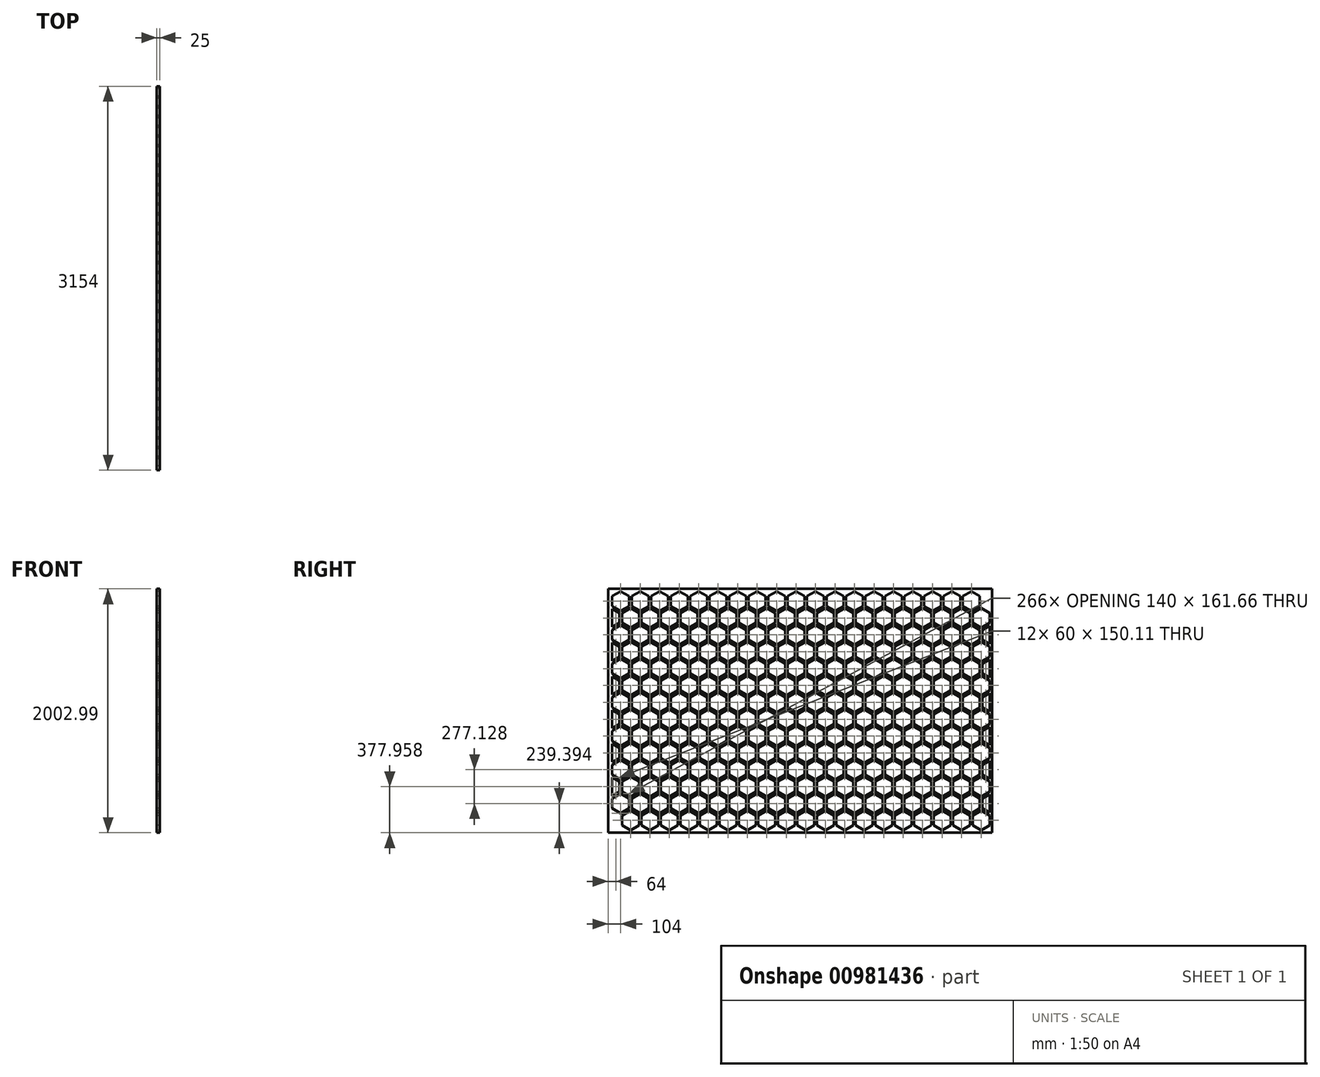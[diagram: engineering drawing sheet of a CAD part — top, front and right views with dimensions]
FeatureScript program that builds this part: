
annotation { "Feature Type Name" : "Feature", "Feature Type Description" : "" }
export const myFeature = defineFeature(function(context is Context, id is Id, definition is map)
    precondition{}
    {
        {
            var Q0;
            Q0=qCreatedBy(makeId("Right.planeOp"),FACE);
            var sketch = newSketch(context, id + "F0", { "sketchPlane" : qUnion([Q0])});
            skLineSegment(sketch, "E0", {"start": v(0, -80.83) * mm, "end": v(-70, -40.41) * mm});
            skLineSegment(sketch, "E1", {"start": v(-70, -40.41) * mm, "end": v(-70, 40.41) * mm});
            skLineSegment(sketch, "E2", {"start": v(-70, 40.41) * mm, "end": v(0, 80.83) * mm});
            skLineSegment(sketch, "E3", {"start": v(0, 80.83) * mm, "end": v(70, 40.41) * mm});
            skLineSegment(sketch, "E4", {"start": v(70, 40.41) * mm, "end": v(70, -40.41) * mm});
            skLineSegment(sketch, "E5", {"start": v(70, -40.41) * mm, "end": v(0, -80.83) * mm});
            skLineSegment(sketch, "E6.MirrorCS", {"start": v(10, 98.15) * mm, "end": v(80, 57.74) * mm});
            skLineSegment(sketch, "E7.MirrorCS", {"start": v(80, 57.74) * mm, "end": v(150, 98.15) * mm});
            skLineSegment(sketch, "E8.MirrorCS", {"start": v(80, 219.4) * mm, "end": v(10, 178.98) * mm});
            skLineSegment(sketch, "E9.MirrorCS", {"start": v(150, 178.98) * mm, "end": v(80, 219.4) * mm});
            skLineSegment(sketch, "E10.MirrorCS", {"start": v(150, 98.15) * mm, "end": v(150, 178.98) * mm});
            skLineSegment(sketch, "E11.MirrorCS", {"start": v(10, 178.98) * mm, "end": v(10, 98.15) * mm});
            skLineSegment(sketch, "E12.MirrorCS", {"start": v(160, -80.83) * mm, "end": v(230, -40.41) * mm});
            skLineSegment(sketch, "E13.MirrorCS", {"start": v(90, 40.41) * mm, "end": v(90, -40.41) * mm});
            skLineSegment(sketch, "E14.MirrorCS", {"start": v(230, 40.41) * mm, "end": v(160, 80.83) * mm});
            skLineSegment(sketch, "E15.MirrorCS", {"start": v(230, -40.41) * mm, "end": v(230, 40.41) * mm});
            skLineSegment(sketch, "E16.MirrorCS", {"start": v(160, 80.83) * mm, "end": v(90, 40.41) * mm});
            skLineSegment(sketch, "E17.MirrorCS", {"start": v(90, -40.41) * mm, "end": v(160, -80.83) * mm});
            skLineSegment(sketch, "E18.MirrorCS", {"start": v(410, 40.41) * mm, "end": v(410, -40.41) * mm});
            skLineSegment(sketch, "E19.MirrorCS", {"start": v(400, 57.74) * mm, "end": v(330, 98.15) * mm});
            skLineSegment(sketch, "E20.MirrorCS", {"start": v(320, 80.83) * mm, "end": v(390, 40.41) * mm});
            skLineSegment(sketch, "E21.MirrorCS", {"start": v(480, 80.83) * mm, "end": v(410, 40.41) * mm});
            skLineSegment(sketch, "E22.MirrorCS", {"start": v(320, -80.83) * mm, "end": v(250, -40.41) * mm});
            skLineSegment(sketch, "E23.MirrorCS", {"start": v(390, 40.41) * mm, "end": v(390, -40.41) * mm});
            skLineSegment(sketch, "E24.MirrorCS", {"start": v(250, -40.41) * mm, "end": v(250, 40.41) * mm});
            skLineSegment(sketch, "E25.MirrorCS", {"start": v(480, -80.83) * mm, "end": v(550, -40.41) * mm});
            skLineSegment(sketch, "E26.MirrorCS", {"start": v(330, 178.98) * mm, "end": v(400, 219.4) * mm});
            skLineSegment(sketch, "E27.MirrorCS", {"start": v(550, 40.41) * mm, "end": v(480, 80.83) * mm});
            skLineSegment(sketch, "E28.MirrorCS", {"start": v(470, 178.98) * mm, "end": v(470, 98.15) * mm});
            skLineSegment(sketch, "E29.MirrorCS", {"start": v(550, -40.41) * mm, "end": v(550, 40.41) * mm});
            skLineSegment(sketch, "E30.MirrorCS", {"start": v(390, -40.41) * mm, "end": v(320, -80.83) * mm});
            skLineSegment(sketch, "E31.MirrorCS", {"start": v(410, -40.41) * mm, "end": v(480, -80.83) * mm});
            skLineSegment(sketch, "E32.MirrorCS", {"start": v(250, 40.41) * mm, "end": v(320, 80.83) * mm});
            skLineSegment(sketch, "E33.MirrorCS", {"start": v(470, 98.15) * mm, "end": v(400, 57.74) * mm});
            skLineSegment(sketch, "E34.MirrorCS", {"start": v(330, 98.15) * mm, "end": v(330, 178.98) * mm});
            skLineSegment(sketch, "E35.MirrorCS", {"start": v(400, 219.4) * mm, "end": v(470, 178.98) * mm});
            skLineSegment(sketch, "E36.MirrorCS", {"start": v(1120, -80.83) * mm, "end": v(1190, -40.41) * mm});
            skLineSegment(sketch, "E37.MirrorCS", {"start": v(870, 40.41) * mm, "end": v(800, 80.83) * mm});
            skLineSegment(sketch, "E38.MirrorCS", {"start": v(800, 80.83) * mm, "end": v(730, 40.41) * mm});
            skLineSegment(sketch, "E39.MirrorCS", {"start": v(640, 80.83) * mm, "end": v(710, 40.41) * mm});
            skLineSegment(sketch, "E40.MirrorCS", {"start": v(790, 178.98) * mm, "end": v(720, 219.4) * mm});
            skLineSegment(sketch, "E41.MirrorCS", {"start": v(960, -80.83) * mm, "end": v(890, -40.41) * mm});
            skLineSegment(sketch, "E42.MirrorCS", {"start": v(570, 40.41) * mm, "end": v(640, 80.83) * mm});
            skLineSegment(sketch, "E43.MirrorCS", {"start": v(1120, 80.83) * mm, "end": v(1050, 40.41) * mm});
            skLineSegment(sketch, "E44.MirrorCS", {"start": v(970, 178.98) * mm, "end": v(1040, 219.4) * mm});
            skLineSegment(sketch, "E45.MirrorCS", {"start": v(650, 98.15) * mm, "end": v(720, 57.74) * mm});
            skLineSegment(sketch, "E46.MirrorCS", {"start": v(710, 40.41) * mm, "end": v(710, -40.41) * mm});
            skLineSegment(sketch, "E47.MirrorCS", {"start": v(1030, 40.41) * mm, "end": v(1030, -40.41) * mm});
            skLineSegment(sketch, "E48.MirrorCS", {"start": v(720, 219.4) * mm, "end": v(650, 178.98) * mm});
            skLineSegment(sketch, "E49.MirrorCS", {"start": v(890, -40.41) * mm, "end": v(890, 40.41) * mm});
            skLineSegment(sketch, "E50.MirrorCS", {"start": v(570, -40.41) * mm, "end": v(570, 40.41) * mm});
            skLineSegment(sketch, "E51.MirrorCS", {"start": v(1110, 98.15) * mm, "end": v(1040, 57.74) * mm});
            skLineSegment(sketch, "E52.MirrorCS", {"start": v(870, -40.41) * mm, "end": v(870, 40.41) * mm});
            skLineSegment(sketch, "E53.MirrorCS", {"start": v(1040, 57.74) * mm, "end": v(970, 98.15) * mm});
            skLineSegment(sketch, "E54.MirrorCS", {"start": v(890, 40.41) * mm, "end": v(960, 80.83) * mm});
            skLineSegment(sketch, "E55.MirrorCS", {"start": v(970, 98.15) * mm, "end": v(970, 178.98) * mm});
            skLineSegment(sketch, "E56.MirrorCS", {"start": v(730, -40.41) * mm, "end": v(800, -80.83) * mm});
            skLineSegment(sketch, "E57.MirrorCS", {"start": v(1110, 178.98) * mm, "end": v(1110, 98.15) * mm});
            skLineSegment(sketch, "E58.MirrorCS", {"start": v(790, 98.15) * mm, "end": v(790, 178.98) * mm});
            skLineSegment(sketch, "E59.MirrorCS", {"start": v(650, 178.98) * mm, "end": v(650, 98.15) * mm});
            skLineSegment(sketch, "E60.MirrorCS", {"start": v(1190, -40.41) * mm, "end": v(1190, 40.41) * mm});
            skLineSegment(sketch, "E61.MirrorCS", {"start": v(1190, 40.41) * mm, "end": v(1120, 80.83) * mm});
            skLineSegment(sketch, "E62.MirrorCS", {"start": v(960, 80.83) * mm, "end": v(1030, 40.41) * mm});
            skLineSegment(sketch, "E63.MirrorCS", {"start": v(710, -40.41) * mm, "end": v(640, -80.83) * mm});
            skLineSegment(sketch, "E64.MirrorCS", {"start": v(1030, -40.41) * mm, "end": v(960, -80.83) * mm});
            skLineSegment(sketch, "E65.MirrorCS", {"start": v(640, -80.83) * mm, "end": v(570, -40.41) * mm});
            skLineSegment(sketch, "E66.MirrorCS", {"start": v(730, 40.41) * mm, "end": v(730, -40.41) * mm});
            skLineSegment(sketch, "E67.MirrorCS", {"start": v(1050, -40.41) * mm, "end": v(1120, -80.83) * mm});
            skLineSegment(sketch, "E68.MirrorCS", {"start": v(720, 57.74) * mm, "end": v(790, 98.15) * mm});
            skLineSegment(sketch, "E69.MirrorCS", {"start": v(800, -80.83) * mm, "end": v(870, -40.41) * mm});
            skLineSegment(sketch, "E70.MirrorCS", {"start": v(1040, 219.4) * mm, "end": v(1110, 178.98) * mm});
            skLineSegment(sketch, "E71.MirrorCS", {"start": v(1050, 40.41) * mm, "end": v(1050, -40.41) * mm});
            skLineSegment(sketch, "E72.MirrorCS", {"start": v(-640, -80.83) * mm, "end": v(-710, -40.41) * mm});
            skLineSegment(sketch, "E73.MirrorCS", {"start": v(-710, 40.41) * mm, "end": v(-640, 80.83) * mm});
            skLineSegment(sketch, "E74.MirrorCS", {"start": v(-710, -40.41) * mm, "end": v(-710, 40.41) * mm});
            skLineSegment(sketch, "E75.MirrorCS", {"start": v(-160, 80.83) * mm, "end": v(-230, 40.41) * mm});
            skLineSegment(sketch, "E76.MirrorCS", {"start": v(-160, -80.83) * mm, "end": v(-90, -40.41) * mm});
            skLineSegment(sketch, "E77.MirrorCS", {"start": v(-250, -40.41) * mm, "end": v(-320, -80.83) * mm});
            skLineSegment(sketch, "E78.MirrorCS", {"start": v(-480, 80.83) * mm, "end": v(-550, 40.41) * mm});
            skLineSegment(sketch, "E79.MirrorCS", {"start": v(-490, 178.98) * mm, "end": v(-560, 219.4) * mm});
            skLineSegment(sketch, "E80.MirrorCS", {"start": v(-630, 98.15) * mm, "end": v(-560, 57.74) * mm});
            skLineSegment(sketch, "E81.MirrorCS", {"start": v(-570, -40.41) * mm, "end": v(-640, -80.83) * mm});
            skLineSegment(sketch, "E82.MirrorCS", {"start": v(-90, -40.41) * mm, "end": v(-90, 40.41) * mm});
            skLineSegment(sketch, "E83.MirrorCS", {"start": v(-630, 178.98) * mm, "end": v(-630, 98.15) * mm});
            skLineSegment(sketch, "E84.MirrorCS", {"start": v(-320, -80.83) * mm, "end": v(-390, -40.41) * mm});
            skLineSegment(sketch, "E85.MirrorCS", {"start": v(-480, -80.83) * mm, "end": v(-410, -40.41) * mm});
            skLineSegment(sketch, "E86.MirrorCS", {"start": v(-490, 98.15) * mm, "end": v(-490, 178.98) * mm});
            skLineSegment(sketch, "E87.MirrorCS", {"start": v(-570, 40.41) * mm, "end": v(-570, -40.41) * mm});
            skLineSegment(sketch, "E88.MirrorCS", {"start": v(-410, 40.41) * mm, "end": v(-480, 80.83) * mm});
            skLineSegment(sketch, "E89.MirrorCS", {"start": v(-170, 178.98) * mm, "end": v(-170, 98.15) * mm});
            skLineSegment(sketch, "E90.MirrorCS", {"start": v(-310, 178.98) * mm, "end": v(-240, 219.4) * mm});
            skLineSegment(sketch, "E91.MirrorCS", {"start": v(-230, 40.41) * mm, "end": v(-230, -40.41) * mm});
            skLineSegment(sketch, "E92.MirrorCS", {"start": v(-550, 40.41) * mm, "end": v(-550, -40.41) * mm});
            skLineSegment(sketch, "E93.MirrorCS", {"start": v(-390, 40.41) * mm, "end": v(-320, 80.83) * mm});
            skLineSegment(sketch, "E94.MirrorCS", {"start": v(-240, 219.4) * mm, "end": v(-170, 178.98) * mm});
            skLineSegment(sketch, "E95.MirrorCS", {"start": v(-560, 57.74) * mm, "end": v(-490, 98.15) * mm});
            skLineSegment(sketch, "E96.MirrorCS", {"start": v(-550, -40.41) * mm, "end": v(-480, -80.83) * mm});
            skLineSegment(sketch, "E97.MirrorCS", {"start": v(-250, 40.41) * mm, "end": v(-250, -40.41) * mm});
            skLineSegment(sketch, "E98.MirrorCS", {"start": v(-90, 40.41) * mm, "end": v(-160, 80.83) * mm});
            skLineSegment(sketch, "E99.MirrorCS", {"start": v(-230, -40.41) * mm, "end": v(-160, -80.83) * mm});
            skLineSegment(sketch, "E100.MirrorCS", {"start": v(-240, 57.74) * mm, "end": v(-310, 98.15) * mm});
            skLineSegment(sketch, "E101.MirrorCS", {"start": v(-310, 98.15) * mm, "end": v(-310, 178.98) * mm});
            skLineSegment(sketch, "E102.MirrorCS", {"start": v(-390, -40.41) * mm, "end": v(-390, 40.41) * mm});
            skLineSegment(sketch, "E103.MirrorCS", {"start": v(-170, 98.15) * mm, "end": v(-240, 57.74) * mm});
            skLineSegment(sketch, "E104.MirrorCS", {"start": v(-320, 80.83) * mm, "end": v(-250, 40.41) * mm});
            skLineSegment(sketch, "E105.MirrorCS", {"start": v(-560, 219.4) * mm, "end": v(-630, 178.98) * mm});
            skLineSegment(sketch, "E106.MirrorCS", {"start": v(-640, 80.83) * mm, "end": v(-570, 40.41) * mm});
            skLineSegment(sketch, "E107.MirrorCS", {"start": v(-410, -40.41) * mm, "end": v(-410, 40.41) * mm});
            skLineSegment(sketch, "E108.MirrorCS", {"start": v(-400, 57.74) * mm, "end": v(-470, 98.15) * mm});
            skLineSegment(sketch, "E109.MirrorCS", {"start": v(-330, 98.15) * mm, "end": v(-400, 57.74) * mm});
            skLineSegment(sketch, "E110.MirrorCS", {"start": v(-400, 219.4) * mm, "end": v(-330, 178.98) * mm});
            skLineSegment(sketch, "E111.MirrorCS", {"start": v(-470, 98.15) * mm, "end": v(-470, 178.98) * mm});
            skLineSegment(sketch, "E112.MirrorCS", {"start": v(-470, 178.98) * mm, "end": v(-400, 219.4) * mm});
            skLineSegment(sketch, "E113.MirrorCS", {"start": v(-330, 178.98) * mm, "end": v(-330, 98.15) * mm});
            skLineSegment(sketch, "E114.MirrorCS", {"start": v(310, 178.98) * mm, "end": v(310, 98.15) * mm});
            skLineSegment(sketch, "E115.MirrorCS", {"start": v(240, 219.4) * mm, "end": v(310, 178.98) * mm});
            skLineSegment(sketch, "E116.MirrorCS", {"start": v(240, 57.74) * mm, "end": v(170, 98.15) * mm});
            skLineSegment(sketch, "E117.MirrorCS", {"start": v(310, 98.15) * mm, "end": v(240, 57.74) * mm});
            skLineSegment(sketch, "E118.MirrorCS", {"start": v(170, 178.98) * mm, "end": v(240, 219.4) * mm});
            skLineSegment(sketch, "E119.MirrorCS", {"start": v(170, 98.15) * mm, "end": v(170, 178.98) * mm});
            skLineSegment(sketch, "E120.MirrorCS", {"start": v(-10, 98.15) * mm, "end": v(-10, 178.98) * mm});
            skLineSegment(sketch, "E121.MirrorCS", {"start": v(-80, 57.74) * mm, "end": v(-10, 98.15) * mm});
            skLineSegment(sketch, "E122.MirrorCS", {"start": v(-150, 98.15) * mm, "end": v(-80, 57.74) * mm});
            skLineSegment(sketch, "E123.MirrorCS", {"start": v(-150, 178.98) * mm, "end": v(-150, 98.15) * mm});
            skLineSegment(sketch, "E124.MirrorCS", {"start": v(-80, 219.4) * mm, "end": v(-150, 178.98) * mm});
            skLineSegment(sketch, "E125.MirrorCS", {"start": v(-10, 178.98) * mm, "end": v(-80, 219.4) * mm});
            skLineSegment(sketch, "E126.MirrorCS", {"start": v(-790, 178.98) * mm, "end": v(-790, 98.15) * mm});
            skLineSegment(sketch, "E127.MirrorCS", {"start": v(-720, 219.4) * mm, "end": v(-790, 178.98) * mm});
            skLineSegment(sketch, "E128.MirrorCS", {"start": v(-650, 178.98) * mm, "end": v(-720, 219.4) * mm});
            skLineSegment(sketch, "E129.MirrorCS", {"start": v(-650, 98.15) * mm, "end": v(-650, 178.98) * mm});
            skLineSegment(sketch, "E130.MirrorCS", {"start": v(-720, 57.74) * mm, "end": v(-650, 98.15) * mm});
            skLineSegment(sketch, "E131.MirrorCS", {"start": v(-790, 98.15) * mm, "end": v(-720, 57.74) * mm});
            skLineSegment(sketch, "E132.MirrorCS", {"start": v(1130, 98.15) * mm, "end": v(1190, 63.5) * mm});
            skLineSegment(sketch, "E133.MirrorCS", {"start": v(1130, 178.98) * mm, "end": v(1130, 98.15) * mm});
            skLineSegment(sketch, "E134.MirrorCS", {"start": v(1190, 213.62) * mm, "end": v(1130, 178.98) * mm});
            skLineSegment(sketch, "E135.MirrorCS", {"start": v(950, 178.98) * mm, "end": v(950, 98.15) * mm});
            skLineSegment(sketch, "E136.MirrorCS", {"start": v(880, 219.4) * mm, "end": v(950, 178.98) * mm});
            skLineSegment(sketch, "E137.MirrorCS", {"start": v(950, 98.15) * mm, "end": v(880, 57.74) * mm});
            skLineSegment(sketch, "E138.MirrorCS", {"start": v(880, 57.74) * mm, "end": v(810, 98.15) * mm});
            skLineSegment(sketch, "E139.MirrorCS", {"start": v(810, 98.15) * mm, "end": v(810, 178.98) * mm});
            skLineSegment(sketch, "E140.MirrorCS", {"start": v(810, 178.98) * mm, "end": v(880, 219.4) * mm});
            skLineSegment(sketch, "E141.MirrorCS", {"start": v(490, 98.15) * mm, "end": v(560, 57.74) * mm});
            skLineSegment(sketch, "E142.MirrorCS", {"start": v(560, 57.74) * mm, "end": v(630, 98.15) * mm});
            skLineSegment(sketch, "E143.MirrorCS", {"start": v(630, 98.15) * mm, "end": v(630, 178.98) * mm});
            skLineSegment(sketch, "E144.MirrorCS", {"start": v(630, 178.98) * mm, "end": v(560, 219.4) * mm});
            skLineSegment(sketch, "E145.MirrorCS", {"start": v(560, 219.4) * mm, "end": v(490, 178.98) * mm});
            skLineSegment(sketch, "E146.MirrorCS", {"start": v(490, 178.98) * mm, "end": v(490, 98.15) * mm});
            skLineSegment(sketch, "E147.MirrorCS", {"start": v(0, 357.96) * mm, "end": v(-70, 317.54) * mm});
            skLineSegment(sketch, "E148.MirrorCS", {"start": v(0, 196.3) * mm, "end": v(70, 236.71) * mm});
            skLineSegment(sketch, "E149.MirrorCS", {"start": v(-70, 236.71) * mm, "end": v(0, 196.3) * mm});
            skLineSegment(sketch, "E150.MirrorCS", {"start": v(-170, 178.98) * mm, "end": v(-240, 219.4) * mm});
            skLineSegment(sketch, "E151.MirrorCS", {"start": v(640, 357.96) * mm, "end": v(570, 317.54) * mm});
            skLineSegment(sketch, "E152.MirrorCS", {"start": v(-80, 219.4) * mm, "end": v(-10, 178.98) * mm});
            skLineSegment(sketch, "E153.MirrorCS", {"start": v(560, 219.4) * mm, "end": v(630, 178.98) * mm});
            skLineSegment(sketch, "E154.MirrorCS", {"start": v(390, 236.71) * mm, "end": v(390, 317.54) * mm});
            skLineSegment(sketch, "E155.MirrorCS", {"start": v(10, 178.98) * mm, "end": v(80, 219.4) * mm});
            skLineSegment(sketch, "E156.MirrorCS", {"start": v(-250, 236.71) * mm, "end": v(-250, 317.54) * mm});
            skLineSegment(sketch, "E157.MirrorCS", {"start": v(710, 236.71) * mm, "end": v(710, 317.54) * mm});
            skLineSegment(sketch, "E158.MirrorCS", {"start": v(240, 219.4) * mm, "end": v(170, 178.98) * mm});
            skLineSegment(sketch, "E159.MirrorCS", {"start": v(-150, 178.98) * mm, "end": v(-80, 219.4) * mm});
            skLineSegment(sketch, "E160.MirrorCS", {"start": v(-400, 219.4) * mm, "end": v(-470, 178.98) * mm});
            skLineSegment(sketch, "E161.MirrorCS", {"start": v(410, 236.71) * mm, "end": v(410, 317.54) * mm});
            skLineSegment(sketch, "E162.MirrorCS", {"start": v(640, 196.3) * mm, "end": v(710, 236.71) * mm});
            skLineSegment(sketch, "E163.MirrorCS", {"start": v(550, 236.71) * mm, "end": v(480, 196.3) * mm});
            skLineSegment(sketch, "E164.MirrorCS", {"start": v(-240, 219.4) * mm, "end": v(-310, 178.98) * mm});
            skLineSegment(sketch, "E165.MirrorCS", {"start": v(480, 357.96) * mm, "end": v(550, 317.54) * mm});
            skLineSegment(sketch, "E166.MirrorCS", {"start": v(570, 236.71) * mm, "end": v(640, 196.3) * mm});
            skLineSegment(sketch, "E167.MirrorCS", {"start": v(-480, 196.3) * mm, "end": v(-550, 236.71) * mm});
            skLineSegment(sketch, "E168.MirrorCS", {"start": v(950, 178.98) * mm, "end": v(880, 219.4) * mm});
            skLineSegment(sketch, "E169.MirrorCS", {"start": v(-480, 357.96) * mm, "end": v(-410, 317.54) * mm});
            skLineSegment(sketch, "E170.MirrorCS", {"start": v(-410, 317.54) * mm, "end": v(-410, 236.71) * mm});
            skLineSegment(sketch, "E171.MirrorCS", {"start": v(-560, 219.4) * mm, "end": v(-490, 178.98) * mm});
            skLineSegment(sketch, "E172.MirrorCS", {"start": v(-550, 317.54) * mm, "end": v(-480, 357.96) * mm});
            skLineSegment(sketch, "E173.MirrorCS", {"start": v(480, 196.3) * mm, "end": v(410, 236.71) * mm});
            skLineSegment(sketch, "E174.MirrorCS", {"start": v(320, 196.3) * mm, "end": v(390, 236.71) * mm});
            skLineSegment(sketch, "E175.MirrorCS", {"start": v(320, 357.96) * mm, "end": v(250, 317.54) * mm});
            skLineSegment(sketch, "E176.MirrorCS", {"start": v(90, 236.71) * mm, "end": v(90, 317.54) * mm});
            skLineSegment(sketch, "E177.MirrorCS", {"start": v(80, 219.4) * mm, "end": v(150, 178.98) * mm});
            skLineSegment(sketch, "E178.MirrorCS", {"start": v(960, 196.3) * mm, "end": v(1030, 236.71) * mm});
            skLineSegment(sketch, "E179.MirrorCS", {"start": v(-230, 317.54) * mm, "end": v(-160, 357.96) * mm});
            skLineSegment(sketch, "E180.MirrorCS", {"start": v(400, 219.4) * mm, "end": v(330, 178.98) * mm});
            skLineSegment(sketch, "E181.MirrorCS", {"start": v(160, 357.96) * mm, "end": v(230, 317.54) * mm});
            skLineSegment(sketch, "E182.MirrorCS", {"start": v(-390, 317.54) * mm, "end": v(-390, 236.71) * mm});
            skLineSegment(sketch, "E183.MirrorCS", {"start": v(650, 178.98) * mm, "end": v(720, 219.4) * mm});
            skLineSegment(sketch, "E184.MirrorCS", {"start": v(-90, 236.71) * mm, "end": v(-160, 196.3) * mm});
            skLineSegment(sketch, "E185.MirrorCS", {"start": v(-330, 178.98) * mm, "end": v(-400, 219.4) * mm});
            skLineSegment(sketch, "E186.MirrorCS", {"start": v(-640, 196.3) * mm, "end": v(-570, 236.71) * mm});
            skLineSegment(sketch, "E187.MirrorCS", {"start": v(1120, 196.3) * mm, "end": v(1050, 236.71) * mm});
            skLineSegment(sketch, "E188.MirrorCS", {"start": v(1030, 317.54) * mm, "end": v(960, 357.96) * mm});
            skLineSegment(sketch, "E189.MirrorCS", {"start": v(160, 196.3) * mm, "end": v(90, 236.71) * mm});
            skLineSegment(sketch, "E190.MirrorCS", {"start": v(470, 178.98) * mm, "end": v(400, 219.4) * mm});
            skLineSegment(sketch, "E191.MirrorCS", {"start": v(880, 219.4) * mm, "end": v(810, 178.98) * mm});
            skLineSegment(sketch, "E192.MirrorCS", {"start": v(310, 178.98) * mm, "end": v(240, 219.4) * mm});
            skLineSegment(sketch, "E193.MirrorCS", {"start": v(-390, 236.71) * mm, "end": v(-320, 196.3) * mm});
            skLineSegment(sketch, "E194.MirrorCS", {"start": v(-410, 236.71) * mm, "end": v(-480, 196.3) * mm});
            skLineSegment(sketch, "E195.MirrorCS", {"start": v(-320, 196.3) * mm, "end": v(-250, 236.71) * mm});
            skLineSegment(sketch, "E196.MirrorCS", {"start": v(-730, 317.54) * mm, "end": v(-730, 236.71) * mm});
            skLineSegment(sketch, "E197.MirrorCS", {"start": v(-710, 236.71) * mm, "end": v(-640, 196.3) * mm});
            skLineSegment(sketch, "E198.MirrorCS", {"start": v(1190, 236.71) * mm, "end": v(1120, 196.3) * mm});
            skLineSegment(sketch, "E199.MirrorCS", {"start": v(230, 317.54) * mm, "end": v(230, 236.71) * mm});
            skLineSegment(sketch, "E200.MirrorCS", {"start": v(-160, 196.3) * mm, "end": v(-230, 236.71) * mm});
            skLineSegment(sketch, "E201.MirrorCS", {"start": v(1190, 317.54) * mm, "end": v(1190, 236.71) * mm});
            skLineSegment(sketch, "E202.MirrorCS", {"start": v(250, 236.71) * mm, "end": v(320, 196.3) * mm});
            skLineSegment(sketch, "E203.MirrorCS", {"start": v(1130, 178.98) * mm, "end": v(1190, 213.62) * mm});
            skLineSegment(sketch, "E204.MirrorCS", {"start": v(720, 219.4) * mm, "end": v(790, 178.98) * mm});
            skLineSegment(sketch, "E205.MirrorCS", {"start": v(870, 236.71) * mm, "end": v(800, 196.3) * mm});
            skLineSegment(sketch, "E206.MirrorCS", {"start": v(410, 317.54) * mm, "end": v(480, 357.96) * mm});
            skLineSegment(sketch, "E207.MirrorCS", {"start": v(730, 317.54) * mm, "end": v(800, 357.96) * mm});
            skLineSegment(sketch, "E208.MirrorCS", {"start": v(-570, 317.54) * mm, "end": v(-640, 357.96) * mm});
            skLineSegment(sketch, "E209.MirrorCS", {"start": v(-230, 236.71) * mm, "end": v(-230, 317.54) * mm});
            skLineSegment(sketch, "E210.MirrorCS", {"start": v(1120, 357.96) * mm, "end": v(1190, 317.54) * mm});
            skLineSegment(sketch, "E211.MirrorCS", {"start": v(1050, 236.71) * mm, "end": v(1050, 317.54) * mm});
            skLineSegment(sketch, "E212.MirrorCS", {"start": v(730, 236.71) * mm, "end": v(730, 317.54) * mm});
            skLineSegment(sketch, "E213.MirrorCS", {"start": v(-250, 317.54) * mm, "end": v(-320, 357.96) * mm});
            skLineSegment(sketch, "E214.MirrorCS", {"start": v(-570, 236.71) * mm, "end": v(-570, 317.54) * mm});
            skLineSegment(sketch, "E215.MirrorCS", {"start": v(-640, 357.96) * mm, "end": v(-710, 317.54) * mm});
            skLineSegment(sketch, "E216.MirrorCS", {"start": v(1040, 219.4) * mm, "end": v(970, 178.98) * mm});
            skLineSegment(sketch, "E217.MirrorCS", {"start": v(-160, 357.96) * mm, "end": v(-90, 317.54) * mm});
            skLineSegment(sketch, "E218.MirrorCS", {"start": v(-710, 317.54) * mm, "end": v(-710, 236.71) * mm});
            skLineSegment(sketch, "E219.MirrorCS", {"start": v(800, 196.3) * mm, "end": v(730, 236.71) * mm});
            skLineSegment(sketch, "E220.MirrorCS", {"start": v(890, 317.54) * mm, "end": v(890, 236.71) * mm});
            skLineSegment(sketch, "E221.MirrorCS", {"start": v(550, 317.54) * mm, "end": v(550, 236.71) * mm});
            skLineSegment(sketch, "E222.MirrorCS", {"start": v(-90, 317.54) * mm, "end": v(-90, 236.71) * mm});
            skLineSegment(sketch, "E223.MirrorCS", {"start": v(-720, 219.4) * mm, "end": v(-650, 178.98) * mm});
            skLineSegment(sketch, "E224.MirrorCS", {"start": v(90, 317.54) * mm, "end": v(160, 357.96) * mm});
            skLineSegment(sketch, "E225.MirrorCS", {"start": v(1110, 178.98) * mm, "end": v(1040, 219.4) * mm});
            skLineSegment(sketch, "E226.MirrorCS", {"start": v(1030, 236.71) * mm, "end": v(1030, 317.54) * mm});
            skLineSegment(sketch, "E227.MirrorCS", {"start": v(250, 317.54) * mm, "end": v(250, 236.71) * mm});
            skLineSegment(sketch, "E228.MirrorCS", {"start": v(-790, 178.98) * mm, "end": v(-720, 219.4) * mm});
            skLineSegment(sketch, "E229.MirrorCS", {"start": v(-630, 178.98) * mm, "end": v(-560, 219.4) * mm});
            skLineSegment(sketch, "E230.MirrorCS", {"start": v(890, 236.71) * mm, "end": v(960, 196.3) * mm});
            skLineSegment(sketch, "E231.MirrorCS", {"start": v(230, 236.71) * mm, "end": v(160, 196.3) * mm});
            skLineSegment(sketch, "E232.MirrorCS", {"start": v(490, 178.98) * mm, "end": v(560, 219.4) * mm});
            skLineSegment(sketch, "E233.MirrorCS", {"start": v(1050, 317.54) * mm, "end": v(1120, 357.96) * mm});
            skLineSegment(sketch, "E234.MirrorCS", {"start": v(70, 317.54) * mm, "end": v(0, 357.96) * mm});
            skLineSegment(sketch, "E235.MirrorCS", {"start": v(870, 317.54) * mm, "end": v(870, 236.71) * mm});
            skLineSegment(sketch, "E236.MirrorCS", {"start": v(-550, 236.71) * mm, "end": v(-550, 317.54) * mm});
            skLineSegment(sketch, "E237.MirrorCS", {"start": v(-320, 357.96) * mm, "end": v(-390, 317.54) * mm});
            skLineSegment(sketch, "E238.MirrorCS", {"start": v(390, 317.54) * mm, "end": v(320, 357.96) * mm});
            skLineSegment(sketch, "E239.MirrorCS", {"start": v(570, 317.54) * mm, "end": v(570, 236.71) * mm});
            skLineSegment(sketch, "E240.MirrorCS", {"start": v(70, 236.71) * mm, "end": v(70, 317.54) * mm});
            skLineSegment(sketch, "E241.MirrorCS", {"start": v(960, 357.96) * mm, "end": v(890, 317.54) * mm});
            skLineSegment(sketch, "E242.MirrorCS", {"start": v(710, 317.54) * mm, "end": v(640, 357.96) * mm});
            skLineSegment(sketch, "E243.MirrorCS", {"start": v(800, 357.96) * mm, "end": v(870, 317.54) * mm});
            skLineSegment(sketch, "E244.MirrorCS", {"start": v(-70, 317.54) * mm, "end": v(-70, 236.71) * mm});
            skLineSegment(sketch, "E245.MirrorCS", {"start": v(1040, 334.86) * mm, "end": v(970, 375.28) * mm});
            skLineSegment(sketch, "E246.MirrorCS", {"start": v(80, 334.86) * mm, "end": v(150, 375.28) * mm});
            skLineSegment(sketch, "E247.MirrorCS", {"start": v(-240, 334.86) * mm, "end": v(-170, 375.28) * mm});
            skLineSegment(sketch, "E248.MirrorCS", {"start": v(0, 635.09) * mm, "end": v(-70, 594.67) * mm});
            skLineSegment(sketch, "E249.MirrorCS", {"start": v(1040, 334.86) * mm, "end": v(1110, 375.28) * mm});
            skLineSegment(sketch, "E250.MirrorCS", {"start": v(0, 473.43) * mm, "end": v(70, 513.84) * mm});
            skLineSegment(sketch, "E251.MirrorCS", {"start": v(-630, 375.28) * mm, "end": v(-560, 334.86) * mm});
            skLineSegment(sketch, "E252.MirrorCS", {"start": v(-720, 334.86) * mm, "end": v(-790, 375.28) * mm});
            skLineSegment(sketch, "E253.MirrorCS", {"start": v(720, 334.86) * mm, "end": v(650, 375.28) * mm});
            skLineSegment(sketch, "E254.MirrorCS", {"start": v(310, 375.28) * mm, "end": v(240, 334.86) * mm});
            skLineSegment(sketch, "E255.MirrorCS", {"start": v(470, 375.28) * mm, "end": v(400, 334.86) * mm});
            skLineSegment(sketch, "E256.MirrorCS", {"start": v(10, 375.28) * mm, "end": v(80, 334.86) * mm});
            skLineSegment(sketch, "E257.MirrorCS", {"start": v(-720, 334.86) * mm, "end": v(-650, 375.28) * mm});
            skLineSegment(sketch, "E258.MirrorCS", {"start": v(-150, 375.28) * mm, "end": v(-80, 334.86) * mm});
            skLineSegment(sketch, "E259.MirrorCS", {"start": v(-470, 375.28) * mm, "end": v(-400, 334.86) * mm});
            skLineSegment(sketch, "E260.MirrorCS", {"start": v(400, 334.86) * mm, "end": v(330, 375.28) * mm});
            skLineSegment(sketch, "E261.MirrorCS", {"start": v(170, 375.28) * mm, "end": v(240, 334.86) * mm});
            skLineSegment(sketch, "E262.MirrorCS", {"start": v(1130, 375.28) * mm, "end": v(1190, 340.64) * mm});
            skLineSegment(sketch, "E263.MirrorCS", {"start": v(-330, 375.28) * mm, "end": v(-400, 334.86) * mm});
            skLineSegment(sketch, "E264.MirrorCS", {"start": v(950, 375.28) * mm, "end": v(880, 334.86) * mm});
            skLineSegment(sketch, "E265.MirrorCS", {"start": v(880, 334.86) * mm, "end": v(810, 375.28) * mm});
            skLineSegment(sketch, "E266.MirrorCS", {"start": v(720, 334.86) * mm, "end": v(790, 375.28) * mm});
            skLineSegment(sketch, "E267.MirrorCS", {"start": v(-240, 334.86) * mm, "end": v(-310, 375.28) * mm});
            skLineSegment(sketch, "E268.MirrorCS", {"start": v(-560, 334.86) * mm, "end": v(-490, 375.28) * mm});
            skLineSegment(sketch, "E269.MirrorCS", {"start": v(560, 334.86) * mm, "end": v(490, 375.28) * mm});
            skLineSegment(sketch, "E270.MirrorCS", {"start": v(560, 334.86) * mm, "end": v(630, 375.28) * mm});
            skLineSegment(sketch, "E271.MirrorCS", {"start": v(-80, 334.86) * mm, "end": v(-10, 375.28) * mm});
            skLineSegment(sketch, "E272.MirrorCS", {"start": v(160, 473.43) * mm, "end": v(90, 513.84) * mm});
            skLineSegment(sketch, "E273.MirrorCS", {"start": v(1110, 375.28) * mm, "end": v(1110, 456.1) * mm});
            skLineSegment(sketch, "E274.MirrorCS", {"start": v(230, 513.84) * mm, "end": v(160, 473.43) * mm});
            skLineSegment(sketch, "E275.MirrorCS", {"start": v(-710, 594.67) * mm, "end": v(-710, 513.84) * mm});
            skLineSegment(sketch, "E276.MirrorCS", {"start": v(-170, 456.1) * mm, "end": v(-240, 496.52) * mm});
            skLineSegment(sketch, "E277.MirrorCS", {"start": v(390, 513.84) * mm, "end": v(390, 594.67) * mm});
            skLineSegment(sketch, "E278.MirrorCS", {"start": v(970, 375.28) * mm, "end": v(1040, 334.86) * mm});
            skLineSegment(sketch, "E279.MirrorCS", {"start": v(1130, 375.28) * mm, "end": v(1130, 456.1) * mm});
            skLineSegment(sketch, "E280.MirrorCS", {"start": v(710, 594.67) * mm, "end": v(640, 635.09) * mm});
            skLineSegment(sketch, "E281.MirrorCS", {"start": v(570, 513.84) * mm, "end": v(640, 473.43) * mm});
            skLineSegment(sketch, "E282.MirrorCS", {"start": v(1190, 594.67) * mm, "end": v(1190, 513.84) * mm});
            skLineSegment(sketch, "E283.MirrorCS", {"start": v(1050, 513.84) * mm, "end": v(1050, 594.67) * mm});
            skLineSegment(sketch, "E284.MirrorCS", {"start": v(870, 317.54) * mm, "end": v(800, 357.96) * mm});
            skLineSegment(sketch, "E285.MirrorCS", {"start": v(630, 375.28) * mm, "end": v(560, 334.86) * mm});
            skLineSegment(sketch, "E286.MirrorCS", {"start": v(90, 594.67) * mm, "end": v(160, 635.09) * mm});
            skLineSegment(sketch, "E287.MirrorCS", {"start": v(640, 357.96) * mm, "end": v(710, 317.54) * mm});
            skLineSegment(sketch, "E288.MirrorCS", {"start": v(-570, 513.84) * mm, "end": v(-570, 594.67) * mm});
            skLineSegment(sketch, "E289.MirrorCS", {"start": v(810, 375.28) * mm, "end": v(880, 334.86) * mm});
            skLineSegment(sketch, "E290.MirrorCS", {"start": v(-790, 375.28) * mm, "end": v(-720, 334.86) * mm});
            skLineSegment(sketch, "E291.MirrorCS", {"start": v(-320, 635.09) * mm, "end": v(-390, 594.67) * mm});
            skLineSegment(sketch, "E292.MirrorCS", {"start": v(-560, 334.86) * mm, "end": v(-630, 375.28) * mm});
            skLineSegment(sketch, "E293.MirrorCS", {"start": v(250, 594.67) * mm, "end": v(250, 513.84) * mm});
            skLineSegment(sketch, "E294.MirrorCS", {"start": v(310, 456.1) * mm, "end": v(240, 496.52) * mm});
            skLineSegment(sketch, "E295.MirrorCS", {"start": v(-790, 456.1) * mm, "end": v(-720, 496.52) * mm});
            skLineSegment(sketch, "E296.MirrorCS", {"start": v(800, 357.96) * mm, "end": v(730, 317.54) * mm});
            skLineSegment(sketch, "E297.MirrorCS", {"start": v(880, 334.86) * mm, "end": v(950, 375.28) * mm});
            skLineSegment(sketch, "E298.MirrorCS", {"start": v(-710, 317.54) * mm, "end": v(-640, 357.96) * mm});
            skLineSegment(sketch, "E299.MirrorCS", {"start": v(-10, 375.28) * mm, "end": v(-80, 334.86) * mm});
            skLineSegment(sketch, "E300.MirrorCS", {"start": v(-560, 496.52) * mm, "end": v(-490, 456.1) * mm});
            skLineSegment(sketch, "E301.MirrorCS", {"start": v(240, 334.86) * mm, "end": v(310, 375.28) * mm});
            skLineSegment(sketch, "E302.MirrorCS", {"start": v(800, 473.43) * mm, "end": v(730, 513.84) * mm});
            skLineSegment(sketch, "E303.MirrorCS", {"start": v(650, 375.28) * mm, "end": v(650, 456.1) * mm});
            skLineSegment(sketch, "E304.MirrorCS", {"start": v(-490, 375.28) * mm, "end": v(-560, 334.86) * mm});
            skLineSegment(sketch, "E305.MirrorCS", {"start": v(160, 635.09) * mm, "end": v(230, 594.67) * mm});
            skLineSegment(sketch, "E306.MirrorCS", {"start": v(960, 473.43) * mm, "end": v(1030, 513.84) * mm});
            skLineSegment(sketch, "E307.MirrorCS", {"start": v(160, 357.96) * mm, "end": v(90, 317.54) * mm});
            skLineSegment(sketch, "E308.MirrorCS", {"start": v(-310, 375.28) * mm, "end": v(-240, 334.86) * mm});
            skLineSegment(sketch, "E309.MirrorCS", {"start": v(890, 594.67) * mm, "end": v(890, 513.84) * mm});
            skLineSegment(sketch, "E310.MirrorCS", {"start": v(-170, 375.28) * mm, "end": v(-240, 334.86) * mm});
            skLineSegment(sketch, "E311.MirrorCS", {"start": v(-330, 375.28) * mm, "end": v(-330, 456.1) * mm});
            skLineSegment(sketch, "E312.MirrorCS", {"start": v(790, 375.28) * mm, "end": v(720, 334.86) * mm});
            skLineSegment(sketch, "E313.MirrorCS", {"start": v(10, 375.28) * mm, "end": v(10, 456.1) * mm});
            skLineSegment(sketch, "E314.MirrorCS", {"start": v(-70, 594.67) * mm, "end": v(-70, 513.84) * mm});
            skLineSegment(sketch, "E315.MirrorCS", {"start": v(-400, 334.86) * mm, "end": v(-330, 375.28) * mm});
            skLineSegment(sketch, "E316.MirrorCS", {"start": v(320, 357.96) * mm, "end": v(390, 317.54) * mm});
            skLineSegment(sketch, "E317.MirrorCS", {"start": v(1120, 357.96) * mm, "end": v(1050, 317.54) * mm});
            skLineSegment(sketch, "E318.MirrorCS", {"start": v(-730, 513.84) * mm, "end": v(-800, 473.43) * mm});
            skLineSegment(sketch, "E319.MirrorCS", {"start": v(-480, 473.43) * mm, "end": v(-550, 513.84) * mm});
            skLineSegment(sketch, "E320.MirrorCS", {"start": v(170, 456.1) * mm, "end": v(170, 375.28) * mm});
            skLineSegment(sketch, "E321.MirrorCS", {"start": v(-320, 473.43) * mm, "end": v(-250, 513.84) * mm});
            skLineSegment(sketch, "E322.MirrorCS", {"start": v(1030, 594.67) * mm, "end": v(960, 635.09) * mm});
            skLineSegment(sketch, "E323.MirrorCS", {"start": v(410, 594.67) * mm, "end": v(480, 635.09) * mm});
            skLineSegment(sketch, "E324.MirrorCS", {"start": v(570, 317.54) * mm, "end": v(640, 357.96) * mm});
            skLineSegment(sketch, "E325.MirrorCS", {"start": v(-250, 594.67) * mm, "end": v(-320, 635.09) * mm});
            skLineSegment(sketch, "E326.MirrorCS", {"start": v(230, 594.67) * mm, "end": v(230, 513.84) * mm});
            skLineSegment(sketch, "E327.MirrorCS", {"start": v(-160, 635.09) * mm, "end": v(-90, 594.67) * mm});
            skLineSegment(sketch, "E328.MirrorCS", {"start": v(1040, 496.52) * mm, "end": v(970, 456.1) * mm});
            skLineSegment(sketch, "E329.MirrorCS", {"start": v(320, 635.09) * mm, "end": v(250, 594.67) * mm});
            skLineSegment(sketch, "E330.MirrorCS", {"start": v(-150, 375.28) * mm, "end": v(-150, 456.1) * mm});
            skLineSegment(sketch, "E331.MirrorCS", {"start": v(-70, 317.54) * mm, "end": v(0, 357.96) * mm});
            skLineSegment(sketch, "E332.MirrorCS", {"start": v(-70, 513.84) * mm, "end": v(0, 473.43) * mm});
            skLineSegment(sketch, "E333.MirrorCS", {"start": v(90, 513.84) * mm, "end": v(90, 594.67) * mm});
            skLineSegment(sketch, "E334.MirrorCS", {"start": v(730, 513.84) * mm, "end": v(730, 594.67) * mm});
            skLineSegment(sketch, "E335.MirrorCS", {"start": v(490, 375.28) * mm, "end": v(490, 456.1) * mm});
            skLineSegment(sketch, "E336.MirrorCS", {"start": v(810, 456.1) * mm, "end": v(810, 375.28) * mm});
            skLineSegment(sketch, "E337.MirrorCS", {"start": v(470, 375.28) * mm, "end": v(470, 456.1) * mm});
            skLineSegment(sketch, "E338.MirrorCS", {"start": v(-400, 334.86) * mm, "end": v(-470, 375.28) * mm});
            skLineSegment(sketch, "E339.MirrorCS", {"start": v(0, 357.96) * mm, "end": v(70, 317.54) * mm});
            skLineSegment(sketch, "E340.MirrorCS", {"start": v(-790, 375.28) * mm, "end": v(-790, 456.1) * mm});
            skLineSegment(sketch, "E341.MirrorCS", {"start": v(-730, 594.67) * mm, "end": v(-730, 513.84) * mm});
            skLineSegment(sketch, "E342.MirrorCS", {"start": v(-170, 375.28) * mm, "end": v(-170, 456.1) * mm});
            skLineSegment(sketch, "E343.MirrorCS", {"start": v(-550, 513.84) * mm, "end": v(-550, 594.67) * mm});
            skLineSegment(sketch, "E344.MirrorCS", {"start": v(-470, 456.1) * mm, "end": v(-470, 375.28) * mm});
            skLineSegment(sketch, "E345.MirrorCS", {"start": v(950, 375.28) * mm, "end": v(950, 456.1) * mm});
            skLineSegment(sketch, "E346.MirrorCS", {"start": v(240, 334.86) * mm, "end": v(170, 375.28) * mm});
            skLineSegment(sketch, "E347.MirrorCS", {"start": v(-480, 357.96) * mm, "end": v(-550, 317.54) * mm});
            skLineSegment(sketch, "E348.MirrorCS", {"start": v(470, 456.1) * mm, "end": v(400, 496.52) * mm});
            skLineSegment(sketch, "E349.MirrorCS", {"start": v(-490, 456.1) * mm, "end": v(-490, 375.28) * mm});
            skLineSegment(sketch, "E350.MirrorCS", {"start": v(-390, 513.84) * mm, "end": v(-320, 473.43) * mm});
            skLineSegment(sketch, "E351.MirrorCS", {"start": v(250, 317.54) * mm, "end": v(320, 357.96) * mm});
            skLineSegment(sketch, "E352.MirrorCS", {"start": v(970, 456.1) * mm, "end": v(970, 375.28) * mm});
            skLineSegment(sketch, "E353.MirrorCS", {"start": v(-250, 513.84) * mm, "end": v(-250, 594.67) * mm});
            skLineSegment(sketch, "E354.MirrorCS", {"start": v(-480, 635.09) * mm, "end": v(-410, 594.67) * mm});
            skLineSegment(sketch, "E355.MirrorCS", {"start": v(-90, 513.84) * mm, "end": v(-160, 473.43) * mm});
            skLineSegment(sketch, "E356.MirrorCS", {"start": v(870, 594.67) * mm, "end": v(870, 513.84) * mm});
            skLineSegment(sketch, "E357.MirrorCS", {"start": v(1120, 635.09) * mm, "end": v(1190, 594.67) * mm});
            skLineSegment(sketch, "E358.MirrorCS", {"start": v(320, 473.43) * mm, "end": v(390, 513.84) * mm});
            skLineSegment(sketch, "E359.MirrorCS", {"start": v(-80, 496.52) * mm, "end": v(-10, 456.1) * mm});
            skLineSegment(sketch, "E360.MirrorCS", {"start": v(-570, 594.67) * mm, "end": v(-640, 635.09) * mm});
            skLineSegment(sketch, "E361.MirrorCS", {"start": v(870, 513.84) * mm, "end": v(800, 473.43) * mm});
            skLineSegment(sketch, "E362.MirrorCS", {"start": v(-10, 456.1) * mm, "end": v(-10, 375.28) * mm});
            skLineSegment(sketch, "E363.MirrorCS", {"start": v(80, 334.86) * mm, "end": v(10, 375.28) * mm});
            skLineSegment(sketch, "E364.MirrorCS", {"start": v(-310, 456.1) * mm, "end": v(-310, 375.28) * mm});
            skLineSegment(sketch, "E365.MirrorCS", {"start": v(70, 594.67) * mm, "end": v(0, 635.09) * mm});
            skLineSegment(sketch, "E366.MirrorCS", {"start": v(480, 635.09) * mm, "end": v(550, 594.67) * mm});
            skLineSegment(sketch, "E367.MirrorCS", {"start": v(250, 513.84) * mm, "end": v(320, 473.43) * mm});
            skLineSegment(sketch, "E368.MirrorCS", {"start": v(570, 594.67) * mm, "end": v(570, 513.84) * mm});
            skLineSegment(sketch, "E369.MirrorCS", {"start": v(1030, 513.84) * mm, "end": v(1030, 594.67) * mm});
            skLineSegment(sketch, "E370.MirrorCS", {"start": v(-90, 594.67) * mm, "end": v(-90, 513.84) * mm});
            skLineSegment(sketch, "E371.MirrorCS", {"start": v(550, 594.67) * mm, "end": v(550, 513.84) * mm});
            skLineSegment(sketch, "E372.MirrorCS", {"start": v(960, 357.96) * mm, "end": v(1030, 317.54) * mm});
            skLineSegment(sketch, "E373.MirrorCS", {"start": v(80, 496.52) * mm, "end": v(150, 456.1) * mm});
            skLineSegment(sketch, "E374.MirrorCS", {"start": v(-640, 473.43) * mm, "end": v(-570, 513.84) * mm});
            skLineSegment(sketch, "E375.MirrorCS", {"start": v(-160, 473.43) * mm, "end": v(-230, 513.84) * mm});
            skLineSegment(sketch, "E376.MirrorCS", {"start": v(-320, 357.96) * mm, "end": v(-250, 317.54) * mm});
            skLineSegment(sketch, "E377.MirrorCS", {"start": v(1190, 340.64) * mm, "end": v(1130, 375.28) * mm});
            skLineSegment(sketch, "E378.MirrorCS", {"start": v(1130, 456.1) * mm, "end": v(1190, 490.75) * mm});
            skLineSegment(sketch, "E379.MirrorCS", {"start": v(640, 635.09) * mm, "end": v(570, 594.67) * mm});
            skLineSegment(sketch, "E380.MirrorCS", {"start": v(-650, 375.28) * mm, "end": v(-720, 334.86) * mm});
            skLineSegment(sketch, "E381.MirrorCS", {"start": v(-410, 317.54) * mm, "end": v(-480, 357.96) * mm});
            skLineSegment(sketch, "E382.MirrorCS", {"start": v(-550, 594.67) * mm, "end": v(-480, 635.09) * mm});
            skLineSegment(sketch, "E383.MirrorCS", {"start": v(-400, 496.52) * mm, "end": v(-470, 456.1) * mm});
            skLineSegment(sketch, "E384.MirrorCS", {"start": v(550, 513.84) * mm, "end": v(480, 473.43) * mm});
            skLineSegment(sketch, "E385.MirrorCS", {"start": v(150, 456.1) * mm, "end": v(150, 375.28) * mm});
            skLineSegment(sketch, "E386.MirrorCS", {"start": v(330, 375.28) * mm, "end": v(400, 334.86) * mm});
            skLineSegment(sketch, "E387.MirrorCS", {"start": v(-720, 496.52) * mm, "end": v(-650, 456.1) * mm});
            skLineSegment(sketch, "E388.MirrorCS", {"start": v(490, 456.1) * mm, "end": v(560, 496.52) * mm});
            skLineSegment(sketch, "E389.MirrorCS", {"start": v(800, 635.09) * mm, "end": v(870, 594.67) * mm});
            skLineSegment(sketch, "E390.MirrorCS", {"start": v(-240, 496.52) * mm, "end": v(-310, 456.1) * mm});
            skLineSegment(sketch, "E391.MirrorCS", {"start": v(-230, 594.67) * mm, "end": v(-160, 635.09) * mm});
            skLineSegment(sketch, "E392.MirrorCS", {"start": v(1190, 513.84) * mm, "end": v(1120, 473.43) * mm});
            skLineSegment(sketch, "E393.MirrorCS", {"start": v(720, 496.52) * mm, "end": v(790, 456.1) * mm});
            skLineSegment(sketch, "E394.MirrorCS", {"start": v(-390, 594.67) * mm, "end": v(-390, 513.84) * mm});
            skLineSegment(sketch, "E395.MirrorCS", {"start": v(-630, 375.28) * mm, "end": v(-630, 456.1) * mm});
            skLineSegment(sketch, "E396.MirrorCS", {"start": v(730, 594.67) * mm, "end": v(800, 635.09) * mm});
            skLineSegment(sketch, "E397.MirrorCS", {"start": v(-90, 317.54) * mm, "end": v(-160, 357.96) * mm});
            skLineSegment(sketch, "E398.MirrorCS", {"start": v(480, 357.96) * mm, "end": v(410, 317.54) * mm});
            skLineSegment(sketch, "E399.MirrorCS", {"start": v(390, 594.67) * mm, "end": v(320, 635.09) * mm});
            skLineSegment(sketch, "E400.MirrorCS", {"start": v(10, 456.1) * mm, "end": v(80, 496.52) * mm});
            skLineSegment(sketch, "E401.MirrorCS", {"start": v(890, 317.54) * mm, "end": v(960, 357.96) * mm});
            skLineSegment(sketch, "E402.MirrorCS", {"start": v(650, 375.28) * mm, "end": v(720, 334.86) * mm});
            skLineSegment(sketch, "E403.MirrorCS", {"start": v(490, 375.28) * mm, "end": v(560, 334.86) * mm});
            skLineSegment(sketch, "E404.MirrorCS", {"start": v(560, 496.52) * mm, "end": v(630, 456.1) * mm});
            skLineSegment(sketch, "E405.MirrorCS", {"start": v(-330, 456.1) * mm, "end": v(-400, 496.52) * mm});
            skLineSegment(sketch, "E406.MirrorCS", {"start": v(1190, 317.54) * mm, "end": v(1120, 357.96) * mm});
            skLineSegment(sketch, "E407.MirrorCS", {"start": v(70, 513.84) * mm, "end": v(70, 594.67) * mm});
            skLineSegment(sketch, "E408.MirrorCS", {"start": v(-410, 513.84) * mm, "end": v(-480, 473.43) * mm});
            skLineSegment(sketch, "E409.MirrorCS", {"start": v(-80, 334.86) * mm, "end": v(-150, 375.28) * mm});
            skLineSegment(sketch, "E410.MirrorCS", {"start": v(-390, 317.54) * mm, "end": v(-320, 357.96) * mm});
            skLineSegment(sketch, "E411.MirrorCS", {"start": v(1050, 594.67) * mm, "end": v(1120, 635.09) * mm});
            skLineSegment(sketch, "E412.MirrorCS", {"start": v(890, 513.84) * mm, "end": v(960, 473.43) * mm});
            skLineSegment(sketch, "E413.MirrorCS", {"start": v(150, 375.28) * mm, "end": v(80, 334.86) * mm});
            skLineSegment(sketch, "E414.MirrorCS", {"start": v(640, 473.43) * mm, "end": v(710, 513.84) * mm});
            skLineSegment(sketch, "E415.MirrorCS", {"start": v(-630, 456.1) * mm, "end": v(-560, 496.52) * mm});
            skLineSegment(sketch, "E416.MirrorCS", {"start": v(790, 456.1) * mm, "end": v(790, 375.28) * mm});
            skLineSegment(sketch, "E417.MirrorCS", {"start": v(-160, 357.96) * mm, "end": v(-230, 317.54) * mm});
            skLineSegment(sketch, "E418.MirrorCS", {"start": v(310, 375.28) * mm, "end": v(310, 456.1) * mm});
            skLineSegment(sketch, "E419.MirrorCS", {"start": v(-150, 456.1) * mm, "end": v(-80, 496.52) * mm});
            skLineSegment(sketch, "E420.MirrorCS", {"start": v(1110, 375.28) * mm, "end": v(1040, 334.86) * mm});
            skLineSegment(sketch, "E421.MirrorCS", {"start": v(550, 317.54) * mm, "end": v(480, 357.96) * mm});
            skLineSegment(sketch, "E422.MirrorCS", {"start": v(-650, 456.1) * mm, "end": v(-650, 375.28) * mm});
            skLineSegment(sketch, "E423.MirrorCS", {"start": v(880, 496.52) * mm, "end": v(810, 456.1) * mm});
            skLineSegment(sketch, "E424.MirrorCS", {"start": v(-640, 357.96) * mm, "end": v(-570, 317.54) * mm});
            skLineSegment(sketch, "E425.MirrorCS", {"start": v(330, 456.1) * mm, "end": v(330, 375.28) * mm});
            skLineSegment(sketch, "E426.MirrorCS", {"start": v(410, 513.84) * mm, "end": v(410, 594.67) * mm});
            skLineSegment(sketch, "E427.MirrorCS", {"start": v(960, 635.09) * mm, "end": v(890, 594.67) * mm});
            skLineSegment(sketch, "E428.MirrorCS", {"start": v(240, 496.52) * mm, "end": v(170, 456.1) * mm});
            skLineSegment(sketch, "E429.MirrorCS", {"start": v(230, 317.54) * mm, "end": v(160, 357.96) * mm});
            skLineSegment(sketch, "E430.MirrorCS", {"start": v(710, 513.84) * mm, "end": v(710, 594.67) * mm});
            skLineSegment(sketch, "E431.MirrorCS", {"start": v(-640, 635.09) * mm, "end": v(-710, 594.67) * mm});
            skLineSegment(sketch, "E432.MirrorCS", {"start": v(1120, 473.43) * mm, "end": v(1050, 513.84) * mm});
            skLineSegment(sketch, "E433.MirrorCS", {"start": v(480, 473.43) * mm, "end": v(410, 513.84) * mm});
            skLineSegment(sketch, "E434.MirrorCS", {"start": v(-710, 513.84) * mm, "end": v(-640, 473.43) * mm});
            skLineSegment(sketch, "E435.MirrorCS", {"start": v(630, 456.1) * mm, "end": v(630, 375.28) * mm});
            skLineSegment(sketch, "E436.MirrorCS", {"start": v(650, 456.1) * mm, "end": v(720, 496.52) * mm});
            skLineSegment(sketch, "E437.MirrorCS", {"start": v(950, 456.1) * mm, "end": v(880, 496.52) * mm});
            skLineSegment(sketch, "E438.MirrorCS", {"start": v(-230, 513.84) * mm, "end": v(-230, 594.67) * mm});
            skLineSegment(sketch, "E439.MirrorCS", {"start": v(1110, 456.1) * mm, "end": v(1040, 496.52) * mm});
            skLineSegment(sketch, "E440.MirrorCS", {"start": v(400, 334.86) * mm, "end": v(470, 375.28) * mm});
            skLineSegment(sketch, "E441.MirrorCS", {"start": v(400, 496.52) * mm, "end": v(330, 456.1) * mm});
            skLineSegment(sketch, "E442.MirrorCS", {"start": v(-410, 594.67) * mm, "end": v(-410, 513.84) * mm});
            skLineSegment(sketch, "E443.MirrorCS", {"start": v(1130, 733.23) * mm, "end": v(1190, 767.88) * mm});
            skLineSegment(sketch, "E444.MirrorCS", {"start": v(320, 750.56) * mm, "end": v(250, 790.97) * mm});
            skLineSegment(sketch, "E445.MirrorCS", {"start": v(950, 733.23) * mm, "end": v(880, 773.65) * mm});
            skLineSegment(sketch, "E446.MirrorCS", {"start": v(-400, 773.65) * mm, "end": v(-470, 733.23) * mm});
            skLineSegment(sketch, "E447.MirrorCS", {"start": v(10, 733.23) * mm, "end": v(80, 773.65) * mm});
            skLineSegment(sketch, "E448.MirrorCS", {"start": v(150, 733.23) * mm, "end": v(80, 773.65) * mm});
            skLineSegment(sketch, "E449.MirrorCS", {"start": v(80, 889.12) * mm, "end": v(150, 929.53) * mm});
            skLineSegment(sketch, "E450.MirrorCS", {"start": v(560, 773.65) * mm, "end": v(630, 733.23) * mm});
            skLineSegment(sketch, "E451.MirrorCS", {"start": v(1190, 790.97) * mm, "end": v(1120, 750.56) * mm});
            skLineSegment(sketch, "E452.MirrorCS", {"start": v(720, 889.12) * mm, "end": v(790, 929.53) * mm});
            skLineSegment(sketch, "E453.MirrorCS", {"start": v(1110, 733.23) * mm, "end": v(1040, 773.65) * mm});
            skLineSegment(sketch, "E454.MirrorCS", {"start": v(-650, 733.23) * mm, "end": v(-720, 773.65) * mm});
            skLineSegment(sketch, "E455.MirrorCS", {"start": v(550, 790.97) * mm, "end": v(480, 750.56) * mm});
            skLineSegment(sketch, "E456.MirrorCS", {"start": v(490, 733.23) * mm, "end": v(560, 773.65) * mm});
            skLineSegment(sketch, "E457.MirrorCS", {"start": v(0, 750.56) * mm, "end": v(70, 790.97) * mm});
            skLineSegment(sketch, "E458.MirrorCS", {"start": v(810, 733.23) * mm, "end": v(880, 773.65) * mm});
            skLineSegment(sketch, "E459.MirrorCS", {"start": v(10, 929.53) * mm, "end": v(80, 889.12) * mm});
            skLineSegment(sketch, "E460.MirrorCS", {"start": v(-80, 889.12) * mm, "end": v(-10, 929.53) * mm});
            skLineSegment(sketch, "E461.MirrorCS", {"start": v(640, 750.56) * mm, "end": v(710, 790.97) * mm});
            skLineSegment(sketch, "E462.MirrorCS", {"start": v(-80, 773.65) * mm, "end": v(-150, 733.23) * mm});
            skLineSegment(sketch, "E463.MirrorCS", {"start": v(-70, 790.97) * mm, "end": v(0, 750.56) * mm});
            skLineSegment(sketch, "E464.MirrorCS", {"start": v(320, 750.56) * mm, "end": v(390, 790.97) * mm});
            skLineSegment(sketch, "E465.MirrorCS", {"start": v(-70, 1068.1) * mm, "end": v(0, 1027.68) * mm});
            skLineSegment(sketch, "E466.MirrorCS", {"start": v(870, 790.97) * mm, "end": v(800, 750.56) * mm});
            skLineSegment(sketch, "E467.MirrorCS", {"start": v(400, 773.65) * mm, "end": v(330, 733.23) * mm});
            skLineSegment(sketch, "E468.MirrorCS", {"start": v(1040, 889.12) * mm, "end": v(970, 929.53) * mm});
            skLineSegment(sketch, "E469.MirrorCS", {"start": v(-630, 929.53) * mm, "end": v(-560, 889.12) * mm});
            skLineSegment(sketch, "E470.MirrorCS", {"start": v(480, 750.56) * mm, "end": v(410, 790.97) * mm});
            skLineSegment(sketch, "E471.MirrorCS", {"start": v(1040, 889.12) * mm, "end": v(1110, 929.53) * mm});
            skLineSegment(sketch, "E472.MirrorCS", {"start": v(0, 1027.68) * mm, "end": v(70, 1068.1) * mm});
            skLineSegment(sketch, "E473.MirrorCS", {"start": v(-240, 889.12) * mm, "end": v(-310, 929.53) * mm});
            skLineSegment(sketch, "E474.MirrorCS", {"start": v(-720, 773.65) * mm, "end": v(-790, 733.23) * mm});
            skLineSegment(sketch, "E475.MirrorCS", {"start": v(470, 929.53) * mm, "end": v(400, 889.12) * mm});
            skLineSegment(sketch, "E476.MirrorCS", {"start": v(-320, 750.56) * mm, "end": v(-250, 790.97) * mm});
            skLineSegment(sketch, "E477.MirrorCS", {"start": v(960, 750.56) * mm, "end": v(1030, 790.97) * mm});
            skLineSegment(sketch, "E478.MirrorCS", {"start": v(790, 733.23) * mm, "end": v(720, 773.65) * mm});
            skLineSegment(sketch, "E479.MirrorCS", {"start": v(-410, 790.97) * mm, "end": v(-480, 750.56) * mm});
            skLineSegment(sketch, "E480.MirrorCS", {"start": v(-150, 929.53) * mm, "end": v(-80, 889.12) * mm});
            skLineSegment(sketch, "E481.MirrorCS", {"start": v(650, 733.23) * mm, "end": v(720, 773.65) * mm});
            skLineSegment(sketch, "E482.MirrorCS", {"start": v(960, 750.56) * mm, "end": v(890, 790.97) * mm});
            skLineSegment(sketch, "E483.MirrorCS", {"start": v(-240, 773.65) * mm, "end": v(-170, 733.23) * mm});
            skLineSegment(sketch, "E484.MirrorCS", {"start": v(-560, 889.12) * mm, "end": v(-490, 929.53) * mm});
            skLineSegment(sketch, "E485.MirrorCS", {"start": v(310, 929.53) * mm, "end": v(240, 889.12) * mm});
            skLineSegment(sketch, "E486.MirrorCS", {"start": v(-640, 750.56) * mm, "end": v(-570, 790.97) * mm});
            skLineSegment(sketch, "E487.MirrorCS", {"start": v(720, 889.12) * mm, "end": v(650, 929.53) * mm});
            skLineSegment(sketch, "E488.MirrorCS", {"start": v(880, 889.12) * mm, "end": v(810, 929.53) * mm});
            skLineSegment(sketch, "E489.MirrorCS", {"start": v(560, 889.12) * mm, "end": v(490, 929.53) * mm});
            skLineSegment(sketch, "E490.MirrorCS", {"start": v(560, 889.12) * mm, "end": v(630, 929.53) * mm});
            skLineSegment(sketch, "E491.MirrorCS", {"start": v(-390, 790.97) * mm, "end": v(-320, 750.56) * mm});
            skLineSegment(sketch, "E492.MirrorCS", {"start": v(-240, 889.12) * mm, "end": v(-170, 929.53) * mm});
            skLineSegment(sketch, "E493.MirrorCS", {"start": v(400, 889.12) * mm, "end": v(330, 929.53) * mm});
            skLineSegment(sketch, "E494.MirrorCS", {"start": v(-240, 773.65) * mm, "end": v(-310, 733.23) * mm});
            skLineSegment(sketch, "E495.MirrorCS", {"start": v(-160, 750.56) * mm, "end": v(-90, 790.97) * mm});
            skLineSegment(sketch, "E496.MirrorCS", {"start": v(-720, 889.12) * mm, "end": v(-650, 929.53) * mm});
            skLineSegment(sketch, "E497.MirrorCS", {"start": v(90, 790.97) * mm, "end": v(160, 750.56) * mm});
            skLineSegment(sketch, "E498.MirrorCS", {"start": v(-560, 773.65) * mm, "end": v(-490, 733.23) * mm});
            skLineSegment(sketch, "E499.MirrorCS", {"start": v(-560, 773.65) * mm, "end": v(-630, 733.23) * mm});
            skLineSegment(sketch, "E500.MirrorCS", {"start": v(0, 1189.34) * mm, "end": v(-70, 1148.93) * mm});
            skLineSegment(sketch, "E501.MirrorCS", {"start": v(-550, 790.97) * mm, "end": v(-480, 750.56) * mm});
            skLineSegment(sketch, "E502.MirrorCS", {"start": v(240, 773.65) * mm, "end": v(170, 733.23) * mm});
            skLineSegment(sketch, "E503.MirrorCS", {"start": v(170, 929.53) * mm, "end": v(240, 889.12) * mm});
            skLineSegment(sketch, "E504.MirrorCS", {"start": v(800, 750.56) * mm, "end": v(730, 790.97) * mm});
            skLineSegment(sketch, "E505.MirrorCS", {"start": v(-330, 733.23) * mm, "end": v(-400, 773.65) * mm});
            skLineSegment(sketch, "E506.MirrorCS", {"start": v(-160, 750.56) * mm, "end": v(-230, 790.97) * mm});
            skLineSegment(sketch, "E507.MirrorCS", {"start": v(950, 929.53) * mm, "end": v(880, 889.12) * mm});
            skLineSegment(sketch, "E508.MirrorCS", {"start": v(-10, 733.23) * mm, "end": v(-80, 773.65) * mm});
            skLineSegment(sketch, "E509.MirrorCS", {"start": v(-470, 929.53) * mm, "end": v(-400, 889.12) * mm});
            skLineSegment(sketch, "E510.MirrorCS", {"start": v(1130, 929.53) * mm, "end": v(1190, 894.9) * mm});
            skLineSegment(sketch, "E511.MirrorCS", {"start": v(-330, 929.53) * mm, "end": v(-400, 889.12) * mm});
            skLineSegment(sketch, "E512.MirrorCS", {"start": v(570, 790.97) * mm, "end": v(640, 750.56) * mm});
            skLineSegment(sketch, "E513.MirrorCS", {"start": v(310, 733.23) * mm, "end": v(240, 773.65) * mm});
            skLineSegment(sketch, "E514.MirrorCS", {"start": v(970, 733.23) * mm, "end": v(1040, 773.65) * mm});
            skLineSegment(sketch, "E515.MirrorCS", {"start": v(230, 790.97) * mm, "end": v(160, 750.56) * mm});
            skLineSegment(sketch, "E516.MirrorCS", {"start": v(1120, 750.56) * mm, "end": v(1050, 790.97) * mm});
            skLineSegment(sketch, "E517.MirrorCS", {"start": v(-640, 750.56) * mm, "end": v(-710, 790.97) * mm});
            skLineSegment(sketch, "E518.MirrorCS", {"start": v(470, 733.23) * mm, "end": v(400, 773.65) * mm});
            skLineSegment(sketch, "E519.MirrorCS", {"start": v(-720, 889.12) * mm, "end": v(-790, 929.53) * mm});
            skLineSegment(sketch, "E520.MirrorCS", {"start": v(550, 790.97) * mm, "end": v(550, 871.8) * mm});
            skLineSegment(sketch, "E521.MirrorCS", {"start": v(570, 790.97) * mm, "end": v(570, 871.8) * mm});
            skLineSegment(sketch, "E522.MirrorCS", {"start": v(310, 929.53) * mm, "end": v(310, 1010.36) * mm});
            skLineSegment(sketch, "E523.MirrorCS", {"start": v(-170, 929.53) * mm, "end": v(-240, 889.12) * mm});
            skLineSegment(sketch, "E524.MirrorCS", {"start": v(880, 773.65) * mm, "end": v(950, 733.23) * mm});
            skLineSegment(sketch, "E525.MirrorCS", {"start": v(710, 790.97) * mm, "end": v(640, 750.56) * mm});
            skLineSegment(sketch, "E526.MirrorCS", {"start": v(250, 1068.1) * mm, "end": v(320, 1027.68) * mm});
            skLineSegment(sketch, "E527.MirrorCS", {"start": v(870, 871.8) * mm, "end": v(800, 912.21) * mm});
            skLineSegment(sketch, "E528.MirrorCS", {"start": v(800, 750.56) * mm, "end": v(870, 790.97) * mm});
            skLineSegment(sketch, "E529.MirrorCS", {"start": v(490, 929.53) * mm, "end": v(490, 1010.36) * mm});
            skLineSegment(sketch, "E530.MirrorCS", {"start": v(-90, 594.67) * mm, "end": v(-160, 635.09) * mm});
            skLineSegment(sketch, "E531.MirrorCS", {"start": v(-560, 1050.78) * mm, "end": v(-490, 1010.36) * mm});
            skLineSegment(sketch, "E532.MirrorCS", {"start": v(-150, 652.4) * mm, "end": v(-80, 612) * mm});
            skLineSegment(sketch, "E533.MirrorCS", {"start": v(70, 1068.1) * mm, "end": v(70, 1148.93) * mm});
            skLineSegment(sketch, "E534.MirrorCS", {"start": v(630, 733.23) * mm, "end": v(560, 773.65) * mm});
            skLineSegment(sketch, "E535.MirrorCS", {"start": v(-790, 733.23) * mm, "end": v(-790, 652.4) * mm});
            skLineSegment(sketch, "E536.MirrorCS", {"start": v(320, 912.21) * mm, "end": v(390, 871.8) * mm});
            skLineSegment(sketch, "E537.MirrorCS", {"start": v(470, 929.53) * mm, "end": v(470, 1010.36) * mm});
            skLineSegment(sketch, "E538.MirrorCS", {"start": v(-80, 773.65) * mm, "end": v(-10, 733.23) * mm});
            skLineSegment(sketch, "E539.MirrorCS", {"start": v(-170, 733.23) * mm, "end": v(-170, 652.4) * mm});
            skLineSegment(sketch, "E540.MirrorCS", {"start": v(230, 1148.93) * mm, "end": v(230, 1068.1) * mm});
            skLineSegment(sketch, "E541.MirrorCS", {"start": v(-490, 652.4) * mm, "end": v(-490, 733.23) * mm});
            skLineSegment(sketch, "E542.MirrorCS", {"start": v(-90, 1068.1) * mm, "end": v(-160, 1027.68) * mm});
            skLineSegment(sketch, "E543.MirrorCS", {"start": v(-480, 750.56) * mm, "end": v(-550, 790.97) * mm});
            skLineSegment(sketch, "E544.MirrorCS", {"start": v(-390, 1148.93) * mm, "end": v(-390, 1068.1) * mm});
            skLineSegment(sketch, "E545.MirrorCS", {"start": v(-640, 1189.34) * mm, "end": v(-710, 1148.93) * mm});
            skLineSegment(sketch, "E546.MirrorCS", {"start": v(1030, 790.97) * mm, "end": v(960, 750.56) * mm});
            skLineSegment(sketch, "E547.MirrorCS", {"start": v(70, 1148.93) * mm, "end": v(0, 1189.34) * mm});
            skLineSegment(sketch, "E548.MirrorCS", {"start": v(-490, 733.23) * mm, "end": v(-560, 773.65) * mm});
            skLineSegment(sketch, "E549.MirrorCS", {"start": v(-160, 1189.34) * mm, "end": v(-90, 1148.93) * mm});
            skLineSegment(sketch, "E550.MirrorCS", {"start": v(880, 773.65) * mm, "end": v(810, 733.23) * mm});
            skLineSegment(sketch, "E551.MirrorCS", {"start": v(-720, 1050.78) * mm, "end": v(-650, 1010.36) * mm});
            skLineSegment(sketch, "E552.MirrorCS", {"start": v(1110, 929.53) * mm, "end": v(1110, 1010.36) * mm});
            skLineSegment(sketch, "E553.MirrorCS", {"start": v(810, 652.4) * mm, "end": v(810, 733.23) * mm});
            skLineSegment(sketch, "E554.MirrorCS", {"start": v(1130, 652.4) * mm, "end": v(1190, 617.76) * mm});
            skLineSegment(sketch, "E555.MirrorCS", {"start": v(-400, 1050.78) * mm, "end": v(-470, 1010.36) * mm});
            skLineSegment(sketch, "E556.MirrorCS", {"start": v(80, 612) * mm, "end": v(150, 652.4) * mm});
            skLineSegment(sketch, "E557.MirrorCS", {"start": v(-10, 652.4) * mm, "end": v(-10, 733.23) * mm});
            skLineSegment(sketch, "E558.MirrorCS", {"start": v(-90, 790.97) * mm, "end": v(-160, 750.56) * mm});
            skLineSegment(sketch, "E559.MirrorCS", {"start": v(1030, 1068.1) * mm, "end": v(1030, 1148.93) * mm});
            skLineSegment(sketch, "E560.MirrorCS", {"start": v(-150, 733.23) * mm, "end": v(-80, 773.65) * mm});
            skLineSegment(sketch, "E561.MirrorCS", {"start": v(390, 1068.1) * mm, "end": v(390, 1148.93) * mm});
            skLineSegment(sketch, "E562.MirrorCS", {"start": v(570, 1068.1) * mm, "end": v(640, 1027.68) * mm});
            skLineSegment(sketch, "E563.MirrorCS", {"start": v(570, 871.8) * mm, "end": v(640, 912.21) * mm});
            skLineSegment(sketch, "E564.MirrorCS", {"start": v(150, 929.53) * mm, "end": v(80, 889.12) * mm});
            skLineSegment(sketch, "E565.MirrorCS", {"start": v(1190, 894.9) * mm, "end": v(1130, 929.53) * mm});
            skLineSegment(sketch, "E566.MirrorCS", {"start": v(800, 635.09) * mm, "end": v(730, 594.67) * mm});
            skLineSegment(sketch, "E567.MirrorCS", {"start": v(-400, 889.12) * mm, "end": v(-330, 929.53) * mm});
            skLineSegment(sketch, "E568.MirrorCS", {"start": v(800, 1189.34) * mm, "end": v(870, 1148.93) * mm});
            skLineSegment(sketch, "E569.MirrorCS", {"start": v(1120, 1189.34) * mm, "end": v(1190, 1148.93) * mm});
            skLineSegment(sketch, "E570.MirrorCS", {"start": v(1190, 767.88) * mm, "end": v(1130, 733.23) * mm});
            skLineSegment(sketch, "E571.MirrorCS", {"start": v(720, 773.65) * mm, "end": v(650, 733.23) * mm});
            skLineSegment(sketch, "E572.MirrorCS", {"start": v(-470, 733.23) * mm, "end": v(-400, 773.65) * mm});
            skLineSegment(sketch, "E573.MirrorCS", {"start": v(170, 733.23) * mm, "end": v(240, 773.65) * mm});
            skLineSegment(sketch, "E574.MirrorCS", {"start": v(320, 1189.34) * mm, "end": v(250, 1148.93) * mm});
            skLineSegment(sketch, "E575.MirrorCS", {"start": v(1190, 594.67) * mm, "end": v(1120, 635.09) * mm});
            skLineSegment(sketch, "E576.MirrorCS", {"start": v(640, 750.56) * mm, "end": v(570, 790.97) * mm});
            skLineSegment(sketch, "E577.MirrorCS", {"start": v(1110, 1010.36) * mm, "end": v(1040, 1050.78) * mm});
            skLineSegment(sketch, "E578.MirrorCS", {"start": v(-320, 1189.34) * mm, "end": v(-390, 1148.93) * mm});
            skLineSegment(sketch, "E579.MirrorCS", {"start": v(550, 1148.93) * mm, "end": v(550, 1068.1) * mm});
            skLineSegment(sketch, "E580.MirrorCS", {"start": v(310, 652.4) * mm, "end": v(240, 612) * mm});
            skLineSegment(sketch, "E581.MirrorCS", {"start": v(250, 1148.93) * mm, "end": v(250, 1068.1) * mm});
            skLineSegment(sketch, "E582.MirrorCS", {"start": v(-320, 1027.68) * mm, "end": v(-250, 1068.1) * mm});
            skLineSegment(sketch, "E583.MirrorCS", {"start": v(880, 1050.78) * mm, "end": v(810, 1010.36) * mm});
            skLineSegment(sketch, "E584.MirrorCS", {"start": v(470, 1010.36) * mm, "end": v(400, 1050.78) * mm});
            skLineSegment(sketch, "E585.MirrorCS", {"start": v(640, 1189.34) * mm, "end": v(570, 1148.93) * mm});
            skLineSegment(sketch, "E586.MirrorCS", {"start": v(400, 612) * mm, "end": v(330, 652.4) * mm});
            skLineSegment(sketch, "E587.MirrorCS", {"start": v(250, 790.97) * mm, "end": v(320, 750.56) * mm});
            skLineSegment(sketch, "E588.MirrorCS", {"start": v(-710, 1068.1) * mm, "end": v(-640, 1027.68) * mm});
            skLineSegment(sketch, "E589.MirrorCS", {"start": v(560, 1050.78) * mm, "end": v(630, 1010.36) * mm});
            skLineSegment(sketch, "E590.MirrorCS", {"start": v(-10, 929.53) * mm, "end": v(-80, 889.12) * mm});
            skLineSegment(sketch, "E591.MirrorCS", {"start": v(890, 1148.93) * mm, "end": v(890, 1068.1) * mm});
            skLineSegment(sketch, "E592.MirrorCS", {"start": v(-710, 1148.93) * mm, "end": v(-710, 1068.1) * mm});
            skLineSegment(sketch, "E593.MirrorCS", {"start": v(-70, 1148.93) * mm, "end": v(-70, 1068.1) * mm});
            skLineSegment(sketch, "E594.MirrorCS", {"start": v(240, 773.65) * mm, "end": v(310, 733.23) * mm});
            skLineSegment(sketch, "E595.MirrorCS", {"start": v(-310, 1010.36) * mm, "end": v(-310, 929.53) * mm});
            skLineSegment(sketch, "E596.MirrorCS", {"start": v(-250, 1068.1) * mm, "end": v(-250, 1148.93) * mm});
            skLineSegment(sketch, "E597.MirrorCS", {"start": v(640, 635.09) * mm, "end": v(710, 594.67) * mm});
            skLineSegment(sketch, "E598.MirrorCS", {"start": v(400, 773.65) * mm, "end": v(470, 733.23) * mm});
            skLineSegment(sketch, "E599.MirrorCS", {"start": v(-720, 773.65) * mm, "end": v(-650, 733.23) * mm});
            skLineSegment(sketch, "E600.MirrorCS", {"start": v(330, 929.53) * mm, "end": v(400, 889.12) * mm});
            skLineSegment(sketch, "E601.MirrorCS", {"start": v(1050, 1068.1) * mm, "end": v(1050, 1148.93) * mm});
            skLineSegment(sketch, "E602.MirrorCS", {"start": v(10, 733.23) * mm, "end": v(10, 652.4) * mm});
            skLineSegment(sketch, "E603.MirrorCS", {"start": v(-90, 790.97) * mm, "end": v(-90, 871.8) * mm});
            skLineSegment(sketch, "E604.MirrorCS", {"start": v(90, 1068.1) * mm, "end": v(90, 1148.93) * mm});
            skLineSegment(sketch, "E605.MirrorCS", {"start": v(70, 790.97) * mm, "end": v(0, 750.56) * mm});
            skLineSegment(sketch, "E606.MirrorCS", {"start": v(1050, 790.97) * mm, "end": v(1120, 750.56) * mm});
            skLineSegment(sketch, "E607.MirrorCS", {"start": v(-790, 733.23) * mm, "end": v(-720, 773.65) * mm});
            skLineSegment(sketch, "E608.MirrorCS", {"start": v(160, 912.21) * mm, "end": v(90, 871.8) * mm});
            skLineSegment(sketch, "E609.MirrorCS", {"start": v(-640, 1027.68) * mm, "end": v(-570, 1068.1) * mm});
            skLineSegment(sketch, "E610.MirrorCS", {"start": v(710, 1148.93) * mm, "end": v(640, 1189.34) * mm});
            skLineSegment(sketch, "E611.MirrorCS", {"start": v(1110, 652.4) * mm, "end": v(1040, 612) * mm});
            skLineSegment(sketch, "E612.MirrorCS", {"start": v(-650, 1010.36) * mm, "end": v(-650, 929.53) * mm});
            skLineSegment(sketch, "E613.MirrorCS", {"start": v(720, 1050.78) * mm, "end": v(790, 1010.36) * mm});
            skLineSegment(sketch, "E614.MirrorCS", {"start": v(-410, 790.97) * mm, "end": v(-410, 871.8) * mm});
            skLineSegment(sketch, "E615.MirrorCS", {"start": v(-720, 612) * mm, "end": v(-650, 652.4) * mm});
            skLineSegment(sketch, "E616.MirrorCS", {"start": v(-480, 1027.68) * mm, "end": v(-550, 1068.1) * mm});
            skLineSegment(sketch, "E617.MirrorCS", {"start": v(10, 1010.36) * mm, "end": v(80, 1050.78) * mm});
            skLineSegment(sketch, "E618.MirrorCS", {"start": v(150, 1010.36) * mm, "end": v(150, 929.53) * mm});
            skLineSegment(sketch, "E619.MirrorCS", {"start": v(720, 612) * mm, "end": v(790, 652.4) * mm});
            skLineSegment(sketch, "E620.MirrorCS", {"start": v(-560, 889.12) * mm, "end": v(-630, 929.53) * mm});
            skLineSegment(sketch, "E621.MirrorCS", {"start": v(-390, 594.67) * mm, "end": v(-320, 635.09) * mm});
            skLineSegment(sketch, "E622.MirrorCS", {"start": v(-480, 1189.34) * mm, "end": v(-410, 1148.93) * mm});
            skLineSegment(sketch, "E623.MirrorCS", {"start": v(790, 929.53) * mm, "end": v(720, 889.12) * mm});
            skLineSegment(sketch, "E624.MirrorCS", {"start": v(400, 1050.78) * mm, "end": v(330, 1010.36) * mm});
            skLineSegment(sketch, "E625.MirrorCS", {"start": v(230, 594.67) * mm, "end": v(160, 635.09) * mm});
            skLineSegment(sketch, "E626.MirrorCS", {"start": v(1130, 1010.36) * mm, "end": v(1190, 1045) * mm});
            skLineSegment(sketch, "E627.MirrorCS", {"start": v(-470, 1010.36) * mm, "end": v(-470, 929.53) * mm});
            skLineSegment(sketch, "E628.MirrorCS", {"start": v(90, 1148.93) * mm, "end": v(160, 1189.34) * mm});
            skLineSegment(sketch, "E629.MirrorCS", {"start": v(1120, 912.21) * mm, "end": v(1050, 871.8) * mm});
            skLineSegment(sketch, "E630.MirrorCS", {"start": v(310, 1010.36) * mm, "end": v(240, 1050.78) * mm});
            skLineSegment(sketch, "E631.MirrorCS", {"start": v(890, 1068.1) * mm, "end": v(960, 1027.68) * mm});
            skLineSegment(sketch, "E632.MirrorCS", {"start": v(-480, 750.56) * mm, "end": v(-410, 790.97) * mm});
            skLineSegment(sketch, "E633.MirrorCS", {"start": v(950, 733.23) * mm, "end": v(950, 652.4) * mm});
            skLineSegment(sketch, "E634.MirrorCS", {"start": v(-470, 652.4) * mm, "end": v(-470, 733.23) * mm});
            skLineSegment(sketch, "E635.MirrorCS", {"start": v(-570, 1068.1) * mm, "end": v(-570, 1148.93) * mm});
            skLineSegment(sketch, "E636.MirrorCS", {"start": v(-650, 652.4) * mm, "end": v(-650, 733.23) * mm});
            skLineSegment(sketch, "E637.MirrorCS", {"start": v(-230, 1068.1) * mm, "end": v(-230, 1148.93) * mm});
            skLineSegment(sketch, "E638.MirrorCS", {"start": v(1190, 1068.1) * mm, "end": v(1120, 1027.68) * mm});
            skLineSegment(sketch, "E639.MirrorCS", {"start": v(80, 773.65) * mm, "end": v(150, 733.23) * mm});
            skLineSegment(sketch, "E640.MirrorCS", {"start": v(90, 871.8) * mm, "end": v(90, 790.97) * mm});
            skLineSegment(sketch, "E641.MirrorCS", {"start": v(240, 889.12) * mm, "end": v(170, 929.53) * mm});
            skLineSegment(sketch, "E642.MirrorCS", {"start": v(570, 1148.93) * mm, "end": v(570, 1068.1) * mm});
            skLineSegment(sketch, "E643.MirrorCS", {"start": v(-480, 912.21) * mm, "end": v(-550, 871.8) * mm});
            skLineSegment(sketch, "E644.MirrorCS", {"start": v(730, 790.97) * mm, "end": v(800, 750.56) * mm});
            skLineSegment(sketch, "E645.MirrorCS", {"start": v(400, 889.12) * mm, "end": v(470, 929.53) * mm});
            skLineSegment(sketch, "E646.MirrorCS", {"start": v(320, 1027.68) * mm, "end": v(390, 1068.1) * mm});
            skLineSegment(sketch, "E647.MirrorCS", {"start": v(-480, 635.09) * mm, "end": v(-550, 594.67) * mm});
            skLineSegment(sketch, "E648.MirrorCS", {"start": v(-640, 912.21) * mm, "end": v(-570, 871.8) * mm});
            skLineSegment(sketch, "E649.MirrorCS", {"start": v(890, 790.97) * mm, "end": v(960, 750.56) * mm});
            skLineSegment(sketch, "E650.MirrorCS", {"start": v(650, 1010.36) * mm, "end": v(720, 1050.78) * mm});
            skLineSegment(sketch, "E651.MirrorCS", {"start": v(1130, 733.23) * mm, "end": v(1130, 652.4) * mm});
            skLineSegment(sketch, "E652.MirrorCS", {"start": v(160, 750.56) * mm, "end": v(90, 790.97) * mm});
            skLineSegment(sketch, "E653.MirrorCS", {"start": v(-70, 594.67) * mm, "end": v(0, 635.09) * mm});
            skLineSegment(sketch, "E654.MirrorCS", {"start": v(480, 1027.68) * mm, "end": v(410, 1068.1) * mm});
            skLineSegment(sketch, "E655.MirrorCS", {"start": v(560, 773.65) * mm, "end": v(490, 733.23) * mm});
            skLineSegment(sketch, "E656.MirrorCS", {"start": v(730, 1068.1) * mm, "end": v(730, 1148.93) * mm});
            skLineSegment(sketch, "E657.MirrorCS", {"start": v(1040, 1050.78) * mm, "end": v(970, 1010.36) * mm});
            skLineSegment(sketch, "E658.MirrorCS", {"start": v(-790, 652.4) * mm, "end": v(-720, 612) * mm});
            skLineSegment(sketch, "E659.MirrorCS", {"start": v(-570, 1148.93) * mm, "end": v(-640, 1189.34) * mm});
            skLineSegment(sketch, "E660.MirrorCS", {"start": v(650, 929.53) * mm, "end": v(720, 889.12) * mm});
            skLineSegment(sketch, "E661.MirrorCS", {"start": v(490, 929.53) * mm, "end": v(560, 889.12) * mm});
            skLineSegment(sketch, "E662.MirrorCS", {"start": v(890, 790.97) * mm, "end": v(890, 871.8) * mm});
            skLineSegment(sketch, "E663.MirrorCS", {"start": v(950, 652.4) * mm, "end": v(880, 612) * mm});
            skLineSegment(sketch, "E664.MirrorCS", {"start": v(-330, 652.4) * mm, "end": v(-400, 612) * mm});
            skLineSegment(sketch, "E665.MirrorCS", {"start": v(80, 773.65) * mm, "end": v(10, 733.23) * mm});
            skLineSegment(sketch, "E666.MirrorCS", {"start": v(160, 1027.68) * mm, "end": v(90, 1068.1) * mm});
            skLineSegment(sketch, "E667.MirrorCS", {"start": v(870, 594.67) * mm, "end": v(800, 635.09) * mm});
            skLineSegment(sketch, "E668.MirrorCS", {"start": v(640, 912.21) * mm, "end": v(710, 871.8) * mm});
            skLineSegment(sketch, "E669.MirrorCS", {"start": v(80, 1050.78) * mm, "end": v(150, 1010.36) * mm});
            skLineSegment(sketch, "E670.MirrorCS", {"start": v(0, 912.21) * mm, "end": v(70, 871.8) * mm});
            skLineSegment(sketch, "E671.MirrorCS", {"start": v(410, 1148.93) * mm, "end": v(480, 1189.34) * mm});
            skLineSegment(sketch, "E672.MirrorCS", {"start": v(-570, 871.8) * mm, "end": v(-570, 790.97) * mm});
            skLineSegment(sketch, "E673.MirrorCS", {"start": v(-170, 733.23) * mm, "end": v(-240, 773.65) * mm});
            skLineSegment(sketch, "E674.MirrorCS", {"start": v(-710, 790.97) * mm, "end": v(-710, 871.8) * mm});
            skLineSegment(sketch, "E675.MirrorCS", {"start": v(-630, 652.4) * mm, "end": v(-560, 612) * mm});
            skLineSegment(sketch, "E676.MirrorCS", {"start": v(-710, 594.67) * mm, "end": v(-640, 635.09) * mm});
            skLineSegment(sketch, "E677.MirrorCS", {"start": v(550, 1068.1) * mm, "end": v(480, 1027.68) * mm});
            skLineSegment(sketch, "E678.MirrorCS", {"start": v(1190, 871.8) * mm, "end": v(1120, 912.21) * mm});
            skLineSegment(sketch, "E679.MirrorCS", {"start": v(-80, 1050.78) * mm, "end": v(-10, 1010.36) * mm});
            skLineSegment(sketch, "E680.MirrorCS", {"start": v(-630, 1010.36) * mm, "end": v(-560, 1050.78) * mm});
            skLineSegment(sketch, "E681.MirrorCS", {"start": v(480, 1189.34) * mm, "end": v(550, 1148.93) * mm});
            skLineSegment(sketch, "E682.MirrorCS", {"start": v(1190, 790.97) * mm, "end": v(1190, 871.8) * mm});
            skLineSegment(sketch, "E683.MirrorCS", {"start": v(570, 594.67) * mm, "end": v(640, 635.09) * mm});
            skLineSegment(sketch, "E684.MirrorCS", {"start": v(490, 733.23) * mm, "end": v(490, 652.4) * mm});
            skLineSegment(sketch, "E685.MirrorCS", {"start": v(-330, 1010.36) * mm, "end": v(-400, 1050.78) * mm});
            skLineSegment(sketch, "E686.MirrorCS", {"start": v(650, 733.23) * mm, "end": v(650, 652.4) * mm});
            skLineSegment(sketch, "E687.MirrorCS", {"start": v(-10, 1010.36) * mm, "end": v(-10, 929.53) * mm});
            skLineSegment(sketch, "E688.MirrorCS", {"start": v(810, 929.53) * mm, "end": v(880, 889.12) * mm});
            skLineSegment(sketch, "E689.MirrorCS", {"start": v(1110, 929.53) * mm, "end": v(1040, 889.12) * mm});
            skLineSegment(sketch, "E690.MirrorCS", {"start": v(10, 929.53) * mm, "end": v(10, 1010.36) * mm});
            skLineSegment(sketch, "E691.MirrorCS", {"start": v(710, 871.8) * mm, "end": v(710, 790.97) * mm});
            skLineSegment(sketch, "E692.MirrorCS", {"start": v(870, 790.97) * mm, "end": v(870, 871.8) * mm});
            skLineSegment(sketch, "E693.MirrorCS", {"start": v(-250, 1148.93) * mm, "end": v(-320, 1189.34) * mm});
            skLineSegment(sketch, "E694.MirrorCS", {"start": v(-240, 612) * mm, "end": v(-310, 652.4) * mm});
            skLineSegment(sketch, "E695.MirrorCS", {"start": v(-560, 612) * mm, "end": v(-490, 652.4) * mm});
            skLineSegment(sketch, "E696.MirrorCS", {"start": v(-630, 733.23) * mm, "end": v(-630, 652.4) * mm});
            skLineSegment(sketch, "E697.MirrorCS", {"start": v(-400, 773.65) * mm, "end": v(-330, 733.23) * mm});
            skLineSegment(sketch, "E698.MirrorCS", {"start": v(870, 1068.1) * mm, "end": v(800, 1027.68) * mm});
            skLineSegment(sketch, "E699.MirrorCS", {"start": v(-250, 790.97) * mm, "end": v(-320, 750.56) * mm});
            skLineSegment(sketch, "E700.MirrorCS", {"start": v(-710, 790.97) * mm, "end": v(-640, 750.56) * mm});
            skLineSegment(sketch, "E701.MirrorCS", {"start": v(950, 929.53) * mm, "end": v(950, 1010.36) * mm});
            skLineSegment(sketch, "E702.MirrorCS", {"start": v(-170, 929.53) * mm, "end": v(-170, 1010.36) * mm});
            skLineSegment(sketch, "E703.MirrorCS", {"start": v(970, 1010.36) * mm, "end": v(970, 929.53) * mm});
            skLineSegment(sketch, "E704.MirrorCS", {"start": v(230, 790.97) * mm, "end": v(230, 871.8) * mm});
            skLineSegment(sketch, "E705.MirrorCS", {"start": v(-390, 871.8) * mm, "end": v(-320, 912.21) * mm});
            skLineSegment(sketch, "E706.MirrorCS", {"start": v(1110, 733.23) * mm, "end": v(1110, 652.4) * mm});
            skLineSegment(sketch, "E707.MirrorCS", {"start": v(-90, 1148.93) * mm, "end": v(-90, 1068.1) * mm});
            skLineSegment(sketch, "E708.MirrorCS", {"start": v(-630, 929.53) * mm, "end": v(-630, 1010.36) * mm});
            skLineSegment(sketch, "E709.MirrorCS", {"start": v(320, 635.09) * mm, "end": v(390, 594.67) * mm});
            skLineSegment(sketch, "E710.MirrorCS", {"start": v(240, 889.12) * mm, "end": v(310, 929.53) * mm});
            skLineSegment(sketch, "E711.MirrorCS", {"start": v(0, 750.56) * mm, "end": v(-70, 790.97) * mm});
            skLineSegment(sketch, "E712.MirrorCS", {"start": v(-650, 929.53) * mm, "end": v(-720, 889.12) * mm});
            skLineSegment(sketch, "E713.MirrorCS", {"start": v(480, 635.09) * mm, "end": v(410, 594.67) * mm});
            skLineSegment(sketch, "E714.MirrorCS", {"start": v(480, 750.56) * mm, "end": v(550, 790.97) * mm});
            skLineSegment(sketch, "E715.MirrorCS", {"start": v(970, 652.4) * mm, "end": v(970, 733.23) * mm});
            skLineSegment(sketch, "E716.MirrorCS", {"start": v(470, 733.23) * mm, "end": v(470, 652.4) * mm});
            skLineSegment(sketch, "E717.MirrorCS", {"start": v(490, 1010.36) * mm, "end": v(560, 1050.78) * mm});
            skLineSegment(sketch, "E718.MirrorCS", {"start": v(1030, 871.8) * mm, "end": v(1030, 790.97) * mm});
            skLineSegment(sketch, "E719.MirrorCS", {"start": v(1120, 750.56) * mm, "end": v(1190, 790.97) * mm});
            skLineSegment(sketch, "E720.MirrorCS", {"start": v(630, 652.4) * mm, "end": v(630, 733.23) * mm});
            skLineSegment(sketch, "E721.MirrorCS", {"start": v(170, 652.4) * mm, "end": v(170, 733.23) * mm});
            skLineSegment(sketch, "E722.MirrorCS", {"start": v(-320, 635.09) * mm, "end": v(-250, 594.67) * mm});
            skLineSegment(sketch, "E723.MirrorCS", {"start": v(-150, 1010.36) * mm, "end": v(-80, 1050.78) * mm});
            skLineSegment(sketch, "E724.MirrorCS", {"start": v(-230, 1148.93) * mm, "end": v(-160, 1189.34) * mm});
            skLineSegment(sketch, "E725.MirrorCS", {"start": v(810, 1010.36) * mm, "end": v(810, 929.53) * mm});
            skLineSegment(sketch, "E726.MirrorCS", {"start": v(240, 612) * mm, "end": v(170, 652.4) * mm});
            skLineSegment(sketch, "E727.MirrorCS", {"start": v(-70, 790.97) * mm, "end": v(-70, 871.8) * mm});
            skLineSegment(sketch, "E728.MirrorCS", {"start": v(150, 652.4) * mm, "end": v(150, 733.23) * mm});
            skLineSegment(sketch, "E729.MirrorCS", {"start": v(-550, 1068.1) * mm, "end": v(-550, 1148.93) * mm});
            skLineSegment(sketch, "E730.MirrorCS", {"start": v(250, 871.8) * mm, "end": v(320, 912.21) * mm});
            skLineSegment(sketch, "E731.MirrorCS", {"start": v(470, 652.4) * mm, "end": v(400, 612) * mm});
            skLineSegment(sketch, "E732.MirrorCS", {"start": v(230, 871.8) * mm, "end": v(160, 912.21) * mm});
            skLineSegment(sketch, "E733.MirrorCS", {"start": v(1030, 1148.93) * mm, "end": v(960, 1189.34) * mm});
            skLineSegment(sketch, "E734.MirrorCS", {"start": v(1040, 612) * mm, "end": v(970, 652.4) * mm});
            skLineSegment(sketch, "E735.MirrorCS", {"start": v(-310, 733.23) * mm, "end": v(-240, 773.65) * mm});
            skLineSegment(sketch, "E736.MirrorCS", {"start": v(410, 1068.1) * mm, "end": v(410, 1148.93) * mm});
            skLineSegment(sketch, "E737.MirrorCS", {"start": v(-390, 790.97) * mm, "end": v(-390, 871.8) * mm});
            skLineSegment(sketch, "E738.MirrorCS", {"start": v(880, 612) * mm, "end": v(810, 652.4) * mm});
            skLineSegment(sketch, "E739.MirrorCS", {"start": v(-70, 871.8) * mm, "end": v(0, 912.21) * mm});
            skLineSegment(sketch, "E740.MirrorCS", {"start": v(230, 1068.1) * mm, "end": v(160, 1027.68) * mm});
            skLineSegment(sketch, "E741.MirrorCS", {"start": v(550, 594.67) * mm, "end": v(480, 635.09) * mm});
            skLineSegment(sketch, "E742.MirrorCS", {"start": v(-170, 1010.36) * mm, "end": v(-240, 1050.78) * mm});
            skLineSegment(sketch, "E743.MirrorCS", {"start": v(240, 1050.78) * mm, "end": v(170, 1010.36) * mm});
            skLineSegment(sketch, "E744.MirrorCS", {"start": v(160, 635.09) * mm, "end": v(90, 594.67) * mm});
            skLineSegment(sketch, "E745.MirrorCS", {"start": v(880, 889.12) * mm, "end": v(950, 929.53) * mm});
            skLineSegment(sketch, "E746.MirrorCS", {"start": v(-160, 1027.68) * mm, "end": v(-230, 1068.1) * mm});
            skLineSegment(sketch, "E747.MirrorCS", {"start": v(1040, 773.65) * mm, "end": v(970, 733.23) * mm});
            skLineSegment(sketch, "E748.MirrorCS", {"start": v(-80, 889.12) * mm, "end": v(-150, 929.53) * mm});
            skLineSegment(sketch, "E749.MirrorCS", {"start": v(630, 929.53) * mm, "end": v(560, 889.12) * mm});
            skLineSegment(sketch, "E750.MirrorCS", {"start": v(1190, 1148.93) * mm, "end": v(1190, 1068.1) * mm});
            skLineSegment(sketch, "E751.MirrorCS", {"start": v(-550, 871.8) * mm, "end": v(-550, 790.97) * mm});
            skLineSegment(sketch, "E752.MirrorCS", {"start": v(70, 871.8) * mm, "end": v(70, 790.97) * mm});
            skLineSegment(sketch, "E753.MirrorCS", {"start": v(410, 790.97) * mm, "end": v(480, 750.56) * mm});
            skLineSegment(sketch, "E754.MirrorCS", {"start": v(-150, 733.23) * mm, "end": v(-150, 652.4) * mm});
            skLineSegment(sketch, "E755.MirrorCS", {"start": v(730, 1148.93) * mm, "end": v(800, 1189.34) * mm});
            skLineSegment(sketch, "E756.MirrorCS", {"start": v(960, 635.09) * mm, "end": v(1030, 594.67) * mm});
            skLineSegment(sketch, "E757.MirrorCS", {"start": v(-730, 790.97) * mm, "end": v(-730, 871.8) * mm});
            skLineSegment(sketch, "E758.MirrorCS", {"start": v(-310, 929.53) * mm, "end": v(-240, 889.12) * mm});
            skLineSegment(sketch, "E759.MirrorCS", {"start": v(390, 1148.93) * mm, "end": v(320, 1189.34) * mm});
            skLineSegment(sketch, "E760.MirrorCS", {"start": v(-550, 1148.93) * mm, "end": v(-480, 1189.34) * mm});
            skLineSegment(sketch, "E761.MirrorCS", {"start": v(790, 1010.36) * mm, "end": v(790, 929.53) * mm});
            skLineSegment(sketch, "E762.MirrorCS", {"start": v(390, 871.8) * mm, "end": v(390, 790.97) * mm});
            skLineSegment(sketch, "E763.MirrorCS", {"start": v(-320, 750.56) * mm, "end": v(-390, 790.97) * mm});
            skLineSegment(sketch, "E764.MirrorCS", {"start": v(800, 1027.68) * mm, "end": v(730, 1068.1) * mm});
            skLineSegment(sketch, "E765.MirrorCS", {"start": v(-490, 1010.36) * mm, "end": v(-490, 929.53) * mm});
            skLineSegment(sketch, "E766.MirrorCS", {"start": v(960, 912.21) * mm, "end": v(1030, 871.8) * mm});
            skLineSegment(sketch, "E767.MirrorCS", {"start": v(390, 790.97) * mm, "end": v(320, 750.56) * mm});
            skLineSegment(sketch, "E768.MirrorCS", {"start": v(870, 1148.93) * mm, "end": v(870, 1068.1) * mm});
            skLineSegment(sketch, "E769.MirrorCS", {"start": v(1120, 1027.68) * mm, "end": v(1050, 1068.1) * mm});
            skLineSegment(sketch, "E770.MirrorCS", {"start": v(-490, 929.53) * mm, "end": v(-560, 889.12) * mm});
            skLineSegment(sketch, "E771.MirrorCS", {"start": v(-790, 929.53) * mm, "end": v(-790, 1010.36) * mm});
            skLineSegment(sketch, "E772.MirrorCS", {"start": v(-240, 1050.78) * mm, "end": v(-310, 1010.36) * mm});
            skLineSegment(sketch, "E773.MirrorCS", {"start": v(890, 871.8) * mm, "end": v(960, 912.21) * mm});
            skLineSegment(sketch, "E774.MirrorCS", {"start": v(550, 871.8) * mm, "end": v(480, 912.21) * mm});
            skLineSegment(sketch, "E775.MirrorCS", {"start": v(170, 1010.36) * mm, "end": v(170, 929.53) * mm});
            skLineSegment(sketch, "E776.MirrorCS", {"start": v(730, 871.8) * mm, "end": v(730, 790.97) * mm});
            skLineSegment(sketch, "E777.MirrorCS", {"start": v(-330, 733.23) * mm, "end": v(-330, 652.4) * mm});
            skLineSegment(sketch, "E778.MirrorCS", {"start": v(-630, 733.23) * mm, "end": v(-560, 773.65) * mm});
            skLineSegment(sketch, "E779.MirrorCS", {"start": v(-710, 871.8) * mm, "end": v(-640, 912.21) * mm});
            skLineSegment(sketch, "E780.MirrorCS", {"start": v(-330, 929.53) * mm, "end": v(-330, 1010.36) * mm});
            skLineSegment(sketch, "E781.MirrorCS", {"start": v(-170, 652.4) * mm, "end": v(-240, 612) * mm});
            skLineSegment(sketch, "E782.MirrorCS", {"start": v(-310, 652.4) * mm, "end": v(-310, 733.23) * mm});
            skLineSegment(sketch, "E783.MirrorCS", {"start": v(970, 929.53) * mm, "end": v(1040, 889.12) * mm});
            skLineSegment(sketch, "E784.MirrorCS", {"start": v(-730, 1148.93) * mm, "end": v(-730, 1068.1) * mm});
            skLineSegment(sketch, "E785.MirrorCS", {"start": v(310, 733.23) * mm, "end": v(310, 652.4) * mm});
            skLineSegment(sketch, "E786.MirrorCS", {"start": v(-410, 1068.1) * mm, "end": v(-480, 1027.68) * mm});
            skLineSegment(sketch, "E787.MirrorCS", {"start": v(-410, 594.67) * mm, "end": v(-480, 635.09) * mm});
            skLineSegment(sketch, "E788.MirrorCS", {"start": v(-160, 912.21) * mm, "end": v(-230, 871.8) * mm});
            skLineSegment(sketch, "E789.MirrorCS", {"start": v(-150, 929.53) * mm, "end": v(-150, 1010.36) * mm});
            skLineSegment(sketch, "E790.MirrorCS", {"start": v(-230, 871.8) * mm, "end": v(-230, 790.97) * mm});
            skLineSegment(sketch, "E791.MirrorCS", {"start": v(250, 790.97) * mm, "end": v(250, 871.8) * mm});
            skLineSegment(sketch, "E792.MirrorCS", {"start": v(-410, 871.8) * mm, "end": v(-480, 912.21) * mm});
            skLineSegment(sketch, "E793.MirrorCS", {"start": v(710, 1068.1) * mm, "end": v(710, 1148.93) * mm});
            skLineSegment(sketch, "E794.MirrorCS", {"start": v(790, 652.4) * mm, "end": v(790, 733.23) * mm});
            skLineSegment(sketch, "E795.MirrorCS", {"start": v(650, 652.4) * mm, "end": v(720, 612) * mm});
            skLineSegment(sketch, "E796.MirrorCS", {"start": v(160, 750.56) * mm, "end": v(230, 790.97) * mm});
            skLineSegment(sketch, "E797.MirrorCS", {"start": v(-790, 1010.36) * mm, "end": v(-720, 1050.78) * mm});
            skLineSegment(sketch, "E798.MirrorCS", {"start": v(-410, 1148.93) * mm, "end": v(-410, 1068.1) * mm});
            skLineSegment(sketch, "E799.MirrorCS", {"start": v(490, 652.4) * mm, "end": v(560, 612) * mm});
            skLineSegment(sketch, "E800.MirrorCS", {"start": v(80, 889.12) * mm, "end": v(10, 929.53) * mm});
            skLineSegment(sketch, "E801.MirrorCS", {"start": v(-160, 635.09) * mm, "end": v(-230, 594.67) * mm});
            skLineSegment(sketch, "E802.MirrorCS", {"start": v(-320, 912.21) * mm, "end": v(-250, 871.8) * mm});
            skLineSegment(sketch, "E803.MirrorCS", {"start": v(-250, 871.8) * mm, "end": v(-250, 790.97) * mm});
            skLineSegment(sketch, "E804.MirrorCS", {"start": v(10, 652.4) * mm, "end": v(80, 612) * mm});
            skLineSegment(sketch, "E805.MirrorCS", {"start": v(-80, 612) * mm, "end": v(-10, 652.4) * mm});
            skLineSegment(sketch, "E806.MirrorCS", {"start": v(-790, 929.53) * mm, "end": v(-720, 889.12) * mm});
            skLineSegment(sketch, "E807.MirrorCS", {"start": v(-400, 889.12) * mm, "end": v(-470, 929.53) * mm});
            skLineSegment(sketch, "E808.MirrorCS", {"start": v(-570, 790.97) * mm, "end": v(-640, 750.56) * mm});
            skLineSegment(sketch, "E809.MirrorCS", {"start": v(650, 929.53) * mm, "end": v(650, 1010.36) * mm});
            skLineSegment(sketch, "E810.MirrorCS", {"start": v(1130, 929.53) * mm, "end": v(1130, 1010.36) * mm});
            skLineSegment(sketch, "E811.MirrorCS", {"start": v(950, 1010.36) * mm, "end": v(880, 1050.78) * mm});
            skLineSegment(sketch, "E812.MirrorCS", {"start": v(410, 871.8) * mm, "end": v(410, 790.97) * mm});
            skLineSegment(sketch, "E813.MirrorCS", {"start": v(330, 652.4) * mm, "end": v(330, 733.23) * mm});
            skLineSegment(sketch, "E814.MirrorCS", {"start": v(640, 1027.68) * mm, "end": v(710, 1068.1) * mm});
            skLineSegment(sketch, "E815.MirrorCS", {"start": v(1120, 635.09) * mm, "end": v(1050, 594.67) * mm});
            skLineSegment(sketch, "E816.MirrorCS", {"start": v(-640, 635.09) * mm, "end": v(-570, 594.67) * mm});
            skLineSegment(sketch, "E817.MirrorCS", {"start": v(330, 733.23) * mm, "end": v(400, 773.65) * mm});
            skLineSegment(sketch, "E818.MirrorCS", {"start": v(330, 1010.36) * mm, "end": v(330, 929.53) * mm});
            skLineSegment(sketch, "E819.MirrorCS", {"start": v(-90, 871.8) * mm, "end": v(-160, 912.21) * mm});
            skLineSegment(sketch, "E820.MirrorCS", {"start": v(-390, 1068.1) * mm, "end": v(-320, 1027.68) * mm});
            skLineSegment(sketch, "E821.MirrorCS", {"start": v(-230, 790.97) * mm, "end": v(-160, 750.56) * mm});
            skLineSegment(sketch, "E822.MirrorCS", {"start": v(160, 1189.34) * mm, "end": v(230, 1148.93) * mm});
            skLineSegment(sketch, "E823.MirrorCS", {"start": v(0, 635.09) * mm, "end": v(70, 594.67) * mm});
            skLineSegment(sketch, "E824.MirrorCS", {"start": v(960, 1027.68) * mm, "end": v(1030, 1068.1) * mm});
            skLineSegment(sketch, "E825.MirrorCS", {"start": v(250, 594.67) * mm, "end": v(320, 635.09) * mm});
            skLineSegment(sketch, "E826.MirrorCS", {"start": v(1050, 871.8) * mm, "end": v(1050, 790.97) * mm});
            skLineSegment(sketch, "E827.MirrorCS", {"start": v(560, 612) * mm, "end": v(630, 652.4) * mm});
            skLineSegment(sketch, "E828.MirrorCS", {"start": v(1050, 1148.93) * mm, "end": v(1120, 1189.34) * mm});
            skLineSegment(sketch, "E829.MirrorCS", {"start": v(720, 773.65) * mm, "end": v(790, 733.23) * mm});
            skLineSegment(sketch, "E830.MirrorCS", {"start": v(1040, 773.65) * mm, "end": v(1110, 733.23) * mm});
            skLineSegment(sketch, "E831.MirrorCS", {"start": v(630, 1010.36) * mm, "end": v(630, 929.53) * mm});
            skLineSegment(sketch, "E832.MirrorCS", {"start": v(-730, 1068.1) * mm, "end": v(-800, 1027.68) * mm});
            skLineSegment(sketch, "E833.MirrorCS", {"start": v(800, 912.21) * mm, "end": v(730, 871.8) * mm});
            skLineSegment(sketch, "E834.MirrorCS", {"start": v(890, 594.67) * mm, "end": v(960, 635.09) * mm});
            skLineSegment(sketch, "E835.MirrorCS", {"start": v(480, 912.21) * mm, "end": v(410, 871.8) * mm});
            skLineSegment(sketch, "E836.MirrorCS", {"start": v(-400, 612) * mm, "end": v(-470, 652.4) * mm});
            skLineSegment(sketch, "E837.MirrorCS", {"start": v(960, 1189.34) * mm, "end": v(890, 1148.93) * mm});
            skLineSegment(sketch, "E838.MirrorCS", {"start": v(-640, 1466.47) * mm, "end": v(-710, 1426.06) * mm});
            skLineSegment(sketch, "E839.MirrorCS", {"start": v(-400, 1882.16) * mm, "end": v(-470, 1841.75) * mm});
            skLineSegment(sketch, "E840.MirrorCS", {"start": v(400, 1327.9) * mm, "end": v(470, 1287.5) * mm});
            skLineSegment(sketch, "E841.MirrorCS", {"start": v(790, 1841.75) * mm, "end": v(720, 1882.16) * mm});
            skLineSegment(sketch, "E842.MirrorCS", {"start": v(400, 1443.38) * mm, "end": v(330, 1483.8) * mm});
            skLineSegment(sketch, "E843.MirrorCS", {"start": v(-650, 1841.75) * mm, "end": v(-720, 1882.16) * mm});
            skLineSegment(sketch, "E844.MirrorCS", {"start": v(1040, 1443.38) * mm, "end": v(970, 1483.8) * mm});
            skLineSegment(sketch, "E845.MirrorCS", {"start": v(640, 1466.47) * mm, "end": v(570, 1426.06) * mm});
            skLineSegment(sketch, "E846.MirrorCS", {"start": v(1190, 1322.13) * mm, "end": v(1130, 1287.5) * mm});
            skLineSegment(sketch, "E847.MirrorCS", {"start": v(630, 1287.5) * mm, "end": v(560, 1327.9) * mm});
            skLineSegment(sketch, "E848.MirrorCS", {"start": v(-570, 1622.35) * mm, "end": v(-640, 1581.94) * mm});
            skLineSegment(sketch, "E849.MirrorCS", {"start": v(-790, 1841.75) * mm, "end": v(-720, 1882.16) * mm});
            skLineSegment(sketch, "E850.MirrorCS", {"start": v(1110, 1841.75) * mm, "end": v(1040, 1882.16) * mm});
            skLineSegment(sketch, "E851.MirrorCS", {"start": v(-560, 1882.16) * mm, "end": v(-490, 1841.75) * mm});
            skLineSegment(sketch, "E852.MirrorCS", {"start": v(-320, 1581.94) * mm, "end": v(-250, 1622.35) * mm});
            skLineSegment(sketch, "E853.MirrorCS", {"start": v(490, 1287.5) * mm, "end": v(560, 1327.9) * mm});
            skLineSegment(sketch, "E854.MirrorCS", {"start": v(-150, 1841.75) * mm, "end": v(-80, 1882.16) * mm});
            skLineSegment(sketch, "E855.MirrorCS", {"start": v(-630, 1287.5) * mm, "end": v(-560, 1327.9) * mm});
            skLineSegment(sketch, "E856.MirrorCS", {"start": v(-80, 1327.9) * mm, "end": v(-10, 1287.5) * mm});
            skLineSegment(sketch, "E857.MirrorCS", {"start": v(10, 1483.8) * mm, "end": v(80, 1443.38) * mm});
            skLineSegment(sketch, "E858.MirrorCS", {"start": v(240, 1882.16) * mm, "end": v(310, 1841.75) * mm});
            skLineSegment(sketch, "E859.MirrorCS", {"start": v(70, 1622.35) * mm, "end": v(0, 1581.94) * mm});
            skLineSegment(sketch, "E860.MirrorCS", {"start": v(960, 1581.94) * mm, "end": v(1030, 1622.35) * mm});
            skLineSegment(sketch, "E861.MirrorCS", {"start": v(-400, 1443.38) * mm, "end": v(-470, 1483.8) * mm});
            skLineSegment(sketch, "E862.MirrorCS", {"start": v(-720, 1327.9) * mm, "end": v(-790, 1287.5) * mm});
            skLineSegment(sketch, "E863.MirrorCS", {"start": v(-150, 1483.8) * mm, "end": v(-80, 1443.38) * mm});
            skLineSegment(sketch, "E864.MirrorCS", {"start": v(890, 1622.35) * mm, "end": v(960, 1581.94) * mm});
            skLineSegment(sketch, "E865.MirrorCS", {"start": v(810, 1841.75) * mm, "end": v(880, 1882.16) * mm});
            skLineSegment(sketch, "E866.MirrorCS", {"start": v(-400, 1327.9) * mm, "end": v(-330, 1287.5) * mm});
            skLineSegment(sketch, "E867.MirrorCS", {"start": v(650, 1841.75) * mm, "end": v(720, 1882.16) * mm});
            skLineSegment(sketch, "E868.MirrorCS", {"start": v(560, 1882.16) * mm, "end": v(630, 1841.75) * mm});
            skLineSegment(sketch, "E869.MirrorCS", {"start": v(640, 1466.47) * mm, "end": v(710, 1426.06) * mm});
            skLineSegment(sketch, "E870.MirrorCS", {"start": v(-470, 1287.5) * mm, "end": v(-400, 1327.9) * mm});
            skLineSegment(sketch, "E871.MirrorCS", {"start": v(-330, 1483.8) * mm, "end": v(-400, 1443.38) * mm});
            skLineSegment(sketch, "E872.MirrorCS", {"start": v(470, 1483.8) * mm, "end": v(400, 1443.38) * mm});
            skLineSegment(sketch, "E873.MirrorCS", {"start": v(80, 1882.16) * mm, "end": v(150, 1841.75) * mm});
            skLineSegment(sketch, "E874.MirrorCS", {"start": v(-70, 1426.06) * mm, "end": v(0, 1466.47) * mm});
            skLineSegment(sketch, "E875.MirrorCS", {"start": v(-630, 1841.75) * mm, "end": v(-560, 1882.16) * mm});
            skLineSegment(sketch, "E876.MirrorCS", {"start": v(-70, 1622.35) * mm, "end": v(0, 1581.94) * mm});
            skLineSegment(sketch, "E877.MirrorCS", {"start": v(890, 1426.06) * mm, "end": v(960, 1466.47) * mm});
            skLineSegment(sketch, "E878.MirrorCS", {"start": v(550, 1426.06) * mm, "end": v(480, 1466.47) * mm});
            skLineSegment(sketch, "E879.MirrorCS", {"start": v(10, 1287.5) * mm, "end": v(80, 1327.9) * mm});
            skLineSegment(sketch, "E880.MirrorCS", {"start": v(640, 1581.94) * mm, "end": v(710, 1622.35) * mm});
            skLineSegment(sketch, "E881.MirrorCS", {"start": v(950, 1483.8) * mm, "end": v(880, 1443.38) * mm});
            skLineSegment(sketch, "E882.MirrorCS", {"start": v(950, 1841.75) * mm, "end": v(880, 1882.16) * mm});
            skLineSegment(sketch, "E883.MirrorCS", {"start": v(880, 1327.9) * mm, "end": v(950, 1287.5) * mm});
            skLineSegment(sketch, "E884.MirrorCS", {"start": v(1040, 1882.16) * mm, "end": v(970, 1841.75) * mm});
            skLineSegment(sketch, "E885.MirrorCS", {"start": v(960, 1466.47) * mm, "end": v(1030, 1426.06) * mm});
            skLineSegment(sketch, "E886.MirrorCS", {"start": v(-730, 1426.06) * mm, "end": v(-800, 1466.47) * mm});
            skLineSegment(sketch, "E887.MirrorCS", {"start": v(-240, 1443.38) * mm, "end": v(-310, 1483.8) * mm});
            skLineSegment(sketch, "E888.MirrorCS", {"start": v(-410, 1426.06) * mm, "end": v(-480, 1466.47) * mm});
            skLineSegment(sketch, "E889.MirrorCS", {"start": v(-160, 1581.94) * mm, "end": v(-90, 1622.35) * mm});
            skLineSegment(sketch, "E890.MirrorCS", {"start": v(870, 1426.06) * mm, "end": v(800, 1466.47) * mm});
            skLineSegment(sketch, "E891.MirrorCS", {"start": v(1190, 1449.15) * mm, "end": v(1130, 1483.8) * mm});
            skLineSegment(sketch, "E892.MirrorCS", {"start": v(870, 1622.35) * mm, "end": v(800, 1581.94) * mm});
            skLineSegment(sketch, "E893.MirrorCS", {"start": v(320, 1581.94) * mm, "end": v(250, 1622.35) * mm});
            skLineSegment(sketch, "E894.MirrorCS", {"start": v(-720, 1443.38) * mm, "end": v(-650, 1483.8) * mm});
            skLineSegment(sketch, "E895.MirrorCS", {"start": v(-570, 1426.06) * mm, "end": v(-640, 1466.47) * mm});
            skLineSegment(sketch, "E896.MirrorCS", {"start": v(-560, 1443.38) * mm, "end": v(-630, 1483.8) * mm});
            skLineSegment(sketch, "E897.MirrorCS", {"start": v(10, 1841.75) * mm, "end": v(80, 1882.16) * mm});
            skLineSegment(sketch, "E898.MirrorCS", {"start": v(1040, 1443.38) * mm, "end": v(1110, 1483.8) * mm});
            skLineSegment(sketch, "E899.MirrorCS", {"start": v(-560, 1443.38) * mm, "end": v(-490, 1483.8) * mm});
            skLineSegment(sketch, "E900.MirrorCS", {"start": v(480, 1466.47) * mm, "end": v(410, 1426.06) * mm});
            skLineSegment(sketch, "E901.MirrorCS", {"start": v(-150, 1287.5) * mm, "end": v(-80, 1327.9) * mm});
            skLineSegment(sketch, "E902.MirrorCS", {"start": v(330, 1287.5) * mm, "end": v(400, 1327.9) * mm});
            skLineSegment(sketch, "E903.MirrorCS", {"start": v(150, 1287.5) * mm, "end": v(80, 1327.9) * mm});
            skLineSegment(sketch, "E904.MirrorCS", {"start": v(-790, 1483.8) * mm, "end": v(-720, 1443.38) * mm});
            skLineSegment(sketch, "E905.MirrorCS", {"start": v(570, 1622.35) * mm, "end": v(640, 1581.94) * mm});
            skLineSegment(sketch, "E906.MirrorCS", {"start": v(0, 1466.47) * mm, "end": v(70, 1426.06) * mm});
            skLineSegment(sketch, "E907.MirrorCS", {"start": v(150, 1483.8) * mm, "end": v(80, 1443.38) * mm});
            skLineSegment(sketch, "E908.MirrorCS", {"start": v(480, 1581.94) * mm, "end": v(410, 1622.35) * mm});
            skLineSegment(sketch, "E909.MirrorCS", {"start": v(320, 1466.47) * mm, "end": v(250, 1426.06) * mm});
            skLineSegment(sketch, "E910.MirrorCS", {"start": v(-480, 1581.94) * mm, "end": v(-410, 1622.35) * mm});
            skLineSegment(sketch, "E911.MirrorCS", {"start": v(-720, 1327.9) * mm, "end": v(-650, 1287.5) * mm});
            skLineSegment(sketch, "E912.MirrorCS", {"start": v(1120, 1581.94) * mm, "end": v(1050, 1622.35) * mm});
            skLineSegment(sketch, "E913.MirrorCS", {"start": v(320, 1581.94) * mm, "end": v(390, 1622.35) * mm});
            skLineSegment(sketch, "E914.MirrorCS", {"start": v(560, 1443.38) * mm, "end": v(630, 1483.8) * mm});
            skLineSegment(sketch, "E915.MirrorCS", {"start": v(240, 1443.38) * mm, "end": v(170, 1483.8) * mm});
            skLineSegment(sketch, "E916.MirrorCS", {"start": v(-330, 1841.75) * mm, "end": v(-400, 1882.16) * mm});
            skLineSegment(sketch, "E917.MirrorCS", {"start": v(560, 1882.16) * mm, "end": v(490, 1841.75) * mm});
            skLineSegment(sketch, "E918.MirrorCS", {"start": v(240, 1443.38) * mm, "end": v(310, 1483.8) * mm});
            skLineSegment(sketch, "E919.MirrorCS", {"start": v(1120, 1466.47) * mm, "end": v(1050, 1426.06) * mm});
            skLineSegment(sketch, "E920.MirrorCS", {"start": v(1120, 1581.94) * mm, "end": v(1190, 1622.35) * mm});
            skLineSegment(sketch, "E921.MirrorCS", {"start": v(720, 1327.9) * mm, "end": v(790, 1287.5) * mm});
            skLineSegment(sketch, "E922.MirrorCS", {"start": v(-490, 1287.5) * mm, "end": v(-560, 1327.9) * mm});
            skLineSegment(sketch, "E923.MirrorCS", {"start": v(800, 1581.94) * mm, "end": v(730, 1622.35) * mm});
            skLineSegment(sketch, "E924.MirrorCS", {"start": v(1040, 1327.9) * mm, "end": v(1110, 1287.5) * mm});
            skLineSegment(sketch, "E925.MirrorCS", {"start": v(-160, 1466.47) * mm, "end": v(-90, 1426.06) * mm});
            skLineSegment(sketch, "E926.MirrorCS", {"start": v(560, 1443.38) * mm, "end": v(490, 1483.8) * mm});
            skLineSegment(sketch, "E927.MirrorCS", {"start": v(-170, 1483.8) * mm, "end": v(-240, 1443.38) * mm});
            skLineSegment(sketch, "E928.MirrorCS", {"start": v(810, 1483.8) * mm, "end": v(880, 1443.38) * mm});
            skLineSegment(sketch, "E929.MirrorCS", {"start": v(-10, 1841.75) * mm, "end": v(-80, 1882.16) * mm});
            skLineSegment(sketch, "E930.MirrorCS", {"start": v(-240, 1882.16) * mm, "end": v(-310, 1841.75) * mm});
            skLineSegment(sketch, "E931.MirrorCS", {"start": v(1120, 1466.47) * mm, "end": v(1190, 1426.06) * mm});
            skLineSegment(sketch, "E932.MirrorCS", {"start": v(240, 1882.16) * mm, "end": v(170, 1841.75) * mm});
            skLineSegment(sketch, "E933.MirrorCS", {"start": v(-550, 1622.35) * mm, "end": v(-480, 1581.94) * mm});
            skLineSegment(sketch, "E934.MirrorCS", {"start": v(400, 1882.16) * mm, "end": v(470, 1841.75) * mm});
            skLineSegment(sketch, "E935.MirrorCS", {"start": v(-170, 1287.5) * mm, "end": v(-240, 1327.9) * mm});
            skLineSegment(sketch, "E936.MirrorCS", {"start": v(-160, 1581.94) * mm, "end": v(-230, 1622.35) * mm});
            skLineSegment(sketch, "E937.MirrorCS", {"start": v(160, 1581.94) * mm, "end": v(230, 1622.35) * mm});
            skLineSegment(sketch, "E938.MirrorCS", {"start": v(1040, 1327.9) * mm, "end": v(970, 1287.5) * mm});
            skLineSegment(sketch, "E939.MirrorCS", {"start": v(-250, 1426.06) * mm, "end": v(-320, 1466.47) * mm});
            skLineSegment(sketch, "E940.MirrorCS", {"start": v(-480, 1466.47) * mm, "end": v(-550, 1426.06) * mm});
            skLineSegment(sketch, "E941.MirrorCS", {"start": v(-390, 1622.35) * mm, "end": v(-320, 1581.94) * mm});
            skLineSegment(sketch, "E942.MirrorCS", {"start": v(330, 1841.75) * mm, "end": v(400, 1882.16) * mm});
            skLineSegment(sketch, "E943.MirrorCS", {"start": v(810, 1287.5) * mm, "end": v(880, 1327.9) * mm});
            skLineSegment(sketch, "E944.MirrorCS", {"start": v(-390, 1426.06) * mm, "end": v(-320, 1466.47) * mm});
            skLineSegment(sketch, "E945.MirrorCS", {"start": v(160, 1466.47) * mm, "end": v(90, 1426.06) * mm});
            skLineSegment(sketch, "E946.MirrorCS", {"start": v(790, 1483.8) * mm, "end": v(720, 1443.38) * mm});
            skLineSegment(sketch, "E947.MirrorCS", {"start": v(160, 1581.94) * mm, "end": v(90, 1622.35) * mm});
            skLineSegment(sketch, "E948.MirrorCS", {"start": v(-160, 1466.47) * mm, "end": v(-230, 1426.06) * mm});
            skLineSegment(sketch, "E949.MirrorCS", {"start": v(480, 1581.94) * mm, "end": v(550, 1622.35) * mm});
            skLineSegment(sketch, "E950.MirrorCS", {"start": v(720, 1327.9) * mm, "end": v(650, 1287.5) * mm});
            skLineSegment(sketch, "E951.MirrorCS", {"start": v(240, 1327.9) * mm, "end": v(310, 1287.5) * mm});
            skLineSegment(sketch, "E952.MirrorCS", {"start": v(-240, 1882.16) * mm, "end": v(-170, 1841.75) * mm});
            skLineSegment(sketch, "E953.MirrorCS", {"start": v(-310, 1287.5) * mm, "end": v(-240, 1327.9) * mm});
            skLineSegment(sketch, "E954.MirrorCS", {"start": v(-10, 1483.8) * mm, "end": v(-80, 1443.38) * mm});
            skLineSegment(sketch, "E955.MirrorCS", {"start": v(170, 1287.5) * mm, "end": v(240, 1327.9) * mm});
            skLineSegment(sketch, "E956.MirrorCS", {"start": v(-710, 1622.35) * mm, "end": v(-640, 1581.94) * mm});
            skLineSegment(sketch, "E957.MirrorCS", {"start": v(650, 1483.8) * mm, "end": v(720, 1443.38) * mm});
            skLineSegment(sketch, "E958.MirrorCS", {"start": v(730, 1426.06) * mm, "end": v(800, 1466.47) * mm});
            skLineSegment(sketch, "E959.MirrorCS", {"start": v(230, 1426.06) * mm, "end": v(160, 1466.47) * mm});
            skLineSegment(sketch, "E960.MirrorCS", {"start": v(320, 1466.47) * mm, "end": v(390, 1426.06) * mm});
            skLineSegment(sketch, "E961.MirrorCS", {"start": v(-80, 1882.16) * mm, "end": v(-10, 1841.75) * mm});
            skLineSegment(sketch, "E962.MirrorCS", {"start": v(1110, 1206.66) * mm, "end": v(1040, 1166.25) * mm});
            skLineSegment(sketch, "E963.MirrorCS", {"start": v(240, 1720.5) * mm, "end": v(170, 1760.92) * mm});
            skLineSegment(sketch, "E964.MirrorCS", {"start": v(400, 1443.38) * mm, "end": v(470, 1483.8) * mm});
            skLineSegment(sketch, "E965.MirrorCS", {"start": v(570, 1426.06) * mm, "end": v(570, 1345.23) * mm});
            skLineSegment(sketch, "E966.MirrorCS", {"start": v(630, 1760.92) * mm, "end": v(630, 1841.75) * mm});
            skLineSegment(sketch, "E967.MirrorCS", {"start": v(80, 1605.03) * mm, "end": v(150, 1564.62) * mm});
            skLineSegment(sketch, "E968.MirrorCS", {"start": v(870, 1622.35) * mm, "end": v(870, 1703.18) * mm});
            skLineSegment(sketch, "E969.MirrorCS", {"start": v(490, 1841.75) * mm, "end": v(490, 1760.92) * mm});
            skLineSegment(sketch, "E970.MirrorCS", {"start": v(890, 1622.35) * mm, "end": v(890, 1703.18) * mm});
            skLineSegment(sketch, "E971.MirrorCS", {"start": v(170, 1841.75) * mm, "end": v(240, 1882.16) * mm});
            skLineSegment(sketch, "E972.MirrorCS", {"start": v(410, 1703.18) * mm, "end": v(410, 1622.35) * mm});
            skLineSegment(sketch, "E973.MirrorCS", {"start": v(570, 1622.35) * mm, "end": v(570, 1703.18) * mm});
            skLineSegment(sketch, "E974.MirrorCS", {"start": v(720, 1882.16) * mm, "end": v(650, 1841.75) * mm});
            skLineSegment(sketch, "E975.MirrorCS", {"start": v(1130, 1287.5) * mm, "end": v(1190, 1322.13) * mm});
            skLineSegment(sketch, "E976.MirrorCS", {"start": v(310, 1287.5) * mm, "end": v(310, 1206.66) * mm});
            skLineSegment(sketch, "E977.MirrorCS", {"start": v(400, 1166.25) * mm, "end": v(330, 1206.66) * mm});
            skLineSegment(sketch, "E978.MirrorCS", {"start": v(-570, 1345.23) * mm, "end": v(-570, 1426.06) * mm});
            skLineSegment(sketch, "E979.MirrorCS", {"start": v(-490, 1760.92) * mm, "end": v(-490, 1841.75) * mm});
            skLineSegment(sketch, "E980.MirrorCS", {"start": v(560, 1720.5) * mm, "end": v(630, 1760.92) * mm});
            skLineSegment(sketch, "E981.MirrorCS", {"start": v(330, 1483.8) * mm, "end": v(400, 1443.38) * mm});
            skLineSegment(sketch, "E982.MirrorCS", {"start": v(870, 1148.93) * mm, "end": v(800, 1189.34) * mm});
            skLineSegment(sketch, "E983.MirrorCS", {"start": v(-330, 1287.5) * mm, "end": v(-330, 1206.66) * mm});
            skLineSegment(sketch, "E984.MirrorCS", {"start": v(400, 1605.03) * mm, "end": v(330, 1564.62) * mm});
            skLineSegment(sketch, "E985.MirrorCS", {"start": v(-730, 1345.23) * mm, "end": v(-800, 1304.81) * mm});
            skLineSegment(sketch, "E986.MirrorCS", {"start": v(-390, 1426.06) * mm, "end": v(-390, 1345.23) * mm});
            skLineSegment(sketch, "E987.MirrorCS", {"start": v(250, 1622.35) * mm, "end": v(250, 1703.18) * mm});
            skLineSegment(sketch, "E988.MirrorCS", {"start": v(640, 1189.34) * mm, "end": v(710, 1148.93) * mm});
            skLineSegment(sketch, "E989.MirrorCS", {"start": v(-470, 1564.62) * mm, "end": v(-470, 1483.8) * mm});
            skLineSegment(sketch, "E990.MirrorCS", {"start": v(-10, 1760.92) * mm, "end": v(-10, 1841.75) * mm});
            skLineSegment(sketch, "E991.MirrorCS", {"start": v(890, 1148.93) * mm, "end": v(960, 1189.34) * mm});
            skLineSegment(sketch, "E992.MirrorCS", {"start": v(310, 1841.75) * mm, "end": v(240, 1882.16) * mm});
            skLineSegment(sketch, "E993.MirrorCS", {"start": v(710, 1426.06) * mm, "end": v(640, 1466.47) * mm});
            skLineSegment(sketch, "E994.MirrorCS", {"start": v(1110, 1287.5) * mm, "end": v(1040, 1327.9) * mm});
            skLineSegment(sketch, "E995.MirrorCS", {"start": v(-150, 1483.8) * mm, "end": v(-150, 1564.62) * mm});
            skLineSegment(sketch, "E996.MirrorCS", {"start": v(230, 1622.35) * mm, "end": v(230, 1703.18) * mm});
            skLineSegment(sketch, "E997.MirrorCS", {"start": v(240, 1166.25) * mm, "end": v(170, 1206.66) * mm});
            skLineSegment(sketch, "E998.MirrorCS", {"start": v(560, 1166.25) * mm, "end": v(630, 1206.66) * mm});
            skLineSegment(sketch, "E999.MirrorCS", {"start": v(-720, 1882.16) * mm, "end": v(-650, 1841.75) * mm});
            skLineSegment(sketch, "E1000.MirrorCS", {"start": v(70, 1345.23) * mm, "end": v(70, 1426.06) * mm});
            skLineSegment(sketch, "E1001.MirrorCS", {"start": v(150, 1841.75) * mm, "end": v(80, 1882.16) * mm});
            skLineSegment(sketch, "E1002.MirrorCS", {"start": v(710, 1703.18) * mm, "end": v(710, 1622.35) * mm});
            skLineSegment(sketch, "E1003.MirrorCS", {"start": v(-150, 1287.5) * mm, "end": v(-150, 1206.66) * mm});
            skLineSegment(sketch, "E1004.MirrorCS", {"start": v(90, 1622.35) * mm, "end": v(160, 1581.94) * mm});
            skLineSegment(sketch, "E1005.MirrorCS", {"start": v(-710, 1703.18) * mm, "end": v(-640, 1743.6) * mm});
            skLineSegment(sketch, "E1006.MirrorCS", {"start": v(-630, 1564.62) * mm, "end": v(-560, 1605.03) * mm});
            skLineSegment(sketch, "E1007.MirrorCS", {"start": v(-550, 1426.06) * mm, "end": v(-480, 1466.47) * mm});
            skLineSegment(sketch, "E1008.MirrorCS", {"start": v(-240, 1443.38) * mm, "end": v(-170, 1483.8) * mm});
            skLineSegment(sketch, "E1009.MirrorCS", {"start": v(490, 1206.66) * mm, "end": v(560, 1166.25) * mm});
            skLineSegment(sketch, "E1010.MirrorCS", {"start": v(-790, 1564.62) * mm, "end": v(-720, 1605.03) * mm});
            skLineSegment(sketch, "E1011.MirrorCS", {"start": v(490, 1564.62) * mm, "end": v(560, 1605.03) * mm});
            skLineSegment(sketch, "E1012.MirrorCS", {"start": v(470, 1841.75) * mm, "end": v(470, 1760.92) * mm});
            skLineSegment(sketch, "E1013.MirrorCS", {"start": v(-10, 1287.5) * mm, "end": v(-80, 1327.9) * mm});
            skLineSegment(sketch, "E1014.MirrorCS", {"start": v(-70, 1345.23) * mm, "end": v(0, 1304.81) * mm});
            skLineSegment(sketch, "E1015.MirrorCS", {"start": v(960, 1743.6) * mm, "end": v(1030, 1703.18) * mm});
            skLineSegment(sketch, "E1016.MirrorCS", {"start": v(-410, 1703.18) * mm, "end": v(-480, 1743.6) * mm});
            skLineSegment(sketch, "E1017.MirrorCS", {"start": v(470, 1564.62) * mm, "end": v(400, 1605.03) * mm});
            skLineSegment(sketch, "E1018.MirrorCS", {"start": v(-330, 1564.62) * mm, "end": v(-400, 1605.03) * mm});
            skLineSegment(sketch, "E1019.MirrorCS", {"start": v(80, 1327.9) * mm, "end": v(10, 1287.5) * mm});
            skLineSegment(sketch, "E1020.MirrorCS", {"start": v(970, 1760.92) * mm, "end": v(970, 1841.75) * mm});
            skLineSegment(sketch, "E1021.MirrorCS", {"start": v(950, 1760.92) * mm, "end": v(880, 1720.5) * mm});
            skLineSegment(sketch, "E1022.MirrorCS", {"start": v(170, 1760.92) * mm, "end": v(170, 1841.75) * mm});
            skLineSegment(sketch, "E1023.MirrorCS", {"start": v(-640, 1581.94) * mm, "end": v(-570, 1622.35) * mm});
            skLineSegment(sketch, "E1024.MirrorCS", {"start": v(-550, 1345.23) * mm, "end": v(-550, 1426.06) * mm});
            skLineSegment(sketch, "E1025.MirrorCS", {"start": v(-160, 1304.81) * mm, "end": v(-230, 1345.23) * mm});
            skLineSegment(sketch, "E1026.MirrorCS", {"start": v(-240, 1327.9) * mm, "end": v(-310, 1287.5) * mm});
            skLineSegment(sketch, "E1027.MirrorCS", {"start": v(470, 1206.66) * mm, "end": v(400, 1166.25) * mm});
            skLineSegment(sketch, "E1028.MirrorCS", {"start": v(250, 1148.93) * mm, "end": v(320, 1189.34) * mm});
            skLineSegment(sketch, "E1029.MirrorCS", {"start": v(-320, 1466.47) * mm, "end": v(-250, 1426.06) * mm});
            skLineSegment(sketch, "E1030.MirrorCS", {"start": v(90, 1345.23) * mm, "end": v(90, 1426.06) * mm});
            skLineSegment(sketch, "E1031.MirrorCS", {"start": v(650, 1760.92) * mm, "end": v(720, 1720.5) * mm});
            skLineSegment(sketch, "E1032.MirrorCS", {"start": v(160, 1466.47) * mm, "end": v(230, 1426.06) * mm});
            skLineSegment(sketch, "E1033.MirrorCS", {"start": v(-230, 1345.23) * mm, "end": v(-230, 1426.06) * mm});
            skLineSegment(sketch, "E1034.MirrorCS", {"start": v(490, 1760.92) * mm, "end": v(560, 1720.5) * mm});
            skLineSegment(sketch, "E1035.MirrorCS", {"start": v(1130, 1483.8) * mm, "end": v(1190, 1449.15) * mm});
            skLineSegment(sketch, "E1036.MirrorCS", {"start": v(870, 1703.18) * mm, "end": v(800, 1743.6) * mm});
            skLineSegment(sketch, "E1037.MirrorCS", {"start": v(800, 1466.47) * mm, "end": v(730, 1426.06) * mm});
            skLineSegment(sketch, "E1038.MirrorCS", {"start": v(960, 1189.34) * mm, "end": v(1030, 1148.93) * mm});
            skLineSegment(sketch, "E1039.MirrorCS", {"start": v(-70, 1426.06) * mm, "end": v(-70, 1345.23) * mm});
            skLineSegment(sketch, "E1040.MirrorCS", {"start": v(0, 1581.94) * mm, "end": v(70, 1622.35) * mm});
            skLineSegment(sketch, "E1041.MirrorCS", {"start": v(720, 1443.38) * mm, "end": v(790, 1483.8) * mm});
            skLineSegment(sketch, "E1042.MirrorCS", {"start": v(650, 1206.66) * mm, "end": v(720, 1166.25) * mm});
            skLineSegment(sketch, "E1043.MirrorCS", {"start": v(710, 1345.23) * mm, "end": v(710, 1426.06) * mm});
            skLineSegment(sketch, "E1044.MirrorCS", {"start": v(480, 1304.81) * mm, "end": v(410, 1345.23) * mm});
            skLineSegment(sketch, "E1045.MirrorCS", {"start": v(950, 1287.5) * mm, "end": v(880, 1327.9) * mm});
            skLineSegment(sketch, "E1046.MirrorCS", {"start": v(-630, 1841.75) * mm, "end": v(-630, 1760.92) * mm});
            skLineSegment(sketch, "E1047.MirrorCS", {"start": v(-490, 1564.62) * mm, "end": v(-490, 1483.8) * mm});
            skLineSegment(sketch, "E1048.MirrorCS", {"start": v(-250, 1345.23) * mm, "end": v(-250, 1426.06) * mm});
            skLineSegment(sketch, "E1049.MirrorCS", {"start": v(720, 1605.03) * mm, "end": v(790, 1564.62) * mm});
            skLineSegment(sketch, "E1050.MirrorCS", {"start": v(160, 1304.81) * mm, "end": v(90, 1345.23) * mm});
            skLineSegment(sketch, "E1051.MirrorCS", {"start": v(-80, 1443.38) * mm, "end": v(-150, 1483.8) * mm});
            skLineSegment(sketch, "E1052.MirrorCS", {"start": v(330, 1760.92) * mm, "end": v(330, 1841.75) * mm});
            skLineSegment(sketch, "E1053.MirrorCS", {"start": v(470, 1287.5) * mm, "end": v(470, 1206.66) * mm});
            skLineSegment(sketch, "E1054.MirrorCS", {"start": v(880, 1166.25) * mm, "end": v(810, 1206.66) * mm});
            skLineSegment(sketch, "E1055.MirrorCS", {"start": v(890, 1426.06) * mm, "end": v(890, 1345.23) * mm});
            skLineSegment(sketch, "E1056.MirrorCS", {"start": v(1050, 1703.18) * mm, "end": v(1050, 1622.35) * mm});
            skLineSegment(sketch, "E1057.MirrorCS", {"start": v(890, 1345.23) * mm, "end": v(960, 1304.81) * mm});
            skLineSegment(sketch, "E1058.MirrorCS", {"start": v(1110, 1841.75) * mm, "end": v(1110, 1760.92) * mm});
            skLineSegment(sketch, "E1059.MirrorCS", {"start": v(470, 1760.92) * mm, "end": v(400, 1720.5) * mm});
            skLineSegment(sketch, "E1060.MirrorCS", {"start": v(1190, 1622.35) * mm, "end": v(1120, 1581.94) * mm});
            skLineSegment(sketch, "E1061.MirrorCS", {"start": v(-560, 1605.03) * mm, "end": v(-490, 1564.62) * mm});
            skLineSegment(sketch, "E1062.MirrorCS", {"start": v(-790, 1287.5) * mm, "end": v(-790, 1206.66) * mm});
            skLineSegment(sketch, "E1063.MirrorCS", {"start": v(-390, 1345.23) * mm, "end": v(-320, 1304.81) * mm});
            skLineSegment(sketch, "E1064.MirrorCS", {"start": v(-560, 1166.25) * mm, "end": v(-490, 1206.66) * mm});
            skLineSegment(sketch, "E1065.MirrorCS", {"start": v(320, 1304.81) * mm, "end": v(390, 1345.23) * mm});
            skLineSegment(sketch, "E1066.MirrorCS", {"start": v(-320, 1581.94) * mm, "end": v(-390, 1622.35) * mm});
            skLineSegment(sketch, "E1067.MirrorCS", {"start": v(-250, 1703.18) * mm, "end": v(-250, 1622.35) * mm});
            skLineSegment(sketch, "E1068.MirrorCS", {"start": v(-480, 1189.34) * mm, "end": v(-550, 1148.93) * mm});
            skLineSegment(sketch, "E1069.MirrorCS", {"start": v(390, 1622.35) * mm, "end": v(320, 1581.94) * mm});
            skLineSegment(sketch, "E1070.MirrorCS", {"start": v(960, 1581.94) * mm, "end": v(890, 1622.35) * mm});
            skLineSegment(sketch, "E1071.MirrorCS", {"start": v(1110, 1564.62) * mm, "end": v(1040, 1605.03) * mm});
            skLineSegment(sketch, "E1072.MirrorCS", {"start": v(-320, 1466.47) * mm, "end": v(-390, 1426.06) * mm});
            skLineSegment(sketch, "E1073.MirrorCS", {"start": v(880, 1605.03) * mm, "end": v(810, 1564.62) * mm});
            skLineSegment(sketch, "E1074.MirrorCS", {"start": v(0, 1743.6) * mm, "end": v(70, 1703.18) * mm});
            skLineSegment(sketch, "E1075.MirrorCS", {"start": v(880, 1882.16) * mm, "end": v(810, 1841.75) * mm});
            skLineSegment(sketch, "E1076.MirrorCS", {"start": v(170, 1206.66) * mm, "end": v(170, 1287.5) * mm});
            skLineSegment(sketch, "E1077.MirrorCS", {"start": v(-150, 1206.66) * mm, "end": v(-80, 1166.25) * mm});
            skLineSegment(sketch, "E1078.MirrorCS", {"start": v(0, 1581.94) * mm, "end": v(-70, 1622.35) * mm});
            skLineSegment(sketch, "E1079.MirrorCS", {"start": v(160, 1743.6) * mm, "end": v(90, 1703.18) * mm});
            skLineSegment(sketch, "E1080.MirrorCS", {"start": v(1030, 1345.23) * mm, "end": v(1030, 1426.06) * mm});
            skLineSegment(sketch, "E1081.MirrorCS", {"start": v(710, 1622.35) * mm, "end": v(640, 1581.94) * mm});
            skLineSegment(sketch, "E1082.MirrorCS", {"start": v(650, 1564.62) * mm, "end": v(720, 1605.03) * mm});
            skLineSegment(sketch, "E1083.MirrorCS", {"start": v(570, 1426.06) * mm, "end": v(640, 1466.47) * mm});
            skLineSegment(sketch, "E1084.MirrorCS", {"start": v(230, 1426.06) * mm, "end": v(230, 1345.23) * mm});
            skLineSegment(sketch, "E1085.MirrorCS", {"start": v(-80, 1720.5) * mm, "end": v(-10, 1760.92) * mm});
            skLineSegment(sketch, "E1086.MirrorCS", {"start": v(-630, 1483.8) * mm, "end": v(-560, 1443.38) * mm});
            skLineSegment(sketch, "E1087.MirrorCS", {"start": v(-630, 1287.5) * mm, "end": v(-630, 1206.66) * mm});
            skLineSegment(sketch, "E1088.MirrorCS", {"start": v(80, 1720.5) * mm, "end": v(150, 1760.92) * mm});
            skLineSegment(sketch, "E1089.MirrorCS", {"start": v(560, 1327.9) * mm, "end": v(630, 1287.5) * mm});
            skLineSegment(sketch, "E1090.MirrorCS", {"start": v(-400, 1166.25) * mm, "end": v(-470, 1206.66) * mm});
            skLineSegment(sketch, "E1091.MirrorCS", {"start": v(570, 1148.93) * mm, "end": v(640, 1189.34) * mm});
            skLineSegment(sketch, "E1092.MirrorCS", {"start": v(-330, 1287.5) * mm, "end": v(-400, 1327.9) * mm});
            skLineSegment(sketch, "E1093.MirrorCS", {"start": v(1120, 1304.81) * mm, "end": v(1050, 1345.23) * mm});
            skLineSegment(sketch, "E1094.MirrorCS", {"start": v(1110, 1483.8) * mm, "end": v(1110, 1564.62) * mm});
            skLineSegment(sketch, "E1095.MirrorCS", {"start": v(-410, 1622.35) * mm, "end": v(-480, 1581.94) * mm});
            skLineSegment(sketch, "E1096.MirrorCS", {"start": v(960, 1304.81) * mm, "end": v(1030, 1345.23) * mm});
            skLineSegment(sketch, "E1097.MirrorCS", {"start": v(-630, 1760.92) * mm, "end": v(-560, 1720.5) * mm});
            skLineSegment(sketch, "E1098.MirrorCS", {"start": v(-650, 1483.8) * mm, "end": v(-720, 1443.38) * mm});
            skLineSegment(sketch, "E1099.MirrorCS", {"start": v(880, 1443.38) * mm, "end": v(810, 1483.8) * mm});
            skLineSegment(sketch, "E1100.MirrorCS", {"start": v(10, 1483.8) * mm, "end": v(10, 1564.62) * mm});
            skLineSegment(sketch, "E1101.MirrorCS", {"start": v(1130, 1483.8) * mm, "end": v(1130, 1564.62) * mm});
            skLineSegment(sketch, "E1102.MirrorCS", {"start": v(550, 1345.23) * mm, "end": v(480, 1304.81) * mm});
            skLineSegment(sketch, "E1103.MirrorCS", {"start": v(1050, 1426.06) * mm, "end": v(1120, 1466.47) * mm});
            skLineSegment(sketch, "E1104.MirrorCS", {"start": v(-400, 1720.5) * mm, "end": v(-470, 1760.92) * mm});
            skLineSegment(sketch, "E1105.MirrorCS", {"start": v(-480, 1466.47) * mm, "end": v(-410, 1426.06) * mm});
            skLineSegment(sketch, "E1106.MirrorCS", {"start": v(310, 1206.66) * mm, "end": v(240, 1166.25) * mm});
            skLineSegment(sketch, "E1107.MirrorCS", {"start": v(1040, 1720.5) * mm, "end": v(970, 1760.92) * mm});
            skLineSegment(sketch, "E1108.MirrorCS", {"start": v(170, 1564.62) * mm, "end": v(170, 1483.8) * mm});
            skLineSegment(sketch, "E1109.MirrorCS", {"start": v(-80, 1166.25) * mm, "end": v(-10, 1206.66) * mm});
            skLineSegment(sketch, "E1110.MirrorCS", {"start": v(1030, 1622.35) * mm, "end": v(960, 1581.94) * mm});
            skLineSegment(sketch, "E1111.MirrorCS", {"start": v(-170, 1841.75) * mm, "end": v(-170, 1760.92) * mm});
            skLineSegment(sketch, "E1112.MirrorCS", {"start": v(470, 1841.75) * mm, "end": v(400, 1882.16) * mm});
            skLineSegment(sketch, "E1113.MirrorCS", {"start": v(1190, 1622.35) * mm, "end": v(1190, 1703.18) * mm});
            skLineSegment(sketch, "E1114.MirrorCS", {"start": v(10, 1287.5) * mm, "end": v(10, 1206.66) * mm});
            skLineSegment(sketch, "E1115.MirrorCS", {"start": v(490, 1483.8) * mm, "end": v(560, 1443.38) * mm});
            skLineSegment(sketch, "E1116.MirrorCS", {"start": v(-710, 1345.23) * mm, "end": v(-640, 1304.81) * mm});
            skLineSegment(sketch, "E1117.MirrorCS", {"start": v(-310, 1206.66) * mm, "end": v(-310, 1287.5) * mm});
            skLineSegment(sketch, "E1118.MirrorCS", {"start": v(-470, 1841.75) * mm, "end": v(-400, 1882.16) * mm});
            skLineSegment(sketch, "E1119.MirrorCS", {"start": v(950, 1483.8) * mm, "end": v(950, 1564.62) * mm});
            skLineSegment(sketch, "E1120.MirrorCS", {"start": v(10, 1206.66) * mm, "end": v(80, 1166.25) * mm});
            skLineSegment(sketch, "E1121.MirrorCS", {"start": v(-470, 1760.92) * mm, "end": v(-470, 1841.75) * mm});
            skLineSegment(sketch, "E1122.MirrorCS", {"start": v(970, 1206.66) * mm, "end": v(970, 1287.5) * mm});
            skLineSegment(sketch, "E1123.MirrorCS", {"start": v(-650, 1287.5) * mm, "end": v(-720, 1327.9) * mm});
            skLineSegment(sketch, "E1124.MirrorCS", {"start": v(650, 1287.5) * mm, "end": v(720, 1327.9) * mm});
            skLineSegment(sketch, "E1125.MirrorCS", {"start": v(880, 1327.9) * mm, "end": v(810, 1287.5) * mm});
            skLineSegment(sketch, "E1126.MirrorCS", {"start": v(230, 1703.18) * mm, "end": v(160, 1743.6) * mm});
            skLineSegment(sketch, "E1127.MirrorCS", {"start": v(790, 1760.92) * mm, "end": v(790, 1841.75) * mm});
            skLineSegment(sketch, "E1128.MirrorCS", {"start": v(170, 1483.8) * mm, "end": v(240, 1443.38) * mm});
            skLineSegment(sketch, "E1129.MirrorCS", {"start": v(-90, 1703.18) * mm, "end": v(-160, 1743.6) * mm});
            skLineSegment(sketch, "E1130.MirrorCS", {"start": v(80, 1443.38) * mm, "end": v(150, 1483.8) * mm});
            skLineSegment(sketch, "E1131.MirrorCS", {"start": v(1120, 1743.6) * mm, "end": v(1050, 1703.18) * mm});
            skLineSegment(sketch, "E1132.MirrorCS", {"start": v(240, 1327.9) * mm, "end": v(170, 1287.5) * mm});
            skLineSegment(sketch, "E1133.MirrorCS", {"start": v(-570, 1703.18) * mm, "end": v(-570, 1622.35) * mm});
            skLineSegment(sketch, "E1134.MirrorCS", {"start": v(790, 1287.5) * mm, "end": v(720, 1327.9) * mm});
            skLineSegment(sketch, "E1135.MirrorCS", {"start": v(1050, 1622.35) * mm, "end": v(1120, 1581.94) * mm});
            skLineSegment(sketch, "E1136.MirrorCS", {"start": v(1040, 1605.03) * mm, "end": v(970, 1564.62) * mm});
            skLineSegment(sketch, "E1137.MirrorCS", {"start": v(70, 1703.18) * mm, "end": v(70, 1622.35) * mm});
            skLineSegment(sketch, "E1138.MirrorCS", {"start": v(-410, 1148.93) * mm, "end": v(-480, 1189.34) * mm});
            skLineSegment(sketch, "E1139.MirrorCS", {"start": v(1130, 1206.66) * mm, "end": v(1190, 1172.02) * mm});
            skLineSegment(sketch, "E1140.MirrorCS", {"start": v(-330, 1841.75) * mm, "end": v(-330, 1760.92) * mm});
            skLineSegment(sketch, "E1141.MirrorCS", {"start": v(480, 1466.47) * mm, "end": v(550, 1426.06) * mm});
            skLineSegment(sketch, "E1142.MirrorCS", {"start": v(-640, 1466.47) * mm, "end": v(-570, 1426.06) * mm});
            skLineSegment(sketch, "E1143.MirrorCS", {"start": v(880, 1443.38) * mm, "end": v(950, 1483.8) * mm});
            skLineSegment(sketch, "E1144.MirrorCS", {"start": v(-490, 1483.8) * mm, "end": v(-560, 1443.38) * mm});
            skLineSegment(sketch, "E1145.MirrorCS", {"start": v(-790, 1287.5) * mm, "end": v(-720, 1327.9) * mm});
            skLineSegment(sketch, "E1146.MirrorCS", {"start": v(-410, 1426.06) * mm, "end": v(-410, 1345.23) * mm});
            skLineSegment(sketch, "E1147.MirrorCS", {"start": v(1040, 1882.16) * mm, "end": v(1110, 1841.75) * mm});
            skLineSegment(sketch, "E1148.MirrorCS", {"start": v(800, 1743.6) * mm, "end": v(730, 1703.18) * mm});
            skLineSegment(sketch, "E1149.MirrorCS", {"start": v(-410, 1345.23) * mm, "end": v(-480, 1304.81) * mm});
            skLineSegment(sketch, "E1150.MirrorCS", {"start": v(490, 1841.75) * mm, "end": v(560, 1882.16) * mm});
            skLineSegment(sketch, "E1151.MirrorCS", {"start": v(630, 1206.66) * mm, "end": v(630, 1287.5) * mm});
            skLineSegment(sketch, "E1152.MirrorCS", {"start": v(-710, 1622.35) * mm, "end": v(-710, 1703.18) * mm});
            skLineSegment(sketch, "E1153.MirrorCS", {"start": v(570, 1703.18) * mm, "end": v(640, 1743.6) * mm});
            skLineSegment(sketch, "E1154.MirrorCS", {"start": v(-70, 1148.93) * mm, "end": v(0, 1189.34) * mm});
            skLineSegment(sketch, "E1155.MirrorCS", {"start": v(880, 1720.5) * mm, "end": v(810, 1760.92) * mm});
            skLineSegment(sketch, "E1156.MirrorCS", {"start": v(-170, 1564.62) * mm, "end": v(-240, 1605.03) * mm});
            skLineSegment(sketch, "E1157.MirrorCS", {"start": v(570, 1345.23) * mm, "end": v(640, 1304.81) * mm});
            skLineSegment(sketch, "E1158.MirrorCS", {"start": v(400, 1327.9) * mm, "end": v(330, 1287.5) * mm});
            skLineSegment(sketch, "E1159.MirrorCS", {"start": v(-170, 1483.8) * mm, "end": v(-170, 1564.62) * mm});
            skLineSegment(sketch, "E1160.MirrorCS", {"start": v(310, 1287.5) * mm, "end": v(240, 1327.9) * mm});
            skLineSegment(sketch, "E1161.MirrorCS", {"start": v(-160, 1743.6) * mm, "end": v(-230, 1703.18) * mm});
            skLineSegment(sketch, "E1162.MirrorCS", {"start": v(90, 1426.06) * mm, "end": v(160, 1466.47) * mm});
            skLineSegment(sketch, "E1163.MirrorCS", {"start": v(810, 1760.92) * mm, "end": v(810, 1841.75) * mm});
            skLineSegment(sketch, "E1164.MirrorCS", {"start": v(410, 1426.06) * mm, "end": v(480, 1466.47) * mm});
            skLineSegment(sketch, "E1165.MirrorCS", {"start": v(310, 1564.62) * mm, "end": v(240, 1605.03) * mm});
            skLineSegment(sketch, "E1166.MirrorCS", {"start": v(490, 1287.5) * mm, "end": v(490, 1206.66) * mm});
            skLineSegment(sketch, "E1167.MirrorCS", {"start": v(630, 1564.62) * mm, "end": v(630, 1483.8) * mm});
            skLineSegment(sketch, "E1168.MirrorCS", {"start": v(-720, 1443.38) * mm, "end": v(-790, 1483.8) * mm});
            skLineSegment(sketch, "E1169.MirrorCS", {"start": v(-390, 1703.18) * mm, "end": v(-320, 1743.6) * mm});
            skLineSegment(sketch, "E1170.MirrorCS", {"start": v(730, 1622.35) * mm, "end": v(800, 1581.94) * mm});
            skLineSegment(sketch, "E1171.MirrorCS", {"start": v(560, 1327.9) * mm, "end": v(490, 1287.5) * mm});
            skLineSegment(sketch, "E1172.MirrorCS", {"start": v(1050, 1345.23) * mm, "end": v(1050, 1426.06) * mm});
            skLineSegment(sketch, "E1173.MirrorCS", {"start": v(550, 1703.18) * mm, "end": v(480, 1743.6) * mm});
            skLineSegment(sketch, "E1174.MirrorCS", {"start": v(-550, 1703.18) * mm, "end": v(-550, 1622.35) * mm});
            skLineSegment(sketch, "E1175.MirrorCS", {"start": v(950, 1287.5) * mm, "end": v(950, 1206.66) * mm});
            skLineSegment(sketch, "E1176.MirrorCS", {"start": v(-230, 1622.35) * mm, "end": v(-160, 1581.94) * mm});
            skLineSegment(sketch, "E1177.MirrorCS", {"start": v(230, 1345.23) * mm, "end": v(160, 1304.81) * mm});
            skLineSegment(sketch, "E1178.MirrorCS", {"start": v(-560, 1327.9) * mm, "end": v(-490, 1287.5) * mm});
            skLineSegment(sketch, "E1179.MirrorCS", {"start": v(-160, 1189.34) * mm, "end": v(-230, 1148.93) * mm});
            skLineSegment(sketch, "E1180.MirrorCS", {"start": v(970, 1564.62) * mm, "end": v(970, 1483.8) * mm});
            skLineSegment(sketch, "E1181.MirrorCS", {"start": v(400, 1882.16) * mm, "end": v(330, 1841.75) * mm});
            skLineSegment(sketch, "E1182.MirrorCS", {"start": v(-90, 1622.35) * mm, "end": v(-160, 1581.94) * mm});
            skLineSegment(sketch, "E1183.MirrorCS", {"start": v(-790, 1483.8) * mm, "end": v(-790, 1564.62) * mm});
            skLineSegment(sketch, "E1184.MirrorCS", {"start": v(-480, 1743.6) * mm, "end": v(-550, 1703.18) * mm});
            skLineSegment(sketch, "E1185.MirrorCS", {"start": v(1190, 1426.06) * mm, "end": v(1120, 1466.47) * mm});
            skLineSegment(sketch, "E1186.MirrorCS", {"start": v(-240, 1605.03) * mm, "end": v(-310, 1564.62) * mm});
            skLineSegment(sketch, "E1187.MirrorCS", {"start": v(-170, 1760.92) * mm, "end": v(-240, 1720.5) * mm});
            skLineSegment(sketch, "E1188.MirrorCS", {"start": v(-230, 1426.06) * mm, "end": v(-160, 1466.47) * mm});
            skLineSegment(sketch, "E1189.MirrorCS", {"start": v(-390, 1148.93) * mm, "end": v(-320, 1189.34) * mm});
            skLineSegment(sketch, "E1190.MirrorCS", {"start": v(150, 1564.62) * mm, "end": v(150, 1483.8) * mm});
            skLineSegment(sketch, "E1191.MirrorCS", {"start": v(-560, 1882.16) * mm, "end": v(-630, 1841.75) * mm});
            skLineSegment(sketch, "E1192.MirrorCS", {"start": v(800, 1189.34) * mm, "end": v(730, 1148.93) * mm});
            skLineSegment(sketch, "E1193.MirrorCS", {"start": v(1130, 1287.5) * mm, "end": v(1130, 1206.66) * mm});
            skLineSegment(sketch, "E1194.MirrorCS", {"start": v(1130, 1564.62) * mm, "end": v(1190, 1599.26) * mm});
            skLineSegment(sketch, "E1195.MirrorCS", {"start": v(0, 1304.81) * mm, "end": v(70, 1345.23) * mm});
            skLineSegment(sketch, "E1196.MirrorCS", {"start": v(-240, 1166.25) * mm, "end": v(-310, 1206.66) * mm});
            skLineSegment(sketch, "E1197.MirrorCS", {"start": v(950, 1206.66) * mm, "end": v(880, 1166.25) * mm});
            skLineSegment(sketch, "E1198.MirrorCS", {"start": v(80, 1882.16) * mm, "end": v(10, 1841.75) * mm});
            skLineSegment(sketch, "E1199.MirrorCS", {"start": v(870, 1426.06) * mm, "end": v(870, 1345.23) * mm});
            skLineSegment(sketch, "E1200.MirrorCS", {"start": v(-790, 1206.66) * mm, "end": v(-720, 1166.25) * mm});
            skLineSegment(sketch, "E1201.MirrorCS", {"start": v(-630, 1206.66) * mm, "end": v(-560, 1166.25) * mm});
            skLineSegment(sketch, "E1202.MirrorCS", {"start": v(390, 1345.23) * mm, "end": v(390, 1426.06) * mm});
            skLineSegment(sketch, "E1203.MirrorCS", {"start": v(640, 1743.6) * mm, "end": v(710, 1703.18) * mm});
            skLineSegment(sketch, "E1204.MirrorCS", {"start": v(-720, 1720.5) * mm, "end": v(-650, 1760.92) * mm});
            skLineSegment(sketch, "E1205.MirrorCS", {"start": v(-560, 1720.5) * mm, "end": v(-490, 1760.92) * mm});
            skLineSegment(sketch, "E1206.MirrorCS", {"start": v(650, 1841.75) * mm, "end": v(650, 1760.92) * mm});
            skLineSegment(sketch, "E1207.MirrorCS", {"start": v(80, 1166.25) * mm, "end": v(150, 1206.66) * mm});
            skLineSegment(sketch, "E1208.MirrorCS", {"start": v(-90, 1345.23) * mm, "end": v(-160, 1304.81) * mm});
            skLineSegment(sketch, "E1209.MirrorCS", {"start": v(1190, 1345.23) * mm, "end": v(1120, 1304.81) * mm});
            skLineSegment(sketch, "E1210.MirrorCS", {"start": v(250, 1426.06) * mm, "end": v(320, 1466.47) * mm});
            skLineSegment(sketch, "E1211.MirrorCS", {"start": v(-640, 1581.94) * mm, "end": v(-710, 1622.35) * mm});
            skLineSegment(sketch, "E1212.MirrorCS", {"start": v(240, 1605.03) * mm, "end": v(170, 1564.62) * mm});
            skLineSegment(sketch, "E1213.MirrorCS", {"start": v(-150, 1564.62) * mm, "end": v(-80, 1605.03) * mm});
            skLineSegment(sketch, "E1214.MirrorCS", {"start": v(-320, 1743.6) * mm, "end": v(-250, 1703.18) * mm});
            skLineSegment(sketch, "E1215.MirrorCS", {"start": v(870, 1345.23) * mm, "end": v(800, 1304.81) * mm});
            skLineSegment(sketch, "E1216.MirrorCS", {"start": v(-640, 1304.81) * mm, "end": v(-570, 1345.23) * mm});
            skLineSegment(sketch, "E1217.MirrorCS", {"start": v(730, 1703.18) * mm, "end": v(730, 1622.35) * mm});
            skLineSegment(sketch, "E1218.MirrorCS", {"start": v(-310, 1564.62) * mm, "end": v(-310, 1483.8) * mm});
            skLineSegment(sketch, "E1219.MirrorCS", {"start": v(730, 1345.23) * mm, "end": v(730, 1426.06) * mm});
            skLineSegment(sketch, "E1220.MirrorCS", {"start": v(480, 1743.6) * mm, "end": v(410, 1703.18) * mm});
            skLineSegment(sketch, "E1221.MirrorCS", {"start": v(390, 1703.18) * mm, "end": v(390, 1622.35) * mm});
            skLineSegment(sketch, "E1222.MirrorCS", {"start": v(470, 1483.8) * mm, "end": v(470, 1564.62) * mm});
            skLineSegment(sketch, "E1223.MirrorCS", {"start": v(550, 1148.93) * mm, "end": v(480, 1189.34) * mm});
            skLineSegment(sketch, "E1224.MirrorCS", {"start": v(90, 1703.18) * mm, "end": v(90, 1622.35) * mm});
            skLineSegment(sketch, "E1225.MirrorCS", {"start": v(10, 1841.75) * mm, "end": v(10, 1760.92) * mm});
            skLineSegment(sketch, "E1226.MirrorCS", {"start": v(-10, 1564.62) * mm, "end": v(-10, 1483.8) * mm});
            skLineSegment(sketch, "E1227.MirrorCS", {"start": v(310, 1483.8) * mm, "end": v(310, 1564.62) * mm});
            skLineSegment(sketch, "E1228.MirrorCS", {"start": v(970, 1287.5) * mm, "end": v(1040, 1327.9) * mm});
            skLineSegment(sketch, "E1229.MirrorCS", {"start": v(-90, 1148.93) * mm, "end": v(-160, 1189.34) * mm});
            skLineSegment(sketch, "E1230.MirrorCS", {"start": v(320, 1743.6) * mm, "end": v(390, 1703.18) * mm});
            skLineSegment(sketch, "E1231.MirrorCS", {"start": v(-650, 1564.62) * mm, "end": v(-650, 1483.8) * mm});
            skLineSegment(sketch, "E1232.MirrorCS", {"start": v(150, 1760.92) * mm, "end": v(150, 1841.75) * mm});
            skLineSegment(sketch, "E1233.MirrorCS", {"start": v(-80, 1605.03) * mm, "end": v(-10, 1564.62) * mm});
            skLineSegment(sketch, "E1234.MirrorCS", {"start": v(-560, 1327.9) * mm, "end": v(-630, 1287.5) * mm});
            skLineSegment(sketch, "E1235.MirrorCS", {"start": v(1190, 1426.06) * mm, "end": v(1190, 1345.23) * mm});
            skLineSegment(sketch, "E1236.MirrorCS", {"start": v(1120, 1189.34) * mm, "end": v(1050, 1148.93) * mm});
            skLineSegment(sketch, "E1237.MirrorCS", {"start": v(230, 1148.93) * mm, "end": v(160, 1189.34) * mm});
            skLineSegment(sketch, "E1238.MirrorCS", {"start": v(-70, 1703.18) * mm, "end": v(0, 1743.6) * mm});
            skLineSegment(sketch, "E1239.MirrorCS", {"start": v(250, 1622.35) * mm, "end": v(320, 1581.94) * mm});
            skLineSegment(sketch, "E1240.MirrorCS", {"start": v(410, 1345.23) * mm, "end": v(410, 1426.06) * mm});
            skLineSegment(sketch, "E1241.MirrorCS", {"start": v(810, 1206.66) * mm, "end": v(810, 1287.5) * mm});
            skLineSegment(sketch, "E1242.MirrorCS", {"start": v(-790, 1841.75) * mm, "end": v(-790, 1760.92) * mm});
            skLineSegment(sketch, "E1243.MirrorCS", {"start": v(-470, 1483.8) * mm, "end": v(-400, 1443.38) * mm});
            skLineSegment(sketch, "E1244.MirrorCS", {"start": v(650, 1287.5) * mm, "end": v(650, 1206.66) * mm});
            skLineSegment(sketch, "E1245.MirrorCS", {"start": v(320, 1189.34) * mm, "end": v(390, 1148.93) * mm});
            skLineSegment(sketch, "E1246.MirrorCS", {"start": v(-400, 1327.9) * mm, "end": v(-470, 1287.5) * mm});
            skLineSegment(sketch, "E1247.MirrorCS", {"start": v(410, 1622.35) * mm, "end": v(480, 1581.94) * mm});
            skLineSegment(sketch, "E1248.MirrorCS", {"start": v(-80, 1882.16) * mm, "end": v(-150, 1841.75) * mm});
            skLineSegment(sketch, "E1249.MirrorCS", {"start": v(-80, 1443.38) * mm, "end": v(-10, 1483.8) * mm});
            skLineSegment(sketch, "E1250.MirrorCS", {"start": v(-330, 1483.8) * mm, "end": v(-330, 1564.62) * mm});
            skLineSegment(sketch, "E1251.MirrorCS", {"start": v(160, 1189.34) * mm, "end": v(90, 1148.93) * mm});
            skLineSegment(sketch, "E1252.MirrorCS", {"start": v(1110, 1760.92) * mm, "end": v(1040, 1720.5) * mm});
            skLineSegment(sketch, "E1253.MirrorCS", {"start": v(-90, 1426.06) * mm, "end": v(-160, 1466.47) * mm});
            skLineSegment(sketch, "E1254.MirrorCS", {"start": v(150, 1206.66) * mm, "end": v(150, 1287.5) * mm});
            skLineSegment(sketch, "E1255.MirrorCS", {"start": v(-720, 1605.03) * mm, "end": v(-650, 1564.62) * mm});
            skLineSegment(sketch, "E1256.MirrorCS", {"start": v(-10, 1206.66) * mm, "end": v(-10, 1287.5) * mm});
            skLineSegment(sketch, "E1257.MirrorCS", {"start": v(-390, 1622.35) * mm, "end": v(-390, 1703.18) * mm});
            skLineSegment(sketch, "E1258.MirrorCS", {"start": v(310, 1760.92) * mm, "end": v(240, 1720.5) * mm});
            skLineSegment(sketch, "E1259.MirrorCS", {"start": v(790, 1206.66) * mm, "end": v(790, 1287.5) * mm});
            skLineSegment(sketch, "E1260.MirrorCS", {"start": v(10, 1564.62) * mm, "end": v(80, 1605.03) * mm});
            skLineSegment(sketch, "E1261.MirrorCS", {"start": v(-650, 1206.66) * mm, "end": v(-650, 1287.5) * mm});
            skLineSegment(sketch, "E1262.MirrorCS", {"start": v(950, 1841.75) * mm, "end": v(950, 1760.92) * mm});
            skLineSegment(sketch, "E1263.MirrorCS", {"start": v(-480, 1304.81) * mm, "end": v(-550, 1345.23) * mm});
            skLineSegment(sketch, "E1264.MirrorCS", {"start": v(250, 1426.06) * mm, "end": v(250, 1345.23) * mm});
            skLineSegment(sketch, "E1265.MirrorCS", {"start": v(550, 1622.35) * mm, "end": v(550, 1703.18) * mm});
            skLineSegment(sketch, "E1266.MirrorCS", {"start": v(-80, 1327.9) * mm, "end": v(-150, 1287.5) * mm});
            skLineSegment(sketch, "E1267.MirrorCS", {"start": v(1030, 1703.18) * mm, "end": v(1030, 1622.35) * mm});
            skLineSegment(sketch, "E1268.MirrorCS", {"start": v(1110, 1483.8) * mm, "end": v(1040, 1443.38) * mm});
            skLineSegment(sketch, "E1269.MirrorCS", {"start": v(1040, 1166.25) * mm, "end": v(970, 1206.66) * mm});
            skLineSegment(sketch, "E1270.MirrorCS", {"start": v(310, 1483.8) * mm, "end": v(240, 1443.38) * mm});
            skLineSegment(sketch, "E1271.MirrorCS", {"start": v(480, 1189.34) * mm, "end": v(410, 1148.93) * mm});
            skLineSegment(sketch, "E1272.MirrorCS", {"start": v(-710, 1426.06) * mm, "end": v(-640, 1466.47) * mm});
            skLineSegment(sketch, "E1273.MirrorCS", {"start": v(-410, 1622.35) * mm, "end": v(-410, 1703.18) * mm});
            skLineSegment(sketch, "E1274.MirrorCS", {"start": v(400, 1720.5) * mm, "end": v(330, 1760.92) * mm});
            skLineSegment(sketch, "E1275.MirrorCS", {"start": v(640, 1581.94) * mm, "end": v(570, 1622.35) * mm});
            skLineSegment(sketch, "E1276.MirrorCS", {"start": v(390, 1426.06) * mm, "end": v(320, 1466.47) * mm});
            skLineSegment(sketch, "E1277.MirrorCS", {"start": v(1110, 1287.5) * mm, "end": v(1110, 1206.66) * mm});
            skLineSegment(sketch, "E1278.MirrorCS", {"start": v(-640, 1189.34) * mm, "end": v(-570, 1148.93) * mm});
            skLineSegment(sketch, "E1279.MirrorCS", {"start": v(-490, 1206.66) * mm, "end": v(-490, 1287.5) * mm});
            skLineSegment(sketch, "E1280.MirrorCS", {"start": v(880, 1882.16) * mm, "end": v(950, 1841.75) * mm});
            skLineSegment(sketch, "E1281.MirrorCS", {"start": v(-490, 1841.75) * mm, "end": v(-560, 1882.16) * mm});
            skLineSegment(sketch, "E1282.MirrorCS", {"start": v(-790, 1760.92) * mm, "end": v(-720, 1720.5) * mm});
            skLineSegment(sketch, "E1283.MirrorCS", {"start": v(950, 1564.62) * mm, "end": v(880, 1605.03) * mm});
            skLineSegment(sketch, "E1284.MirrorCS", {"start": v(-310, 1483.8) * mm, "end": v(-240, 1443.38) * mm});
            skLineSegment(sketch, "E1285.MirrorCS", {"start": v(-470, 1206.66) * mm, "end": v(-470, 1287.5) * mm});
            skLineSegment(sketch, "E1286.MirrorCS", {"start": v(250, 1703.18) * mm, "end": v(320, 1743.6) * mm});
            skLineSegment(sketch, "E1287.MirrorCS", {"start": v(-250, 1622.35) * mm, "end": v(-320, 1581.94) * mm});
            skLineSegment(sketch, "E1288.MirrorCS", {"start": v(630, 1841.75) * mm, "end": v(560, 1882.16) * mm});
            skLineSegment(sketch, "E1289.MirrorCS", {"start": v(-70, 1622.35) * mm, "end": v(-70, 1703.18) * mm});
            skLineSegment(sketch, "E1290.MirrorCS", {"start": v(-400, 1605.03) * mm, "end": v(-470, 1564.62) * mm});
            skLineSegment(sketch, "E1291.MirrorCS", {"start": v(-330, 1760.92) * mm, "end": v(-400, 1720.5) * mm});
            skLineSegment(sketch, "E1292.MirrorCS", {"start": v(-480, 1581.94) * mm, "end": v(-550, 1622.35) * mm});
            skLineSegment(sketch, "E1293.MirrorCS", {"start": v(10, 1760.92) * mm, "end": v(80, 1720.5) * mm});
            skLineSegment(sketch, "E1294.MirrorCS", {"start": v(1030, 1426.06) * mm, "end": v(960, 1466.47) * mm});
            skLineSegment(sketch, "E1295.MirrorCS", {"start": v(960, 1466.47) * mm, "end": v(890, 1426.06) * mm});
            skLineSegment(sketch, "E1296.MirrorCS", {"start": v(-320, 1189.34) * mm, "end": v(-250, 1148.93) * mm});
            skLineSegment(sketch, "E1297.MirrorCS", {"start": v(80, 1327.9) * mm, "end": v(150, 1287.5) * mm});
            skLineSegment(sketch, "E1298.MirrorCS", {"start": v(230, 1622.35) * mm, "end": v(160, 1581.94) * mm});
            skLineSegment(sketch, "E1299.MirrorCS", {"start": v(-650, 1760.92) * mm, "end": v(-650, 1841.75) * mm});
            skLineSegment(sketch, "E1300.MirrorCS", {"start": v(-630, 1483.8) * mm, "end": v(-630, 1564.62) * mm});
            skLineSegment(sketch, "E1301.MirrorCS", {"start": v(970, 1483.8) * mm, "end": v(1040, 1443.38) * mm});
            skLineSegment(sketch, "E1302.MirrorCS", {"start": v(800, 1581.94) * mm, "end": v(870, 1622.35) * mm});
            skLineSegment(sketch, "E1303.MirrorCS", {"start": v(0, 1189.34) * mm, "end": v(70, 1148.93) * mm});
            skLineSegment(sketch, "E1304.MirrorCS", {"start": v(550, 1426.06) * mm, "end": v(550, 1345.23) * mm});
            skLineSegment(sketch, "E1305.MirrorCS", {"start": v(800, 1466.47) * mm, "end": v(870, 1426.06) * mm});
            skLineSegment(sketch, "E1306.MirrorCS", {"start": v(1190, 1703.18) * mm, "end": v(1120, 1743.6) * mm});
            skLineSegment(sketch, "E1307.MirrorCS", {"start": v(70, 1426.06) * mm, "end": v(0, 1466.47) * mm});
            skLineSegment(sketch, "E1308.MirrorCS", {"start": v(-400, 1443.38) * mm, "end": v(-330, 1483.8) * mm});
            skLineSegment(sketch, "E1309.MirrorCS", {"start": v(-170, 1206.66) * mm, "end": v(-240, 1166.25) * mm});
            skLineSegment(sketch, "E1310.MirrorCS", {"start": v(800, 1304.81) * mm, "end": v(730, 1345.23) * mm});
            skLineSegment(sketch, "E1311.MirrorCS", {"start": v(-640, 1743.6) * mm, "end": v(-570, 1703.18) * mm});
            skLineSegment(sketch, "E1312.MirrorCS", {"start": v(-730, 1426.06) * mm, "end": v(-730, 1345.23) * mm});
            skLineSegment(sketch, "E1313.MirrorCS", {"start": v(-310, 1841.75) * mm, "end": v(-240, 1882.16) * mm});
            skLineSegment(sketch, "E1314.MirrorCS", {"start": v(0, 1466.47) * mm, "end": v(-70, 1426.06) * mm});
            skLineSegment(sketch, "E1315.MirrorCS", {"start": v(550, 1622.35) * mm, "end": v(480, 1581.94) * mm});
            skLineSegment(sketch, "E1316.MirrorCS", {"start": v(-310, 1760.92) * mm, "end": v(-310, 1841.75) * mm});
            skLineSegment(sketch, "E1317.MirrorCS", {"start": v(720, 1720.5) * mm, "end": v(790, 1760.92) * mm});
            skLineSegment(sketch, "E1318.MirrorCS", {"start": v(-150, 1760.92) * mm, "end": v(-80, 1720.5) * mm});
            skLineSegment(sketch, "E1319.MirrorCS", {"start": v(630, 1483.8) * mm, "end": v(560, 1443.38) * mm});
            skLineSegment(sketch, "E1320.MirrorCS", {"start": v(970, 1841.75) * mm, "end": v(1040, 1882.16) * mm});
            skLineSegment(sketch, "E1321.MirrorCS", {"start": v(250, 1345.23) * mm, "end": v(320, 1304.81) * mm});
            skLineSegment(sketch, "E1322.MirrorCS", {"start": v(720, 1443.38) * mm, "end": v(650, 1483.8) * mm});
            skLineSegment(sketch, "E1323.MirrorCS", {"start": v(470, 1287.5) * mm, "end": v(400, 1327.9) * mm});
            skLineSegment(sketch, "E1324.MirrorCS", {"start": v(810, 1564.62) * mm, "end": v(810, 1483.8) * mm});
            skLineSegment(sketch, "E1325.MirrorCS", {"start": v(-400, 1882.16) * mm, "end": v(-330, 1841.75) * mm});
            skLineSegment(sketch, "E1326.MirrorCS", {"start": v(-720, 1166.25) * mm, "end": v(-650, 1206.66) * mm});
            skLineSegment(sketch, "E1327.MirrorCS", {"start": v(80, 1443.38) * mm, "end": v(10, 1483.8) * mm});
            skLineSegment(sketch, "E1328.MirrorCS", {"start": v(-170, 1841.75) * mm, "end": v(-240, 1882.16) * mm});
            skLineSegment(sketch, "E1329.MirrorCS", {"start": v(310, 1841.75) * mm, "end": v(310, 1760.92) * mm});
            skLineSegment(sketch, "E1330.MirrorCS", {"start": v(-150, 1841.75) * mm, "end": v(-150, 1760.92) * mm});
            skLineSegment(sketch, "E1331.MirrorCS", {"start": v(650, 1483.8) * mm, "end": v(650, 1564.62) * mm});
            skLineSegment(sketch, "E1332.MirrorCS", {"start": v(720, 1882.16) * mm, "end": v(790, 1841.75) * mm});
            skLineSegment(sketch, "E1333.MirrorCS", {"start": v(-240, 1327.9) * mm, "end": v(-170, 1287.5) * mm});
            skLineSegment(sketch, "E1334.MirrorCS", {"start": v(-330, 1206.66) * mm, "end": v(-400, 1166.25) * mm});
            skLineSegment(sketch, "E1335.MirrorCS", {"start": v(330, 1206.66) * mm, "end": v(330, 1287.5) * mm});
            skLineSegment(sketch, "E1336.MirrorCS", {"start": v(-320, 1304.81) * mm, "end": v(-250, 1345.23) * mm});
            skLineSegment(sketch, "E1337.MirrorCS", {"start": v(-90, 1426.06) * mm, "end": v(-90, 1345.23) * mm});
            skLineSegment(sketch, "E1338.MirrorCS", {"start": v(-720, 1882.16) * mm, "end": v(-790, 1841.75) * mm});
            skLineSegment(sketch, "E1339.MirrorCS", {"start": v(-240, 1720.5) * mm, "end": v(-310, 1760.92) * mm});
            skLineSegment(sketch, "E1340.MirrorCS", {"start": v(-90, 1622.35) * mm, "end": v(-90, 1703.18) * mm});
            skLineSegment(sketch, "E1341.MirrorCS", {"start": v(1190, 1148.93) * mm, "end": v(1120, 1189.34) * mm});
            skLineSegment(sketch, "E1342.MirrorCS", {"start": v(-230, 1703.18) * mm, "end": v(-230, 1622.35) * mm});
            skLineSegment(sketch, "E1343.MirrorCS", {"start": v(-170, 1287.5) * mm, "end": v(-170, 1206.66) * mm});
            skLineSegment(sketch, "E1344.MirrorCS", {"start": v(-730, 1622.35) * mm, "end": v(-730, 1703.18) * mm});
            skLineSegment(sketch, "E1345.MirrorCS", {"start": v(890, 1703.18) * mm, "end": v(960, 1743.6) * mm});
            skLineSegment(sketch, "E1346.MirrorCS", {"start": v(490, 1483.8) * mm, "end": v(490, 1564.62) * mm});
            skLineSegment(sketch, "E1347.MirrorCS", {"start": v(560, 1605.03) * mm, "end": v(630, 1564.62) * mm});
            skLineSegment(sketch, "E1348.MirrorCS", {"start": v(720, 1166.25) * mm, "end": v(790, 1206.66) * mm});
            skLineSegment(sketch, "E1349.MirrorCS", {"start": v(-710, 1426.06) * mm, "end": v(-710, 1345.23) * mm});
            skLineSegment(sketch, "E1350.MirrorCS", {"start": v(330, 1564.62) * mm, "end": v(330, 1483.8) * mm});
            skLineSegment(sketch, "E1351.MirrorCS", {"start": v(790, 1564.62) * mm, "end": v(790, 1483.8) * mm});
            skLineSegment(sketch, "E1352.MirrorCS", {"start": v(640, 1304.81) * mm, "end": v(710, 1345.23) * mm});
            skLineSegment(sketch, "E1353.MirrorCS", {"start": v(-710, 1148.93) * mm, "end": v(-640, 1189.34) * mm});
            skLineSegment(sketch, "E1354", {"start": v(1210, -100.83) * mm, "end": v(-1944, -100.83) * mm});
            skLineSegment(sketch, "E1355", {"start": v(1210, 1902.16) * mm, "end": v(1210, -100.83) * mm});
            skPoint(sketch, "E1356.orphan", {"position": v(-800, 138.56) * mm});
            skLineSegment(sketch, "E1357.1", {"start": v(1190, 1703.18) * mm, "end": v(1190, 1622.35) * mm});
            skLineSegment(sketch, "E1357.3", {"start": v(-790, 98.15) * mm, "end": v(-790, 178.98) * mm});
            skLineSegment(sketch, "E1358", {"start": v(-1944, 1902.16) * mm, "end": v(1210, 1902.16) * mm});
            skLineSegment(sketch, "E1359.trimOffspring", {"start": v(-790, 1760.92) * mm, "end": v(-790, 1841.75) * mm});
            skLineSegment(sketch, "E1360.trimOffspring", {"start": v(-790, 1206.66) * mm, "end": v(-790, 1287.5) * mm});
            skLineSegment(sketch, "E1361.trimOffspring", {"start": v(-790, 652.4) * mm, "end": v(-790, 733.23) * mm});
            skLineSegment(sketch, "E1362.trimOffspring", {"start": v(1190, 40.41) * mm, "end": v(1190, -40.41) * mm});
            skLineSegment(sketch, "E1363.trimOffspring", {"start": v(1190, 213.62) * mm, "end": v(1190, 63.5) * mm});
            skLineSegment(sketch, "E1364.trimOffspring", {"start": v(1190, 490.75) * mm, "end": v(1190, 340.64) * mm});
            skLineSegment(sketch, "E1365.trimOffspring", {"start": v(1190, 767.88) * mm, "end": v(1190, 617.76) * mm});
            skLineSegment(sketch, "E1366.trimOffspring", {"start": v(1190, 871.8) * mm, "end": v(1190, 790.97) * mm});
            skLineSegment(sketch, "E1367.trimOffspring", {"start": v(1190, 1045) * mm, "end": v(1190, 894.9) * mm});
            skLineSegment(sketch, "E1368.trimOffspring", {"start": v(1190, 1322.13) * mm, "end": v(1190, 1172.02) * mm});
            skLineSegment(sketch, "E1369.trimOffspring", {"start": v(1190, 1599.26) * mm, "end": v(1190, 1449.15) * mm});
            skLineSegment(sketch, "E1370.MirrorCS", {"start": v(-810, 98.15) * mm, "end": v(-810, 178.98) * mm});
            skLineSegment(sketch, "E1371.MirrorCS", {"start": v(-1030, 40.41) * mm, "end": v(-1030, -40.41) * mm});
            skLineSegment(sketch, "E1372.MirrorCS", {"start": v(-810, 178.98) * mm, "end": v(-810, 98.15) * mm});
            skLineSegment(sketch, "E1373.MirrorCS", {"start": v(-1050, -40.41) * mm, "end": v(-1120, -80.83) * mm});
            skLineSegment(sketch, "E1374.MirrorCS", {"start": v(-1050, 40.41) * mm, "end": v(-1050, -40.41) * mm});
            skLineSegment(sketch, "E1375.MirrorCS", {"start": v(-1840, 334.86) * mm, "end": v(-1910, 375.28) * mm});
            skLineSegment(sketch, "E1376.MirrorCS", {"start": v(-890, -40.41) * mm, "end": v(-890, 40.41) * mm});
            skLineSegment(sketch, "E1377.MirrorCS", {"start": v(-1520, 1327.9) * mm, "end": v(-1450, 1287.5) * mm});
            skLineSegment(sketch, "E1378.MirrorCS", {"start": v(-1610, 178.98) * mm, "end": v(-1680, 219.4) * mm});
            skLineSegment(sketch, "E1379.MirrorCS", {"start": v(-880, 219.4) * mm, "end": v(-810, 178.98) * mm});
            skLineSegment(sketch, "E1380.MirrorCS", {"start": v(-1450, 375.28) * mm, "end": v(-1520, 334.86) * mm});
            skLineSegment(sketch, "E1381.MirrorCS", {"start": v(-880, 334.86) * mm, "end": v(-810, 375.28) * mm});
            skLineSegment(sketch, "E1382.MirrorCS", {"start": v(-810, 929.53) * mm, "end": v(-880, 889.12) * mm});
            skLineSegment(sketch, "E1383.MirrorCS", {"start": v(-1190, 1148.93) * mm, "end": v(-1120, 1189.34) * mm});
            skLineSegment(sketch, "E1384.MirrorCS", {"start": v(-880, 1327.9) * mm, "end": v(-810, 1287.5) * mm});
            skLineSegment(sketch, "E1385.MirrorCS", {"start": v(-1370, -40.41) * mm, "end": v(-1440, -80.83) * mm});
            skLineSegment(sketch, "E1386.MirrorCS", {"start": v(-1120, 1466.47) * mm, "end": v(-1050, 1426.06) * mm});
            skLineSegment(sketch, "E1387.MirrorCS", {"start": v(-1120, -80.83) * mm, "end": v(-1190, -40.41) * mm});
            skLineSegment(sketch, "E1388.MirrorCS", {"start": v(-1040, 1882.16) * mm, "end": v(-970, 1841.75) * mm});
            skLineSegment(sketch, "E1389.MirrorCS", {"start": v(-1520, 57.74) * mm, "end": v(-1590, 98.15) * mm});
            skLineSegment(sketch, "E1390.MirrorCS", {"start": v(-960, 1581.94) * mm, "end": v(-890, 1622.35) * mm});
            skLineSegment(sketch, "E1391.MirrorCS", {"start": v(-890, 1148.93) * mm, "end": v(-960, 1189.34) * mm});
            skLineSegment(sketch, "E1392.MirrorCS", {"start": v(-950, 178.98) * mm, "end": v(-880, 219.4) * mm});
            skLineSegment(sketch, "E1393.MirrorCS", {"start": v(-810, 1841.75) * mm, "end": v(-810, 1760.92) * mm});
            skLineSegment(sketch, "E1394.MirrorCS", {"start": v(-1130, 733.23) * mm, "end": v(-1200, 773.65) * mm});
            skLineSegment(sketch, "E1395.MirrorCS", {"start": v(-1280, 750.56) * mm, "end": v(-1350, 790.97) * mm});
            skLineSegment(sketch, "E1396.MirrorCS", {"start": v(-1510, 317.54) * mm, "end": v(-1440, 357.96) * mm});
            skLineSegment(sketch, "E1397.MirrorCS", {"start": v(-1030, -40.41) * mm, "end": v(-960, -80.83) * mm});
            skLineSegment(sketch, "E1398.MirrorCS", {"start": v(-1830, 317.54) * mm, "end": v(-1760, 357.96) * mm});
            skLineSegment(sketch, "E1399.MirrorCS", {"start": v(-810, 375.28) * mm, "end": v(-810, 456.1) * mm});
            skLineSegment(sketch, "E1400.MirrorCS", {"start": v(-880, 773.65) * mm, "end": v(-810, 733.23) * mm});
            skLineSegment(sketch, "E1401.MirrorCS", {"start": v(-1690, 317.54) * mm, "end": v(-1760, 357.96) * mm});
            skLineSegment(sketch, "E1402.MirrorCS", {"start": v(-1510, -40.41) * mm, "end": v(-1510, 40.41) * mm});
            skLineSegment(sketch, "E1403.MirrorCS", {"start": v(-1040, 889.12) * mm, "end": v(-970, 929.53) * mm});
            skLineSegment(sketch, "E1404.MirrorCS", {"start": v(-890, 790.97) * mm, "end": v(-960, 750.56) * mm});
            skLineSegment(sketch, "E1405.MirrorCS", {"start": v(-1040, 334.86) * mm, "end": v(-1110, 375.28) * mm});
            skLineSegment(sketch, "E1406.MirrorCS", {"start": v(-1370, 1426.06) * mm, "end": v(-1440, 1466.47) * mm});
            skLineSegment(sketch, "E1407.MirrorCS", {"start": v(-1610, 929.53) * mm, "end": v(-1680, 889.12) * mm});
            skLineSegment(sketch, "E1408.MirrorCS", {"start": v(-1910, 178.98) * mm, "end": v(-1840, 219.4) * mm});
            skLineSegment(sketch, "E1409.MirrorCS", {"start": v(-1530, 317.54) * mm, "end": v(-1600, 357.96) * mm});
            skLineSegment(sketch, "E1410.MirrorCS", {"start": v(-1110, 1483.8) * mm, "end": v(-1040, 1443.38) * mm});
            skLineSegment(sketch, "E1411.MirrorCS", {"start": v(-1840, 1443.38) * mm, "end": v(-1910, 1483.8) * mm});
            skLineSegment(sketch, "E1412.MirrorCS", {"start": v(-1600, 1581.94) * mm, "end": v(-1670, 1622.35) * mm});
            skLineSegment(sketch, "E1413.MirrorCS", {"start": v(-1040, 1327.9) * mm, "end": v(-1110, 1287.5) * mm});
            skLineSegment(sketch, "E1414.MirrorCS", {"start": v(-810, 1287.5) * mm, "end": v(-810, 1206.66) * mm});
            skLineSegment(sketch, "E1415.MirrorCS", {"start": v(-810, 1483.8) * mm, "end": v(-880, 1443.38) * mm});
            skLineSegment(sketch, "E1416.MirrorCS", {"start": v(-1210, 1148.93) * mm, "end": v(-1280, 1189.34) * mm});
            skLineSegment(sketch, "E1417.MirrorCS", {"start": v(-970, 375.28) * mm, "end": v(-1040, 334.86) * mm});
            skLineSegment(sketch, "E1418.MirrorCS", {"start": v(-1290, 929.53) * mm, "end": v(-1360, 889.12) * mm});
            skLineSegment(sketch, "E1419.MirrorCS", {"start": v(-1030, 317.54) * mm, "end": v(-960, 357.96) * mm});
            skLineSegment(sketch, "E1420.MirrorCS", {"start": v(-1520, 1443.38) * mm, "end": v(-1450, 1483.8) * mm});
            skLineSegment(sketch, "E1421.MirrorCS", {"start": v(-1120, 750.56) * mm, "end": v(-1050, 790.97) * mm});
            skLineSegment(sketch, "E1422.MirrorCS", {"start": v(-1530, 1148.93) * mm, "end": v(-1600, 1189.34) * mm});
            skLineSegment(sketch, "E1423.MirrorCS", {"start": v(-950, 1287.5) * mm, "end": v(-880, 1327.9) * mm});
            skLineSegment(sketch, "E1424.MirrorCS", {"start": v(-1050, 1148.93) * mm, "end": v(-1120, 1189.34) * mm});
            skLineSegment(sketch, "E1425.MirrorCS", {"start": v(-880, 1882.16) * mm, "end": v(-810, 1841.75) * mm});
            skLineSegment(sketch, "E1426.MirrorCS", {"start": v(-1680, 1882.16) * mm, "end": v(-1610, 1841.75) * mm});
            skLineSegment(sketch, "E1427.MirrorCS", {"start": v(-810, 929.53) * mm, "end": v(-810, 1010.36) * mm});
            skLineSegment(sketch, "E1428.MirrorCS", {"start": v(-1590, 1841.75) * mm, "end": v(-1520, 1882.16) * mm});
            skLineSegment(sketch, "E1429.MirrorCS", {"start": v(-1530, 40.41) * mm, "end": v(-1600, 80.83) * mm});
            skLineSegment(sketch, "E1430.MirrorCS", {"start": v(-1430, 733.23) * mm, "end": v(-1360, 773.65) * mm});
            skLineSegment(sketch, "E1431.MirrorCS", {"start": v(-1190, -40.41) * mm, "end": v(-1190, 40.41) * mm});
            skLineSegment(sketch, "E1432.MirrorCS", {"start": v(-1840, 334.86) * mm, "end": v(-1770, 375.28) * mm});
            skLineSegment(sketch, "E1433.MirrorCS", {"start": v(-1360, 334.86) * mm, "end": v(-1290, 375.28) * mm});
            skLineSegment(sketch, "E1434.MirrorCS", {"start": v(-1690, 1622.35) * mm, "end": v(-1760, 1581.94) * mm});
            skLineSegment(sketch, "E1435.MirrorCS", {"start": v(-1680, 1443.38) * mm, "end": v(-1610, 1483.8) * mm});
            skLineSegment(sketch, "E1436.MirrorCS", {"start": v(-1050, 1622.35) * mm, "end": v(-1120, 1581.94) * mm});
            skLineSegment(sketch, "E1437.MirrorCS", {"start": v(-1200, 219.4) * mm, "end": v(-1130, 178.98) * mm});
            skLineSegment(sketch, "E1438.MirrorCS", {"start": v(-1750, 375.28) * mm, "end": v(-1680, 334.86) * mm});
            skLineSegment(sketch, "E1439.MirrorCS", {"start": v(-1450, 178.98) * mm, "end": v(-1520, 219.4) * mm});
            skLineSegment(sketch, "E1440.MirrorCS", {"start": v(-1430, 929.53) * mm, "end": v(-1360, 889.12) * mm});
            skLineSegment(sketch, "E1441.MirrorCS", {"start": v(-1290, 1287.5) * mm, "end": v(-1360, 1327.9) * mm});
            skLineSegment(sketch, "E1442.MirrorCS", {"start": v(-1280, 1466.47) * mm, "end": v(-1210, 1426.06) * mm});
            skLineSegment(sketch, "E1443.MirrorCS", {"start": v(-1680, 219.4) * mm, "end": v(-1750, 178.98) * mm});
            skLineSegment(sketch, "E1444.MirrorCS", {"start": v(-1120, 750.56) * mm, "end": v(-1190, 790.97) * mm});
            skLineSegment(sketch, "E1445.MirrorCS", {"start": v(-1760, 1189.34) * mm, "end": v(-1830, 1148.93) * mm});
            skLineSegment(sketch, "E1446.MirrorCS", {"start": v(-1760, 1466.47) * mm, "end": v(-1830, 1426.06) * mm});
            skLineSegment(sketch, "E1447.MirrorCS", {"start": v(-1760, 1189.34) * mm, "end": v(-1690, 1148.93) * mm});
            skLineSegment(sketch, "E1448.MirrorCS", {"start": v(-1120, 635.09) * mm, "end": v(-1050, 594.67) * mm});
            skLineSegment(sketch, "E1449.MirrorCS", {"start": v(-1670, -40.41) * mm, "end": v(-1600, -80.83) * mm});
            skLineSegment(sketch, "E1450.MirrorCS", {"start": v(-1440, 1189.34) * mm, "end": v(-1370, 1148.93) * mm});
            skLineSegment(sketch, "E1451.MirrorCS", {"start": v(-810, 733.23) * mm, "end": v(-810, 652.4) * mm});
            skLineSegment(sketch, "E1452.MirrorCS", {"start": v(-1200, 334.86) * mm, "end": v(-1270, 375.28) * mm});
            skLineSegment(sketch, "E1453.MirrorCS", {"start": v(-1760, 80.83) * mm, "end": v(-1690, 40.41) * mm});
            skLineSegment(sketch, "E1454.MirrorCS", {"start": v(-1210, 594.67) * mm, "end": v(-1280, 635.09) * mm});
            skLineSegment(sketch, "E1455.MirrorCS", {"start": v(-1270, 1287.5) * mm, "end": v(-1200, 1327.9) * mm});
            skLineSegment(sketch, "E1456.MirrorCS", {"start": v(-1840, 1327.9) * mm, "end": v(-1770, 1287.5) * mm});
            skLineSegment(sketch, "E1457.MirrorCS", {"start": v(-1110, 1841.75) * mm, "end": v(-1040, 1882.16) * mm});
            skLineSegment(sketch, "E1458.MirrorCS", {"start": v(-960, 1466.47) * mm, "end": v(-1030, 1426.06) * mm});
            skLineSegment(sketch, "E1459.MirrorCS", {"start": v(-1610, 98.15) * mm, "end": v(-1680, 57.74) * mm});
            skLineSegment(sketch, "E1460.MirrorCS", {"start": v(-1600, 1466.47) * mm, "end": v(-1530, 1426.06) * mm});
            skLineSegment(sketch, "E1461.MirrorCS", {"start": v(-1520, 773.65) * mm, "end": v(-1590, 733.23) * mm});
            skLineSegment(sketch, "E1462.MirrorCS", {"start": v(-1760, 750.56) * mm, "end": v(-1690, 790.97) * mm});
            skLineSegment(sketch, "E1463.MirrorCS", {"start": v(-1270, 733.23) * mm, "end": v(-1200, 773.65) * mm});
            skLineSegment(sketch, "E1464.MirrorCS", {"start": v(-1120, 635.09) * mm, "end": v(-1190, 594.67) * mm});
            skLineSegment(sketch, "E1465.MirrorCS", {"start": v(-1040, 889.12) * mm, "end": v(-1110, 929.53) * mm});
            skLineSegment(sketch, "E1466.MirrorCS", {"start": v(-960, 1581.94) * mm, "end": v(-1030, 1622.35) * mm});
            skLineSegment(sketch, "E1467.MirrorCS", {"start": v(-950, 375.28) * mm, "end": v(-880, 334.86) * mm});
            skLineSegment(sketch, "E1468.MirrorCS", {"start": v(-1830, 1622.35) * mm, "end": v(-1760, 1581.94) * mm});
            skLineSegment(sketch, "E1469.MirrorCS", {"start": v(-1370, 317.54) * mm, "end": v(-1440, 357.96) * mm});
            skLineSegment(sketch, "E1470.MirrorCS", {"start": v(-1210, 1622.35) * mm, "end": v(-1280, 1581.94) * mm});
            skLineSegment(sketch, "E1471.MirrorCS", {"start": v(-880, 1882.16) * mm, "end": v(-950, 1841.75) * mm});
            skLineSegment(sketch, "E1472.MirrorCS", {"start": v(-890, 1426.06) * mm, "end": v(-960, 1466.47) * mm});
            skLineSegment(sketch, "E1473.MirrorCS", {"start": v(-1280, 357.96) * mm, "end": v(-1210, 317.54) * mm});
            skLineSegment(sketch, "E1474.MirrorCS", {"start": v(-880, 1443.38) * mm, "end": v(-950, 1483.8) * mm});
            skLineSegment(sketch, "E1475.MirrorCS", {"start": v(-1370, 1622.35) * mm, "end": v(-1440, 1581.94) * mm});
            skLineSegment(sketch, "E1476.MirrorCS", {"start": v(-1520, 1443.38) * mm, "end": v(-1590, 1483.8) * mm});
            skLineSegment(sketch, "E1477.MirrorCS", {"start": v(-1690, 1426.06) * mm, "end": v(-1760, 1466.47) * mm});
            skLineSegment(sketch, "E1478.MirrorCS", {"start": v(-1360, 219.4) * mm, "end": v(-1290, 178.98) * mm});
            skLineSegment(sketch, "E1479.MirrorCS", {"start": v(-1680, 334.86) * mm, "end": v(-1610, 375.28) * mm});
            skLineSegment(sketch, "E1480.MirrorCS", {"start": v(-950, 733.23) * mm, "end": v(-880, 773.65) * mm});
            skLineSegment(sketch, "E1481.MirrorCS", {"start": v(-970, 1483.8) * mm, "end": v(-1040, 1443.38) * mm});
            skLineSegment(sketch, "E1482.MirrorCS", {"start": v(-1680, 1443.38) * mm, "end": v(-1750, 1483.8) * mm});
            skLineSegment(sketch, "E1483.MirrorCS", {"start": v(-1910, 733.23) * mm, "end": v(-1840, 773.65) * mm});
            skLineSegment(sketch, "E1484.MirrorCS", {"start": v(-1350, 594.67) * mm, "end": v(-1280, 635.09) * mm});
            skLineSegment(sketch, "E1485.MirrorCS", {"start": v(-1600, 80.83) * mm, "end": v(-1670, 40.41) * mm});
            skLineSegment(sketch, "E1486.MirrorCS", {"start": v(-1270, 929.53) * mm, "end": v(-1200, 889.12) * mm});
            skLineSegment(sketch, "E1487.MirrorCS", {"start": v(-1430, 1287.5) * mm, "end": v(-1360, 1327.9) * mm});
            skLineSegment(sketch, "E1488.MirrorCS", {"start": v(-1520, 889.12) * mm, "end": v(-1590, 929.53) * mm});
            skLineSegment(sketch, "E1489.MirrorCS", {"start": v(-1510, 790.97) * mm, "end": v(-1440, 750.56) * mm});
            skLineSegment(sketch, "E1490.MirrorCS", {"start": v(-1910, 1287.5) * mm, "end": v(-1840, 1327.9) * mm});
            skLineSegment(sketch, "E1491.MirrorCS", {"start": v(-1130, 375.28) * mm, "end": v(-1200, 334.86) * mm});
            skLineSegment(sketch, "E1492.MirrorCS", {"start": v(-1690, 594.67) * mm, "end": v(-1760, 635.09) * mm});
            skLineSegment(sketch, "E1493.MirrorCS", {"start": v(-970, 178.98) * mm, "end": v(-1040, 219.4) * mm});
            skLineSegment(sketch, "E1494.MirrorCS", {"start": v(-1600, 1189.34) * mm, "end": v(-1670, 1148.93) * mm});
            skLineSegment(sketch, "E1495.MirrorCS", {"start": v(-1510, 1622.35) * mm, "end": v(-1440, 1581.94) * mm});
            skLineSegment(sketch, "E1496.MirrorCS", {"start": v(-1680, 1327.9) * mm, "end": v(-1610, 1287.5) * mm});
            skLineSegment(sketch, "E1497.MirrorCS", {"start": v(-1590, 375.28) * mm, "end": v(-1520, 334.86) * mm});
            skLineSegment(sketch, "E1498.MirrorCS", {"start": v(-950, 929.53) * mm, "end": v(-880, 889.12) * mm});
            skLineSegment(sketch, "E1499.MirrorCS", {"start": v(-1200, 1327.9) * mm, "end": v(-1130, 1287.5) * mm});
            skLineSegment(sketch, "E1500.MirrorCS", {"start": v(-1200, 1443.38) * mm, "end": v(-1270, 1483.8) * mm});
            skLineSegment(sketch, "E1501.MirrorCS", {"start": v(-1530, 594.67) * mm, "end": v(-1600, 635.09) * mm});
            skLineSegment(sketch, "E1502.MirrorCS", {"start": v(-1280, 1466.47) * mm, "end": v(-1350, 1426.06) * mm});
            skLineSegment(sketch, "E1503.MirrorCS", {"start": v(-1040, 1327.9) * mm, "end": v(-970, 1287.5) * mm});
            skLineSegment(sketch, "E1504.MirrorCS", {"start": v(-1200, 889.12) * mm, "end": v(-1130, 929.53) * mm});
            skLineSegment(sketch, "E1505.MirrorCS", {"start": v(-1840, 219.4) * mm, "end": v(-1770, 178.98) * mm});
            skLineSegment(sketch, "E1506.MirrorCS", {"start": v(-1190, 1622.35) * mm, "end": v(-1120, 1581.94) * mm});
            skLineSegment(sketch, "E1507.MirrorCS", {"start": v(-1190, 317.54) * mm, "end": v(-1120, 357.96) * mm});
            skLineSegment(sketch, "E1508.MirrorCS", {"start": v(-1210, 790.97) * mm, "end": v(-1280, 750.56) * mm});
            skLineSegment(sketch, "E1509.MirrorCS", {"start": v(-1520, 773.65) * mm, "end": v(-1450, 733.23) * mm});
            skLineSegment(sketch, "E1510.MirrorCS", {"start": v(-1760, 635.09) * mm, "end": v(-1830, 594.67) * mm});
            skLineSegment(sketch, "E1511.MirrorCS", {"start": v(-1130, 1483.8) * mm, "end": v(-1200, 1443.38) * mm});
            skLineSegment(sketch, "E1512.MirrorCS", {"start": v(-1350, 317.54) * mm, "end": v(-1280, 357.96) * mm});
            skLineSegment(sketch, "E1513.MirrorCS", {"start": v(-1590, 178.98) * mm, "end": v(-1520, 219.4) * mm});
            skLineSegment(sketch, "E1514.MirrorCS", {"start": v(-1200, 219.4) * mm, "end": v(-1270, 178.98) * mm});
            skLineSegment(sketch, "E1515.MirrorCS", {"start": v(-1510, 1426.06) * mm, "end": v(-1440, 1466.47) * mm});
            skLineSegment(sketch, "E1516.MirrorCS", {"start": v(-1750, 733.23) * mm, "end": v(-1680, 773.65) * mm});
            skLineSegment(sketch, "E1517.MirrorCS", {"start": v(-1510, 594.67) * mm, "end": v(-1440, 635.09) * mm});
            skLineSegment(sketch, "E1518.MirrorCS", {"start": v(-1680, 1327.9) * mm, "end": v(-1750, 1287.5) * mm});
            skLineSegment(sketch, "E1519.MirrorCS", {"start": v(-1840, 1882.16) * mm, "end": v(-1910, 1841.75) * mm});
            skLineSegment(sketch, "E1520.MirrorCS", {"start": v(-1360, 773.65) * mm, "end": v(-1290, 733.23) * mm});
            skLineSegment(sketch, "E1521.MirrorCS", {"start": v(-1680, 773.65) * mm, "end": v(-1610, 733.23) * mm});
            skLineSegment(sketch, "E1522.MirrorCS", {"start": v(-1120, 357.96) * mm, "end": v(-1050, 317.54) * mm});
            skLineSegment(sketch, "E1523.MirrorCS", {"start": v(-1670, 1426.06) * mm, "end": v(-1600, 1466.47) * mm});
            skLineSegment(sketch, "E1524.MirrorCS", {"start": v(-1430, 1483.8) * mm, "end": v(-1360, 1443.38) * mm});
            skLineSegment(sketch, "E1525.MirrorCS", {"start": v(-1670, 594.67) * mm, "end": v(-1600, 635.09) * mm});
            skLineSegment(sketch, "E1526.MirrorCS", {"start": v(-1440, 635.09) * mm, "end": v(-1370, 594.67) * mm});
            skLineSegment(sketch, "E1527.MirrorCS", {"start": v(-960, 635.09) * mm, "end": v(-1030, 594.67) * mm});
            skLineSegment(sketch, "E1528.MirrorCS", {"start": v(-1130, 1841.75) * mm, "end": v(-1200, 1882.16) * mm});
            skLineSegment(sketch, "E1529.MirrorCS", {"start": v(-1510, 1148.93) * mm, "end": v(-1440, 1189.34) * mm});
            skLineSegment(sketch, "E1530.MirrorCS", {"start": v(-1600, -80.83) * mm, "end": v(-1530, -40.41) * mm});
            skLineSegment(sketch, "E1531.MirrorCS", {"start": v(-1530, -40.41) * mm, "end": v(-1530, 40.41) * mm});
            skLineSegment(sketch, "E1532.MirrorCS", {"start": v(-1440, 750.56) * mm, "end": v(-1370, 790.97) * mm});
            skLineSegment(sketch, "E1533.MirrorCS", {"start": v(-1450, 929.53) * mm, "end": v(-1520, 889.12) * mm});
            skLineSegment(sketch, "E1534.MirrorCS", {"start": v(-1680, 889.12) * mm, "end": v(-1750, 929.53) * mm});
            skLineSegment(sketch, "E1535.MirrorCS", {"start": v(-1430, 1841.75) * mm, "end": v(-1360, 1882.16) * mm});
            skLineSegment(sketch, "E1536.MirrorCS", {"start": v(-1600, 1581.94) * mm, "end": v(-1530, 1622.35) * mm});
            skLineSegment(sketch, "E1537.MirrorCS", {"start": v(-1350, 1622.35) * mm, "end": v(-1280, 1581.94) * mm});
            skLineSegment(sketch, "E1538.MirrorCS", {"start": v(-960, 357.96) * mm, "end": v(-890, 317.54) * mm});
            skLineSegment(sketch, "E1539.MirrorCS", {"start": v(-1280, 1189.34) * mm, "end": v(-1350, 1148.93) * mm});
            skLineSegment(sketch, "E1540.MirrorCS", {"start": v(-1600, 357.96) * mm, "end": v(-1670, 317.54) * mm});
            skLineSegment(sketch, "E1541.MirrorCS", {"start": v(-1270, 1841.75) * mm, "end": v(-1200, 1882.16) * mm});
            skLineSegment(sketch, "E1542.MirrorCS", {"start": v(-960, 635.09) * mm, "end": v(-890, 594.67) * mm});
            skLineSegment(sketch, "E1543.MirrorCS", {"start": v(-1600, 750.56) * mm, "end": v(-1670, 790.97) * mm});
            skLineSegment(sketch, "E1544.MirrorCS", {"start": v(-1520, 1882.16) * mm, "end": v(-1450, 1841.75) * mm});
            skLineSegment(sketch, "E1545.MirrorCS", {"start": v(-1600, 750.56) * mm, "end": v(-1530, 790.97) * mm});
            skLineSegment(sketch, "E1546.MirrorCS", {"start": v(-1040, 773.65) * mm, "end": v(-1110, 733.23) * mm});
            skLineSegment(sketch, "E1547.MirrorCS", {"start": v(-1590, 1287.5) * mm, "end": v(-1520, 1327.9) * mm});
            skLineSegment(sketch, "E1548.MirrorCS", {"start": v(-1120, 1466.47) * mm, "end": v(-1190, 1426.06) * mm});
            skLineSegment(sketch, "E1549.MirrorCS", {"start": v(-1110, 178.98) * mm, "end": v(-1040, 219.4) * mm});
            skLineSegment(sketch, "E1550.MirrorCS", {"start": v(-960, 1189.34) * mm, "end": v(-1030, 1148.93) * mm});
            skLineSegment(sketch, "E1551.MirrorCS", {"start": v(-1430, 375.28) * mm, "end": v(-1360, 334.86) * mm});
            skLineSegment(sketch, "E1552.MirrorCS", {"start": v(-1440, -80.83) * mm, "end": v(-1510, -40.41) * mm});
            skLineSegment(sketch, "E1553.MirrorCS", {"start": v(-810, 1483.8) * mm, "end": v(-810, 1564.62) * mm});
            skLineSegment(sketch, "E1554.MirrorCS", {"start": v(-1770, 1483.8) * mm, "end": v(-1840, 1443.38) * mm});
            skLineSegment(sketch, "E1555.MirrorCS", {"start": v(-1290, 1841.75) * mm, "end": v(-1360, 1882.16) * mm});
            skLineSegment(sketch, "E1556.MirrorCS", {"start": v(-1360, 1443.38) * mm, "end": v(-1290, 1483.8) * mm});
            skLineSegment(sketch, "E1557.MirrorCS", {"start": v(-1680, 1882.16) * mm, "end": v(-1750, 1841.75) * mm});
            skLineSegment(sketch, "E1558.MirrorCS", {"start": v(-1360, 219.4) * mm, "end": v(-1430, 178.98) * mm});
            skLineSegment(sketch, "E1559.MirrorCS", {"start": v(-1840, 889.12) * mm, "end": v(-1770, 929.53) * mm});
            skLineSegment(sketch, "E1560.MirrorCS", {"start": v(-1840, 1882.16) * mm, "end": v(-1770, 1841.75) * mm});
            skLineSegment(sketch, "E1561.MirrorCS", {"start": v(-1030, 790.97) * mm, "end": v(-960, 750.56) * mm});
            skLineSegment(sketch, "E1562.MirrorCS", {"start": v(-970, 733.23) * mm, "end": v(-1040, 773.65) * mm});
            skLineSegment(sketch, "E1563.MirrorCS", {"start": v(-1840, 889.12) * mm, "end": v(-1910, 929.53) * mm});
            skLineSegment(sketch, "E1564.MirrorCS", {"start": v(-1770, 733.23) * mm, "end": v(-1840, 773.65) * mm});
            skLineSegment(sketch, "E1565.MirrorCS", {"start": v(-1760, 750.56) * mm, "end": v(-1830, 790.97) * mm});
            skLineSegment(sketch, "E1566.MirrorCS", {"start": v(-1030, 1148.93) * mm, "end": v(-960, 1189.34) * mm});
            skLineSegment(sketch, "E1567.MirrorCS", {"start": v(-1370, 513.84) * mm, "end": v(-1370, 594.67) * mm});
            skLineSegment(sketch, "E1568.MirrorCS", {"start": v(-1280, 1581.94) * mm, "end": v(-1350, 1622.35) * mm});
            skLineSegment(sketch, "E1569.MirrorCS", {"start": v(-1910, 929.53) * mm, "end": v(-1840, 889.12) * mm});
            skLineSegment(sketch, "E1570.MirrorCS", {"start": v(-1110, 652.4) * mm, "end": v(-1110, 733.23) * mm});
            skLineSegment(sketch, "E1571.MirrorCS", {"start": v(-1190, 1426.06) * mm, "end": v(-1120, 1466.47) * mm});
            skLineSegment(sketch, "E1572.MirrorCS", {"start": v(-1450, 1564.62) * mm, "end": v(-1520, 1605.03) * mm});
            skLineSegment(sketch, "E1573.MirrorCS", {"start": v(-810, 1010.36) * mm, "end": v(-880, 1050.78) * mm});
            skLineSegment(sketch, "E1574.MirrorCS", {"start": v(-1280, 1304.81) * mm, "end": v(-1350, 1345.23) * mm});
            skLineSegment(sketch, "E1575.MirrorCS", {"start": v(-1370, 790.97) * mm, "end": v(-1440, 750.56) * mm});
            skLineSegment(sketch, "E1576.MirrorCS", {"start": v(-1610, 178.98) * mm, "end": v(-1610, 98.15) * mm});
            skLineSegment(sketch, "E1577.MirrorCS", {"start": v(-1760, 1581.94) * mm, "end": v(-1830, 1622.35) * mm});
            skLineSegment(sketch, "E1578.MirrorCS", {"start": v(-1040, 1605.03) * mm, "end": v(-1110, 1564.62) * mm});
            skLineSegment(sketch, "E1579.MirrorCS", {"start": v(-1270, 1483.8) * mm, "end": v(-1200, 1443.38) * mm});
            skLineSegment(sketch, "E1580.MirrorCS", {"start": v(-1680, 496.52) * mm, "end": v(-1750, 456.1) * mm});
            skLineSegment(sketch, "E1581.MirrorCS", {"start": v(-1280, -80.83) * mm, "end": v(-1210, -40.41) * mm});
            skLineSegment(sketch, "E1582.MirrorCS", {"start": v(-1840, 1605.03) * mm, "end": v(-1770, 1564.62) * mm});
            skLineSegment(sketch, "E1583.MirrorCS", {"start": v(-1280, 1743.6) * mm, "end": v(-1350, 1703.18) * mm});
            skLineSegment(sketch, "E1584.MirrorCS", {"start": v(-1120, 1189.34) * mm, "end": v(-1190, 1148.93) * mm});
            skLineSegment(sketch, "E1585.MirrorCS", {"start": v(-1440, 635.09) * mm, "end": v(-1510, 594.67) * mm});
            skLineSegment(sketch, "E1586.MirrorCS", {"start": v(-1200, 1327.9) * mm, "end": v(-1270, 1287.5) * mm});
            skLineSegment(sketch, "E1587.MirrorCS", {"start": v(-1370, 1148.93) * mm, "end": v(-1440, 1189.34) * mm});
            skLineSegment(sketch, "E1588.MirrorCS", {"start": v(-1610, 1760.92) * mm, "end": v(-1680, 1720.5) * mm});
            skLineSegment(sketch, "E1589.MirrorCS", {"start": v(-1280, 1027.68) * mm, "end": v(-1350, 1068.1) * mm});
            skLineSegment(sketch, "E1590.MirrorCS", {"start": v(-1530, 1148.93) * mm, "end": v(-1530, 1068.1) * mm});
            skLineSegment(sketch, "E1591.MirrorCS", {"start": v(-1290, 1206.66) * mm, "end": v(-1290, 1287.5) * mm});
            skLineSegment(sketch, "E1592.MirrorCS", {"start": v(-960, 473.43) * mm, "end": v(-1030, 513.84) * mm});
            skLineSegment(sketch, "E1593.MirrorCS", {"start": v(-1750, 456.1) * mm, "end": v(-1750, 375.28) * mm});
            skLineSegment(sketch, "E1594.MirrorCS", {"start": v(-880, 773.65) * mm, "end": v(-950, 733.23) * mm});
            skLineSegment(sketch, "E1595.MirrorCS", {"start": v(-950, 456.1) * mm, "end": v(-950, 375.28) * mm});
            skLineSegment(sketch, "E1596.MirrorCS", {"start": v(-1270, 1564.62) * mm, "end": v(-1200, 1605.03) * mm});
            skLineSegment(sketch, "E1597.MirrorCS", {"start": v(-1600, 635.09) * mm, "end": v(-1670, 594.67) * mm});
            skLineSegment(sketch, "E1598.MirrorCS", {"start": v(-1840, 1166.25) * mm, "end": v(-1770, 1206.66) * mm});
            skLineSegment(sketch, "E1599.MirrorCS", {"start": v(-1430, 1206.66) * mm, "end": v(-1360, 1166.25) * mm});
            skLineSegment(sketch, "E1600.MirrorCS", {"start": v(-1450, 929.53) * mm, "end": v(-1450, 1010.36) * mm});
            skLineSegment(sketch, "E1601.MirrorCS", {"start": v(-1830, 1068.1) * mm, "end": v(-1760, 1027.68) * mm});
            skLineSegment(sketch, "E1602.MirrorCS", {"start": v(-1760, 196.3) * mm, "end": v(-1690, 236.71) * mm});
            skLineSegment(sketch, "E1603.MirrorCS", {"start": v(-1610, 1287.5) * mm, "end": v(-1680, 1327.9) * mm});
            skLineSegment(sketch, "E1604.MirrorCS", {"start": v(-870, 317.54) * mm, "end": v(-800, 357.96) * mm});
            skLineSegment(sketch, "E1605.MirrorCS", {"start": v(-1370, 236.71) * mm, "end": v(-1370, 317.54) * mm});
            skLineSegment(sketch, "E1606.MirrorCS", {"start": v(-1120, 1581.94) * mm, "end": v(-1050, 1622.35) * mm});
            skLineSegment(sketch, "E1607.MirrorCS", {"start": v(-1520, 1050.78) * mm, "end": v(-1590, 1010.36) * mm});
            skLineSegment(sketch, "E1608.MirrorCS", {"start": v(-1210, 317.54) * mm, "end": v(-1210, 236.71) * mm});
            skLineSegment(sketch, "E1609.MirrorCS", {"start": v(-1690, 1345.23) * mm, "end": v(-1690, 1426.06) * mm});
            skLineSegment(sketch, "E1610.MirrorCS", {"start": v(-1280, 473.43) * mm, "end": v(-1350, 513.84) * mm});
            skLineSegment(sketch, "E1611.MirrorCS", {"start": v(-1190, 236.71) * mm, "end": v(-1120, 196.3) * mm});
            skLineSegment(sketch, "E1612.MirrorCS", {"start": v(-1190, 871.8) * mm, "end": v(-1120, 912.21) * mm});
            skLineSegment(sketch, "E1613.MirrorCS", {"start": v(-1350, 513.84) * mm, "end": v(-1350, 594.67) * mm});
            skLineSegment(sketch, "E1614.MirrorCS", {"start": v(-1760, 635.09) * mm, "end": v(-1690, 594.67) * mm});
            skLineSegment(sketch, "E1615.MirrorCS", {"start": v(-1130, 1760.92) * mm, "end": v(-1130, 1841.75) * mm});
            skLineSegment(sketch, "E1616.MirrorCS", {"start": v(-1280, 196.3) * mm, "end": v(-1350, 236.71) * mm});
            skLineSegment(sketch, "E1617.MirrorCS", {"start": v(-1430, 1841.75) * mm, "end": v(-1430, 1760.92) * mm});
            skLineSegment(sketch, "E1618.MirrorCS", {"start": v(-1830, 1148.93) * mm, "end": v(-1830, 1068.1) * mm});
            skLineSegment(sketch, "E1619.MirrorCS", {"start": v(-1440, 1743.6) * mm, "end": v(-1370, 1703.18) * mm});
            skLineSegment(sketch, "E1620.MirrorCS", {"start": v(-1770, 178.98) * mm, "end": v(-1840, 219.4) * mm});
            skLineSegment(sketch, "E1621.MirrorCS", {"start": v(-1830, 1345.23) * mm, "end": v(-1760, 1304.81) * mm});
            skLineSegment(sketch, "E1622.MirrorCS", {"start": v(-1360, 1882.16) * mm, "end": v(-1290, 1841.75) * mm});
            skLineSegment(sketch, "E1623.MirrorCS", {"start": v(-1530, 317.54) * mm, "end": v(-1530, 236.71) * mm});
            skLineSegment(sketch, "E1624.MirrorCS", {"start": v(-1430, 178.98) * mm, "end": v(-1360, 219.4) * mm});
            skLineSegment(sketch, "E1625.MirrorCS", {"start": v(-1520, 1605.03) * mm, "end": v(-1590, 1564.62) * mm});
            skLineSegment(sketch, "E1626.MirrorCS", {"start": v(-1770, 1206.66) * mm, "end": v(-1770, 1287.5) * mm});
            skLineSegment(sketch, "E1627.MirrorCS", {"start": v(-1510, 1703.18) * mm, "end": v(-1440, 1743.6) * mm});
            skLineSegment(sketch, "E1628.MirrorCS", {"start": v(-1450, 1287.5) * mm, "end": v(-1520, 1327.9) * mm});
            skLineSegment(sketch, "E1629.MirrorCS", {"start": v(-890, 1703.18) * mm, "end": v(-960, 1743.6) * mm});
            skLineSegment(sketch, "E1630.MirrorCS", {"start": v(-1520, 1166.25) * mm, "end": v(-1590, 1206.66) * mm});
            skLineSegment(sketch, "E1631.MirrorCS", {"start": v(-1200, 889.12) * mm, "end": v(-1270, 929.53) * mm});
            skLineSegment(sketch, "E1632.MirrorCS", {"start": v(-1190, 594.67) * mm, "end": v(-1190, 513.84) * mm});
            skLineSegment(sketch, "E1633.MirrorCS", {"start": v(-1520, 1720.5) * mm, "end": v(-1590, 1760.92) * mm});
            skLineSegment(sketch, "E1634.MirrorCS", {"start": v(-1360, 1166.25) * mm, "end": v(-1290, 1206.66) * mm});
            skLineSegment(sketch, "E1635.MirrorCS", {"start": v(-1600, 1304.81) * mm, "end": v(-1670, 1345.23) * mm});
            skLineSegment(sketch, "E1636.MirrorCS", {"start": v(-1130, 456.1) * mm, "end": v(-1130, 375.28) * mm});
            skLineSegment(sketch, "E1637.MirrorCS", {"start": v(-880, 1443.38) * mm, "end": v(-810, 1483.8) * mm});
            skLineSegment(sketch, "E1638.MirrorCS", {"start": v(-1530, 513.84) * mm, "end": v(-1600, 473.43) * mm});
            skLineSegment(sketch, "E1639.MirrorCS", {"start": v(-970, 375.28) * mm, "end": v(-970, 456.1) * mm});
            skLineSegment(sketch, "E1640.MirrorCS", {"start": v(-1120, 80.83) * mm, "end": v(-1050, 40.41) * mm});
            skLineSegment(sketch, "E1641.MirrorCS", {"start": v(-1690, 790.97) * mm, "end": v(-1760, 750.56) * mm});
            skLineSegment(sketch, "E1642.MirrorCS", {"start": v(-880, 1050.78) * mm, "end": v(-950, 1010.36) * mm});
            skLineSegment(sketch, "E1643.MirrorCS", {"start": v(-880, 219.4) * mm, "end": v(-950, 178.98) * mm});
            skLineSegment(sketch, "E1644.MirrorCS", {"start": v(-890, 236.71) * mm, "end": v(-960, 196.3) * mm});
            skLineSegment(sketch, "E1645.MirrorCS", {"start": v(-960, 1304.81) * mm, "end": v(-1030, 1345.23) * mm});
            skLineSegment(sketch, "E1646.MirrorCS", {"start": v(-1590, 1760.92) * mm, "end": v(-1590, 1841.75) * mm});
            skLineSegment(sketch, "E1647.MirrorCS", {"start": v(-1440, 357.96) * mm, "end": v(-1510, 317.54) * mm});
            skLineSegment(sketch, "E1648.MirrorCS", {"start": v(-1430, 98.15) * mm, "end": v(-1360, 57.74) * mm});
            skLineSegment(sketch, "E1649.MirrorCS", {"start": v(-1760, 1466.47) * mm, "end": v(-1690, 1426.06) * mm});
            skLineSegment(sketch, "E1650.MirrorCS", {"start": v(-1670, 40.41) * mm, "end": v(-1670, -40.41) * mm});
            skLineSegment(sketch, "E1651.MirrorCS", {"start": v(-1610, 375.28) * mm, "end": v(-1680, 334.86) * mm});
            skLineSegment(sketch, "E1652.MirrorCS", {"start": v(-880, 889.12) * mm, "end": v(-950, 929.53) * mm});
            skLineSegment(sketch, "E1653.MirrorCS", {"start": v(-1530, 236.71) * mm, "end": v(-1600, 196.3) * mm});
            skLineSegment(sketch, "E1654.MirrorCS", {"start": v(-1670, 1703.18) * mm, "end": v(-1670, 1622.35) * mm});
            skLineSegment(sketch, "E1655.MirrorCS", {"start": v(-1030, 513.84) * mm, "end": v(-1030, 594.67) * mm});
            skLineSegment(sketch, "E1656.MirrorCS", {"start": v(-1210, 1068.1) * mm, "end": v(-1280, 1027.68) * mm});
            skLineSegment(sketch, "E1657.MirrorCS", {"start": v(-1760, -80.83) * mm, "end": v(-1830, -40.41) * mm});
            skLineSegment(sketch, "E1658.MirrorCS", {"start": v(-810, 1287.5) * mm, "end": v(-880, 1327.9) * mm});
            skLineSegment(sketch, "E1659.MirrorCS", {"start": v(-1030, 1426.06) * mm, "end": v(-960, 1466.47) * mm});
            skLineSegment(sketch, "E1660.MirrorCS", {"start": v(-1210, -40.41) * mm, "end": v(-1210, 40.41) * mm});
            skLineSegment(sketch, "E1661.MirrorCS", {"start": v(-1350, 790.97) * mm, "end": v(-1280, 750.56) * mm});
            skLineSegment(sketch, "E1662.MirrorCS", {"start": v(-1670, 317.54) * mm, "end": v(-1600, 357.96) * mm});
            skLineSegment(sketch, "E1663.MirrorCS", {"start": v(-870, 1148.93) * mm, "end": v(-870, 1068.1) * mm});
            skLineSegment(sketch, "E1664.MirrorCS", {"start": v(-1680, 57.74) * mm, "end": v(-1750, 98.15) * mm});
            skLineSegment(sketch, "E1665.MirrorCS", {"start": v(-1830, 790.97) * mm, "end": v(-1760, 750.56) * mm});
            skLineSegment(sketch, "E1666.MirrorCS", {"start": v(-1190, 513.84) * mm, "end": v(-1120, 473.43) * mm});
            skLineSegment(sketch, "E1667.MirrorCS", {"start": v(-1040, 219.4) * mm, "end": v(-970, 178.98) * mm});
            skLineSegment(sketch, "E1668.MirrorCS", {"start": v(-1210, 1426.06) * mm, "end": v(-1210, 1345.23) * mm});
            skLineSegment(sketch, "E1669.MirrorCS", {"start": v(-1440, 1027.68) * mm, "end": v(-1370, 1068.1) * mm});
            skLineSegment(sketch, "E1670.MirrorCS", {"start": v(-950, 1564.62) * mm, "end": v(-950, 1483.8) * mm});
            skLineSegment(sketch, "E1671.MirrorCS", {"start": v(-1370, 594.67) * mm, "end": v(-1440, 635.09) * mm});
            skLineSegment(sketch, "E1672.MirrorCS", {"start": v(-1360, 612) * mm, "end": v(-1290, 652.4) * mm});
            skLineSegment(sketch, "E1673.MirrorCS", {"start": v(-1360, 334.86) * mm, "end": v(-1430, 375.28) * mm});
            skLineSegment(sketch, "E1674.MirrorCS", {"start": v(-1770, 1760.92) * mm, "end": v(-1770, 1841.75) * mm});
            skLineSegment(sketch, "E1675.MirrorCS", {"start": v(-1200, 612) * mm, "end": v(-1130, 652.4) * mm});
            skLineSegment(sketch, "E1676.MirrorCS", {"start": v(-1120, 1743.6) * mm, "end": v(-1050, 1703.18) * mm});
            skLineSegment(sketch, "E1677.MirrorCS", {"start": v(-1360, 57.74) * mm, "end": v(-1290, 98.15) * mm});
            skLineSegment(sketch, "E1678.MirrorCS", {"start": v(-1680, 334.86) * mm, "end": v(-1750, 375.28) * mm});
            skLineSegment(sketch, "E1679.MirrorCS", {"start": v(-880, 889.12) * mm, "end": v(-810, 929.53) * mm});
            skLineSegment(sketch, "E1680.MirrorCS", {"start": v(-1280, 635.09) * mm, "end": v(-1350, 594.67) * mm});
            skLineSegment(sketch, "E1681.MirrorCS", {"start": v(-1270, 929.53) * mm, "end": v(-1270, 1010.36) * mm});
            skLineSegment(sketch, "E1682.MirrorCS", {"start": v(-1670, 236.71) * mm, "end": v(-1670, 317.54) * mm});
            skLineSegment(sketch, "E1683.MirrorCS", {"start": v(-1520, 496.52) * mm, "end": v(-1590, 456.1) * mm});
            skLineSegment(sketch, "E1684.MirrorCS", {"start": v(-1520, 219.4) * mm, "end": v(-1590, 178.98) * mm});
            skLineSegment(sketch, "E1685.MirrorCS", {"start": v(-970, 929.53) * mm, "end": v(-970, 1010.36) * mm});
            skLineSegment(sketch, "E1686.MirrorCS", {"start": v(-1040, 334.86) * mm, "end": v(-970, 375.28) * mm});
            skLineSegment(sketch, "E1687.MirrorCS", {"start": v(-1270, 1206.66) * mm, "end": v(-1200, 1166.25) * mm});
            skLineSegment(sketch, "E1688.MirrorCS", {"start": v(-810, 652.4) * mm, "end": v(-880, 612) * mm});
            skLineSegment(sketch, "E1689.MirrorCS", {"start": v(-1030, 236.71) * mm, "end": v(-1030, 317.54) * mm});
            skLineSegment(sketch, "E1690.MirrorCS", {"start": v(-1910, 1010.36) * mm, "end": v(-1840, 1050.78) * mm});
            skLineSegment(sketch, "E1691.MirrorCS", {"start": v(-1130, 1010.36) * mm, "end": v(-1130, 929.53) * mm});
            skLineSegment(sketch, "E1692.MirrorCS", {"start": v(-1200, 773.65) * mm, "end": v(-1270, 733.23) * mm});
            skLineSegment(sketch, "E1693.MirrorCS", {"start": v(-1280, 750.56) * mm, "end": v(-1210, 790.97) * mm});
            skLineSegment(sketch, "E1694.MirrorCS", {"start": v(-1590, 1206.66) * mm, "end": v(-1590, 1287.5) * mm});
            skLineSegment(sketch, "E1695.MirrorCS", {"start": v(-1770, 1010.36) * mm, "end": v(-1770, 929.53) * mm});
            skLineSegment(sketch, "E1696.MirrorCS", {"start": v(-1110, 929.53) * mm, "end": v(-1040, 889.12) * mm});
            skLineSegment(sketch, "E1697.MirrorCS", {"start": v(-870, 594.67) * mm, "end": v(-870, 513.84) * mm});
            skLineSegment(sketch, "E1698.MirrorCS", {"start": v(-1350, 1345.23) * mm, "end": v(-1350, 1426.06) * mm});
            skLineSegment(sketch, "E1699.MirrorCS", {"start": v(-1510, 1622.35) * mm, "end": v(-1510, 1703.18) * mm});
            skLineSegment(sketch, "E1700.MirrorCS", {"start": v(-1770, 456.1) * mm, "end": v(-1770, 375.28) * mm});
            skLineSegment(sketch, "E1701.MirrorCS", {"start": v(-1110, 1760.92) * mm, "end": v(-1110, 1841.75) * mm});
            skLineSegment(sketch, "E1702.MirrorCS", {"start": v(-1040, 612) * mm, "end": v(-1110, 652.4) * mm});
            skLineSegment(sketch, "E1703.MirrorCS", {"start": v(-1510, 1068.1) * mm, "end": v(-1440, 1027.68) * mm});
            skLineSegment(sketch, "E1704.MirrorCS", {"start": v(-1670, 1068.1) * mm, "end": v(-1670, 1148.93) * mm});
            skLineSegment(sketch, "E1705.MirrorCS", {"start": v(-1600, 1743.6) * mm, "end": v(-1670, 1703.18) * mm});
            skLineSegment(sketch, "E1706.MirrorCS", {"start": v(-1750, 98.15) * mm, "end": v(-1750, 178.98) * mm});
            skLineSegment(sketch, "E1707.MirrorCS", {"start": v(-1910, 652.4) * mm, "end": v(-1840, 612) * mm});
            skLineSegment(sketch, "E1708.MirrorCS", {"start": v(-1530, 790.97) * mm, "end": v(-1600, 750.56) * mm});
            skLineSegment(sketch, "E1709.MirrorCS", {"start": v(-1210, 1426.06) * mm, "end": v(-1280, 1466.47) * mm});
            skLineSegment(sketch, "E1710.MirrorCS", {"start": v(-1590, 1564.62) * mm, "end": v(-1590, 1483.8) * mm});
            skLineSegment(sketch, "E1711.MirrorCS", {"start": v(-1840, 219.4) * mm, "end": v(-1910, 178.98) * mm});
            skLineSegment(sketch, "E1712.MirrorCS", {"start": v(-1050, 1345.23) * mm, "end": v(-1050, 1426.06) * mm});
            skLineSegment(sketch, "E1713.MirrorCS", {"start": v(-1280, 635.09) * mm, "end": v(-1210, 594.67) * mm});
            skLineSegment(sketch, "E1714.MirrorCS", {"start": v(-1510, 40.41) * mm, "end": v(-1440, 80.83) * mm});
            skLineSegment(sketch, "E1715.MirrorCS", {"start": v(-1440, 357.96) * mm, "end": v(-1370, 317.54) * mm});
            skLineSegment(sketch, "E1716.MirrorCS", {"start": v(-880, 334.86) * mm, "end": v(-950, 375.28) * mm});
            skLineSegment(sketch, "E1717.MirrorCS", {"start": v(-1840, 1327.9) * mm, "end": v(-1910, 1287.5) * mm});
            skLineSegment(sketch, "E1718.MirrorCS", {"start": v(-870, 790.97) * mm, "end": v(-800, 750.56) * mm});
            skLineSegment(sketch, "E1719.MirrorCS", {"start": v(-1050, 871.8) * mm, "end": v(-1050, 790.97) * mm});
            skLineSegment(sketch, "E1720.MirrorCS", {"start": v(-1190, 40.41) * mm, "end": v(-1120, 80.83) * mm});
            skLineSegment(sketch, "E1721.MirrorCS", {"start": v(-1030, 871.8) * mm, "end": v(-1030, 790.97) * mm});
            skLineSegment(sketch, "E1722.MirrorCS", {"start": v(-1840, 1443.38) * mm, "end": v(-1770, 1483.8) * mm});
            skLineSegment(sketch, "E1723.MirrorCS", {"start": v(-1030, 1622.35) * mm, "end": v(-960, 1581.94) * mm});
            skLineSegment(sketch, "E1724.MirrorCS", {"start": v(-1120, 1189.34) * mm, "end": v(-1050, 1148.93) * mm});
            skLineSegment(sketch, "E1725.MirrorCS", {"start": v(-1430, 1010.36) * mm, "end": v(-1360, 1050.78) * mm});
            skLineSegment(sketch, "E1726.MirrorCS", {"start": v(-880, 1605.03) * mm, "end": v(-950, 1564.62) * mm});
            skLineSegment(sketch, "E1727.MirrorCS", {"start": v(-1530, 1622.35) * mm, "end": v(-1530, 1703.18) * mm});
            skLineSegment(sketch, "E1728.MirrorCS", {"start": v(-1290, 1760.92) * mm, "end": v(-1290, 1841.75) * mm});
            skLineSegment(sketch, "E1729.MirrorCS", {"start": v(-1110, 456.1) * mm, "end": v(-1110, 375.28) * mm});
            skLineSegment(sketch, "E1730.MirrorCS", {"start": v(-810, 178.98) * mm, "end": v(-880, 219.4) * mm});
            skLineSegment(sketch, "E1731.MirrorCS", {"start": v(-1360, 1050.78) * mm, "end": v(-1290, 1010.36) * mm});
            skLineSegment(sketch, "E1732.MirrorCS", {"start": v(-880, 1327.9) * mm, "end": v(-950, 1287.5) * mm});
            skLineSegment(sketch, "E1733.MirrorCS", {"start": v(-1610, 1206.66) * mm, "end": v(-1680, 1166.25) * mm});
            skLineSegment(sketch, "E1734.MirrorCS", {"start": v(-1440, 1304.81) * mm, "end": v(-1370, 1345.23) * mm});
            skLineSegment(sketch, "E1735.MirrorCS", {"start": v(-1770, 375.28) * mm, "end": v(-1840, 334.86) * mm});
            skLineSegment(sketch, "E1736.MirrorCS", {"start": v(-1520, 1882.16) * mm, "end": v(-1590, 1841.75) * mm});
            skLineSegment(sketch, "E1737.MirrorCS", {"start": v(-1130, 652.4) * mm, "end": v(-1130, 733.23) * mm});
            skLineSegment(sketch, "E1738.MirrorCS", {"start": v(-1670, 1622.35) * mm, "end": v(-1600, 1581.94) * mm});
            skLineSegment(sketch, "E1739.MirrorCS", {"start": v(-1110, 1010.36) * mm, "end": v(-1110, 929.53) * mm});
            skLineSegment(sketch, "E1740.MirrorCS", {"start": v(-1590, 733.23) * mm, "end": v(-1520, 773.65) * mm});
            skLineSegment(sketch, "E1741.MirrorCS", {"start": v(-1120, 1304.81) * mm, "end": v(-1050, 1345.23) * mm});
            skLineSegment(sketch, "E1742.MirrorCS", {"start": v(-1770, 1287.5) * mm, "end": v(-1840, 1327.9) * mm});
            skLineSegment(sketch, "E1743.MirrorCS", {"start": v(-1670, 790.97) * mm, "end": v(-1600, 750.56) * mm});
            skLineSegment(sketch, "E1744.MirrorCS", {"start": v(-1530, 1426.06) * mm, "end": v(-1600, 1466.47) * mm});
            skLineSegment(sketch, "E1745.MirrorCS", {"start": v(-1590, 1483.8) * mm, "end": v(-1520, 1443.38) * mm});
            skLineSegment(sketch, "E1746.MirrorCS", {"start": v(-1360, 496.52) * mm, "end": v(-1290, 456.1) * mm});
            skLineSegment(sketch, "E1747.MirrorCS", {"start": v(-1690, 1148.93) * mm, "end": v(-1760, 1189.34) * mm});
            skLineSegment(sketch, "E1748.MirrorCS", {"start": v(-1200, 1882.16) * mm, "end": v(-1130, 1841.75) * mm});
            skLineSegment(sketch, "E1749.MirrorCS", {"start": v(-1050, 236.71) * mm, "end": v(-1050, 317.54) * mm});
            skLineSegment(sketch, "E1750.MirrorCS", {"start": v(-970, 1841.75) * mm, "end": v(-1040, 1882.16) * mm});
            skLineSegment(sketch, "E1751.MirrorCS", {"start": v(-890, 594.67) * mm, "end": v(-960, 635.09) * mm});
            skLineSegment(sketch, "E1752.MirrorCS", {"start": v(-970, 929.53) * mm, "end": v(-1040, 889.12) * mm});
            skLineSegment(sketch, "E1753.MirrorCS", {"start": v(-1360, 1720.5) * mm, "end": v(-1290, 1760.92) * mm});
            skLineSegment(sketch, "E1754.MirrorCS", {"start": v(-890, 40.41) * mm, "end": v(-960, 80.83) * mm});
            skLineSegment(sketch, "E1755.MirrorCS", {"start": v(-1200, 1443.38) * mm, "end": v(-1130, 1483.8) * mm});
            skLineSegment(sketch, "E1756.MirrorCS", {"start": v(-810, 98.15) * mm, "end": v(-880, 57.74) * mm});
            skLineSegment(sketch, "E1757.MirrorCS", {"start": v(-1830, 1426.06) * mm, "end": v(-1830, 1345.23) * mm});
            skLineSegment(sketch, "E1758.MirrorCS", {"start": v(-1590, 98.15) * mm, "end": v(-1590, 178.98) * mm});
            skLineSegment(sketch, "E1759.MirrorCS", {"start": v(-810, 1206.66) * mm, "end": v(-810, 1287.5) * mm});
            skLineSegment(sketch, "E1760.MirrorCS", {"start": v(-1680, 1050.78) * mm, "end": v(-1750, 1010.36) * mm});
            skLineSegment(sketch, "E1761.MirrorCS", {"start": v(-1530, 871.8) * mm, "end": v(-1600, 912.21) * mm});
            skLineSegment(sketch, "E1762.MirrorCS", {"start": v(-950, 1010.36) * mm, "end": v(-950, 929.53) * mm});
            skLineSegment(sketch, "E1763.MirrorCS", {"start": v(-1450, 733.23) * mm, "end": v(-1520, 773.65) * mm});
            skLineSegment(sketch, "E1764.MirrorCS", {"start": v(-1520, 1327.9) * mm, "end": v(-1590, 1287.5) * mm});
            skLineSegment(sketch, "E1765.MirrorCS", {"start": v(-1610, 375.28) * mm, "end": v(-1610, 456.1) * mm});
            skLineSegment(sketch, "E1766.MirrorCS", {"start": v(-960, 750.56) * mm, "end": v(-1030, 790.97) * mm});
            skLineSegment(sketch, "E1767.MirrorCS", {"start": v(-1440, 1466.47) * mm, "end": v(-1510, 1426.06) * mm});
            skLineSegment(sketch, "E1768.MirrorCS", {"start": v(-1200, 773.65) * mm, "end": v(-1130, 733.23) * mm});
            skLineSegment(sketch, "E1769.MirrorCS", {"start": v(-810, 456.1) * mm, "end": v(-880, 496.52) * mm});
            skLineSegment(sketch, "E1770.MirrorCS", {"start": v(-1680, 1605.03) * mm, "end": v(-1750, 1564.62) * mm});
            skLineSegment(sketch, "E1771.MirrorCS", {"start": v(-1270, 456.1) * mm, "end": v(-1200, 496.52) * mm});
            skLineSegment(sketch, "E1772.MirrorCS", {"start": v(-1830, 236.71) * mm, "end": v(-1760, 196.3) * mm});
            skLineSegment(sketch, "E1773.MirrorCS", {"start": v(-960, 1743.6) * mm, "end": v(-1030, 1703.18) * mm});
            skLineSegment(sketch, "E1774.MirrorCS", {"start": v(-970, 1564.62) * mm, "end": v(-1040, 1605.03) * mm});
            skLineSegment(sketch, "E1775.MirrorCS", {"start": v(-1530, 1426.06) * mm, "end": v(-1530, 1345.23) * mm});
            skLineSegment(sketch, "E1776.MirrorCS", {"start": v(-1530, 1703.18) * mm, "end": v(-1600, 1743.6) * mm});
            skLineSegment(sketch, "E1777.MirrorCS", {"start": v(-1120, 912.21) * mm, "end": v(-1050, 871.8) * mm});
            skLineSegment(sketch, "E1778.MirrorCS", {"start": v(-1200, 1166.25) * mm, "end": v(-1130, 1206.66) * mm});
            skLineSegment(sketch, "E1779.MirrorCS", {"start": v(-1350, 236.71) * mm, "end": v(-1350, 317.54) * mm});
            skLineSegment(sketch, "E1780.MirrorCS", {"start": v(-1590, 929.53) * mm, "end": v(-1520, 889.12) * mm});
            skLineSegment(sketch, "E1781.MirrorCS", {"start": v(-880, 1720.5) * mm, "end": v(-950, 1760.92) * mm});
            skLineSegment(sketch, "E1782.MirrorCS", {"start": v(-1210, 594.67) * mm, "end": v(-1210, 513.84) * mm});
            skLineSegment(sketch, "E1783.MirrorCS", {"start": v(-970, 1841.75) * mm, "end": v(-970, 1760.92) * mm});
            skLineSegment(sketch, "E1784.MirrorCS", {"start": v(-1840, 612) * mm, "end": v(-1770, 652.4) * mm});
            skLineSegment(sketch, "E1785.MirrorCS", {"start": v(-1830, 1622.35) * mm, "end": v(-1830, 1703.18) * mm});
            skLineSegment(sketch, "E1786.MirrorCS", {"start": v(-1770, 1564.62) * mm, "end": v(-1770, 1483.8) * mm});
            skLineSegment(sketch, "E1787.MirrorCS", {"start": v(-1350, 40.41) * mm, "end": v(-1350, -40.41) * mm});
            skLineSegment(sketch, "E1788.MirrorCS", {"start": v(-1290, 375.28) * mm, "end": v(-1360, 334.86) * mm});
            skLineSegment(sketch, "E1789.MirrorCS", {"start": v(-1270, 1841.75) * mm, "end": v(-1270, 1760.92) * mm});
            skLineSegment(sketch, "E1790.MirrorCS", {"start": v(-1050, 317.54) * mm, "end": v(-1120, 357.96) * mm});
            skLineSegment(sketch, "E1791.MirrorCS", {"start": v(-1450, 733.23) * mm, "end": v(-1450, 652.4) * mm});
            skLineSegment(sketch, "E1792.MirrorCS", {"start": v(-1030, 594.67) * mm, "end": v(-960, 635.09) * mm});
            skLineSegment(sketch, "E1793.MirrorCS", {"start": v(-1270, 375.28) * mm, "end": v(-1270, 456.1) * mm});
            skLineSegment(sketch, "E1794.MirrorCS", {"start": v(-870, 1622.35) * mm, "end": v(-870, 1703.18) * mm});
            skLineSegment(sketch, "E1795.MirrorCS", {"start": v(-1130, 929.53) * mm, "end": v(-1200, 889.12) * mm});
            skLineSegment(sketch, "E1796.MirrorCS", {"start": v(-810, 1564.62) * mm, "end": v(-880, 1605.03) * mm});
            skLineSegment(sketch, "E1797.MirrorCS", {"start": v(-1750, 652.4) * mm, "end": v(-1750, 733.23) * mm});
            skLineSegment(sketch, "E1798.MirrorCS", {"start": v(-1040, 773.65) * mm, "end": v(-970, 733.23) * mm});
            skLineSegment(sketch, "E1799.MirrorCS", {"start": v(-1270, 733.23) * mm, "end": v(-1270, 652.4) * mm});
            skLineSegment(sketch, "E1800.MirrorCS", {"start": v(-1050, 513.84) * mm, "end": v(-1050, 594.67) * mm});
            skLineSegment(sketch, "E1801.MirrorCS", {"start": v(-1210, 236.71) * mm, "end": v(-1280, 196.3) * mm});
            skLineSegment(sketch, "E1802.MirrorCS", {"start": v(-1910, 1841.75) * mm, "end": v(-1840, 1882.16) * mm});
            skLineSegment(sketch, "E1803.MirrorCS", {"start": v(-970, 456.1) * mm, "end": v(-1040, 496.52) * mm});
            skLineSegment(sketch, "E1804.MirrorCS", {"start": v(-1690, 1703.18) * mm, "end": v(-1690, 1622.35) * mm});
            skLineSegment(sketch, "E1805.MirrorCS", {"start": v(-1450, 98.15) * mm, "end": v(-1520, 57.74) * mm});
            skLineSegment(sketch, "E1806.MirrorCS", {"start": v(-1350, 1148.93) * mm, "end": v(-1280, 1189.34) * mm});
            skLineSegment(sketch, "E1807.MirrorCS", {"start": v(-1610, 1483.8) * mm, "end": v(-1680, 1443.38) * mm});
            skLineSegment(sketch, "E1808.MirrorCS", {"start": v(-1910, 456.1) * mm, "end": v(-1840, 496.52) * mm});
            skLineSegment(sketch, "E1809.MirrorCS", {"start": v(-1120, 1581.94) * mm, "end": v(-1190, 1622.35) * mm});
            skLineSegment(sketch, "E1810.MirrorCS", {"start": v(-970, 1206.66) * mm, "end": v(-1040, 1166.25) * mm});
            skLineSegment(sketch, "E1811.MirrorCS", {"start": v(-1040, 1050.78) * mm, "end": v(-1110, 1010.36) * mm});
            skLineSegment(sketch, "E1812.MirrorCS", {"start": v(-1050, 1703.18) * mm, "end": v(-1050, 1622.35) * mm});
            skLineSegment(sketch, "E1813.MirrorCS", {"start": v(-1360, 889.12) * mm, "end": v(-1290, 929.53) * mm});
            skLineSegment(sketch, "E1814.MirrorCS", {"start": v(-1830, 1426.06) * mm, "end": v(-1760, 1466.47) * mm});
            skLineSegment(sketch, "E1815.MirrorCS", {"start": v(-1130, 1287.5) * mm, "end": v(-1200, 1327.9) * mm});
            skLineSegment(sketch, "E1816.MirrorCS", {"start": v(-810, 652.4) * mm, "end": v(-810, 733.23) * mm});
            skLineSegment(sketch, "E1817.MirrorCS", {"start": v(-1600, 1466.47) * mm, "end": v(-1670, 1426.06) * mm});
            skLineSegment(sketch, "E1818.MirrorCS", {"start": v(-1770, 652.4) * mm, "end": v(-1770, 733.23) * mm});
            skLineSegment(sketch, "E1819.MirrorCS", {"start": v(-1760, 1027.68) * mm, "end": v(-1690, 1068.1) * mm});
            skLineSegment(sketch, "E1820.MirrorCS", {"start": v(-1830, -40.41) * mm, "end": v(-1830, 40.41) * mm});
            skLineSegment(sketch, "E1821.MirrorCS", {"start": v(-1200, 1882.16) * mm, "end": v(-1270, 1841.75) * mm});
            skLineSegment(sketch, "E1822.MirrorCS", {"start": v(-1830, 594.67) * mm, "end": v(-1760, 635.09) * mm});
            skLineSegment(sketch, "E1823.MirrorCS", {"start": v(-960, 1189.34) * mm, "end": v(-890, 1148.93) * mm});
            skLineSegment(sketch, "E1824.MirrorCS", {"start": v(-1760, 912.21) * mm, "end": v(-1690, 871.8) * mm});
            skLineSegment(sketch, "E1825.MirrorCS", {"start": v(-1430, 733.23) * mm, "end": v(-1430, 652.4) * mm});
            skLineSegment(sketch, "E1826.MirrorCS", {"start": v(-970, 1287.5) * mm, "end": v(-970, 1206.66) * mm});
            skLineSegment(sketch, "E1827.MirrorCS", {"start": v(-1430, 178.98) * mm, "end": v(-1430, 98.15) * mm});
            skLineSegment(sketch, "E1828.MirrorCS", {"start": v(-1450, 652.4) * mm, "end": v(-1520, 612) * mm});
            skLineSegment(sketch, "E1829.MirrorCS", {"start": v(-1270, 178.98) * mm, "end": v(-1270, 98.15) * mm});
            skLineSegment(sketch, "E1830.MirrorCS", {"start": v(-1910, 1841.75) * mm, "end": v(-1910, 1760.92) * mm});
            skLineSegment(sketch, "E1831.MirrorCS", {"start": v(-1760, 1743.6) * mm, "end": v(-1690, 1703.18) * mm});
            skLineSegment(sketch, "E1832.MirrorCS", {"start": v(-1910, 1287.5) * mm, "end": v(-1910, 1206.66) * mm});
            skLineSegment(sketch, "E1833.MirrorCS", {"start": v(-1270, 98.15) * mm, "end": v(-1200, 57.74) * mm});
            skLineSegment(sketch, "E1834.MirrorCS", {"start": v(-1750, 1287.5) * mm, "end": v(-1680, 1327.9) * mm});
            skLineSegment(sketch, "E1835.MirrorCS", {"start": v(-1040, 219.4) * mm, "end": v(-1110, 178.98) * mm});
            skLineSegment(sketch, "E1836.MirrorCS", {"start": v(-1210, 40.41) * mm, "end": v(-1280, 80.83) * mm});
            skLineSegment(sketch, "E1837.MirrorCS", {"start": v(-1680, 889.12) * mm, "end": v(-1610, 929.53) * mm});
            skLineSegment(sketch, "E1838.MirrorCS", {"start": v(-1510, 790.97) * mm, "end": v(-1510, 871.8) * mm});
            skLineSegment(sketch, "E1839.MirrorCS", {"start": v(-950, 1841.75) * mm, "end": v(-880, 1882.16) * mm});
            skLineSegment(sketch, "E1840.MirrorCS", {"start": v(-1610, 456.1) * mm, "end": v(-1680, 496.52) * mm});
            skLineSegment(sketch, "E1841.MirrorCS", {"start": v(-970, 1287.5) * mm, "end": v(-1040, 1327.9) * mm});
            skLineSegment(sketch, "E1842.MirrorCS", {"start": v(-960, 1466.47) * mm, "end": v(-890, 1426.06) * mm});
            skLineSegment(sketch, "E1843.MirrorCS", {"start": v(-1210, 1345.23) * mm, "end": v(-1280, 1304.81) * mm});
            skLineSegment(sketch, "E1844.MirrorCS", {"start": v(-1360, 1605.03) * mm, "end": v(-1290, 1564.62) * mm});
            skLineSegment(sketch, "E1845.MirrorCS", {"start": v(-1130, 178.98) * mm, "end": v(-1200, 219.4) * mm});
            skLineSegment(sketch, "E1846.MirrorCS", {"start": v(-1430, 1287.5) * mm, "end": v(-1430, 1206.66) * mm});
            skLineSegment(sketch, "E1847.MirrorCS", {"start": v(-1530, 1622.35) * mm, "end": v(-1600, 1581.94) * mm});
            skLineSegment(sketch, "E1848.MirrorCS", {"start": v(-1670, 513.84) * mm, "end": v(-1670, 594.67) * mm});
            skLineSegment(sketch, "E1849.MirrorCS", {"start": v(-1600, 1189.34) * mm, "end": v(-1530, 1148.93) * mm});
            skLineSegment(sketch, "E1850.MirrorCS", {"start": v(-1430, 652.4) * mm, "end": v(-1360, 612) * mm});
            skLineSegment(sketch, "E1851.MirrorCS", {"start": v(-1440, 912.21) * mm, "end": v(-1370, 871.8) * mm});
            skLineSegment(sketch, "E1852.MirrorCS", {"start": v(-1760, 357.96) * mm, "end": v(-1690, 317.54) * mm});
            skLineSegment(sketch, "E1853.MirrorCS", {"start": v(-1440, 1189.34) * mm, "end": v(-1510, 1148.93) * mm});
            skLineSegment(sketch, "E1854.MirrorCS", {"start": v(-1190, 790.97) * mm, "end": v(-1190, 871.8) * mm});
            skLineSegment(sketch, "E1855.MirrorCS", {"start": v(-1690, 871.8) * mm, "end": v(-1690, 790.97) * mm});
            skLineSegment(sketch, "E1856.MirrorCS", {"start": v(-1750, 1206.66) * mm, "end": v(-1750, 1287.5) * mm});
            skLineSegment(sketch, "E1857.MirrorCS", {"start": v(-1750, 1483.8) * mm, "end": v(-1680, 1443.38) * mm});
            skLineSegment(sketch, "E1858.MirrorCS", {"start": v(-1600, 196.3) * mm, "end": v(-1670, 236.71) * mm});
            skLineSegment(sketch, "E1859.MirrorCS", {"start": v(-1280, 357.96) * mm, "end": v(-1350, 317.54) * mm});
            skLineSegment(sketch, "E1860.MirrorCS", {"start": v(-880, 496.52) * mm, "end": v(-950, 456.1) * mm});
            skLineSegment(sketch, "E1861.MirrorCS", {"start": v(-890, 513.84) * mm, "end": v(-960, 473.43) * mm});
            skLineSegment(sketch, "E1862.MirrorCS", {"start": v(-1430, 375.28) * mm, "end": v(-1430, 456.1) * mm});
            skLineSegment(sketch, "E1863.MirrorCS", {"start": v(-1210, 1148.93) * mm, "end": v(-1210, 1068.1) * mm});
            skLineSegment(sketch, "E1864.MirrorCS", {"start": v(-1440, 196.3) * mm, "end": v(-1370, 236.71) * mm});
            skLineSegment(sketch, "E1865.MirrorCS", {"start": v(-1670, 1345.23) * mm, "end": v(-1670, 1426.06) * mm});
            skLineSegment(sketch, "E1866.MirrorCS", {"start": v(-1370, 1703.18) * mm, "end": v(-1370, 1622.35) * mm});
            skLineSegment(sketch, "E1867.MirrorCS", {"start": v(-1760, 1304.81) * mm, "end": v(-1690, 1345.23) * mm});
            skLineSegment(sketch, "E1868.MirrorCS", {"start": v(-1510, 1148.93) * mm, "end": v(-1510, 1068.1) * mm});
            skLineSegment(sketch, "E1869.MirrorCS", {"start": v(-1270, 1483.8) * mm, "end": v(-1270, 1564.62) * mm});
            skLineSegment(sketch, "E1870.MirrorCS", {"start": v(-960, 1027.68) * mm, "end": v(-1030, 1068.1) * mm});
            skLineSegment(sketch, "E1871.MirrorCS", {"start": v(-1210, 1703.18) * mm, "end": v(-1280, 1743.6) * mm});
            skLineSegment(sketch, "E1872.MirrorCS", {"start": v(-1190, 1622.35) * mm, "end": v(-1190, 1703.18) * mm});
            skLineSegment(sketch, "E1873.MirrorCS", {"start": v(-810, 733.23) * mm, "end": v(-880, 773.65) * mm});
            skLineSegment(sketch, "E1874.MirrorCS", {"start": v(-1450, 1483.8) * mm, "end": v(-1520, 1443.38) * mm});
            skLineSegment(sketch, "E1875.MirrorCS", {"start": v(-1510, 513.84) * mm, "end": v(-1440, 473.43) * mm});
            skLineSegment(sketch, "E1876.MirrorCS", {"start": v(-1450, 1841.75) * mm, "end": v(-1520, 1882.16) * mm});
            skLineSegment(sketch, "E1877.MirrorCS", {"start": v(-1130, 1206.66) * mm, "end": v(-1130, 1287.5) * mm});
            skLineSegment(sketch, "E1878.MirrorCS", {"start": v(-970, 1010.36) * mm, "end": v(-1040, 1050.78) * mm});
            skLineSegment(sketch, "E1879.MirrorCS", {"start": v(-1830, 40.41) * mm, "end": v(-1760, 80.83) * mm});
            skLineSegment(sketch, "E1880.MirrorCS", {"start": v(-810, 1760.92) * mm, "end": v(-880, 1720.5) * mm});
            skLineSegment(sketch, "E1881.MirrorCS", {"start": v(-1530, 790.97) * mm, "end": v(-1530, 871.8) * mm});
            skLineSegment(sketch, "E1882.MirrorCS", {"start": v(-1910, 1760.92) * mm, "end": v(-1840, 1720.5) * mm});
            skLineSegment(sketch, "E1883.MirrorCS", {"start": v(-1750, 929.53) * mm, "end": v(-1680, 889.12) * mm});
            skLineSegment(sketch, "E1884.MirrorCS", {"start": v(-1600, 912.21) * mm, "end": v(-1670, 871.8) * mm});
            skLineSegment(sketch, "E1885.MirrorCS", {"start": v(-1440, 1581.94) * mm, "end": v(-1510, 1622.35) * mm});
            skLineSegment(sketch, "E1886.MirrorCS", {"start": v(-1520, 334.86) * mm, "end": v(-1450, 375.28) * mm});
            skLineSegment(sketch, "E1887.MirrorCS", {"start": v(-1290, 1483.8) * mm, "end": v(-1360, 1443.38) * mm});
            skLineSegment(sketch, "E1888.MirrorCS", {"start": v(-1110, 375.28) * mm, "end": v(-1040, 334.86) * mm});
            skLineSegment(sketch, "E1889.MirrorCS", {"start": v(-1280, 80.83) * mm, "end": v(-1350, 40.41) * mm});
            skLineSegment(sketch, "E1890.MirrorCS", {"start": v(-890, 594.67) * mm, "end": v(-890, 513.84) * mm});
            skLineSegment(sketch, "E1891.MirrorCS", {"start": v(-1610, 733.23) * mm, "end": v(-1610, 652.4) * mm});
            skLineSegment(sketch, "E1892.MirrorCS", {"start": v(-1690, 236.71) * mm, "end": v(-1690, 317.54) * mm});
            skLineSegment(sketch, "E1893.MirrorCS", {"start": v(-960, 912.21) * mm, "end": v(-1030, 871.8) * mm});
            skLineSegment(sketch, "E1894.MirrorCS", {"start": v(-1050, 1426.06) * mm, "end": v(-1120, 1466.47) * mm});
            skLineSegment(sketch, "E1895.MirrorCS", {"start": v(-1360, 773.65) * mm, "end": v(-1430, 733.23) * mm});
            skLineSegment(sketch, "E1896.MirrorCS", {"start": v(-1430, 1760.92) * mm, "end": v(-1360, 1720.5) * mm});
            skLineSegment(sketch, "E1897.MirrorCS", {"start": v(-1030, 1703.18) * mm, "end": v(-1030, 1622.35) * mm});
            skLineSegment(sketch, "E1898.MirrorCS", {"start": v(-1200, 496.52) * mm, "end": v(-1130, 456.1) * mm});
            skLineSegment(sketch, "E1899.MirrorCS", {"start": v(-1610, 1287.5) * mm, "end": v(-1610, 1206.66) * mm});
            skLineSegment(sketch, "E1900.MirrorCS", {"start": v(-1210, 871.8) * mm, "end": v(-1280, 912.21) * mm});
            skLineSegment(sketch, "E1901.MirrorCS", {"start": v(-1190, 1703.18) * mm, "end": v(-1120, 1743.6) * mm});
            skLineSegment(sketch, "E1902.MirrorCS", {"start": v(-1190, 1426.06) * mm, "end": v(-1190, 1345.23) * mm});
            skLineSegment(sketch, "E1903.MirrorCS", {"start": v(-1450, 1287.5) * mm, "end": v(-1450, 1206.66) * mm});
            skLineSegment(sketch, "E1904.MirrorCS", {"start": v(-1760, 1581.94) * mm, "end": v(-1690, 1622.35) * mm});
            skLineSegment(sketch, "E1905.MirrorCS", {"start": v(-1610, 929.53) * mm, "end": v(-1610, 1010.36) * mm});
            skLineSegment(sketch, "E1906.MirrorCS", {"start": v(-1910, 1483.8) * mm, "end": v(-1910, 1564.62) * mm});
            skLineSegment(sketch, "E1907.MirrorCS", {"start": v(-1590, 652.4) * mm, "end": v(-1590, 733.23) * mm});
            skLineSegment(sketch, "E1908.MirrorCS", {"start": v(-1610, 1483.8) * mm, "end": v(-1610, 1564.62) * mm});
            skLineSegment(sketch, "E1909.MirrorCS", {"start": v(-1910, 733.23) * mm, "end": v(-1910, 652.4) * mm});
            skLineSegment(sketch, "E1910.MirrorCS", {"start": v(-970, 98.15) * mm, "end": v(-1040, 57.74) * mm});
            skLineSegment(sketch, "E1911.MirrorCS", {"start": v(-1210, 1622.35) * mm, "end": v(-1210, 1703.18) * mm});
            skLineSegment(sketch, "E1912.MirrorCS", {"start": v(-1350, 1703.18) * mm, "end": v(-1350, 1622.35) * mm});
            skLineSegment(sketch, "E1913.MirrorCS", {"start": v(-1830, 513.84) * mm, "end": v(-1760, 473.43) * mm});
            skLineSegment(sketch, "E1914.MirrorCS", {"start": v(-1590, 456.1) * mm, "end": v(-1590, 375.28) * mm});
            skLineSegment(sketch, "E1915.MirrorCS", {"start": v(-1770, 1841.75) * mm, "end": v(-1840, 1882.16) * mm});
            skLineSegment(sketch, "E1916.MirrorCS", {"start": v(-1270, 652.4) * mm, "end": v(-1200, 612) * mm});
            skLineSegment(sketch, "E1917.MirrorCS", {"start": v(-1030, 1345.23) * mm, "end": v(-1030, 1426.06) * mm});
            skLineSegment(sketch, "E1918.MirrorCS", {"start": v(-1030, 1068.1) * mm, "end": v(-1030, 1148.93) * mm});
            skLineSegment(sketch, "E1919.MirrorCS", {"start": v(-1670, 871.8) * mm, "end": v(-1670, 790.97) * mm});
            skLineSegment(sketch, "E1920.MirrorCS", {"start": v(-1840, 57.74) * mm, "end": v(-1770, 98.15) * mm});
            skLineSegment(sketch, "E1921.MirrorCS", {"start": v(-1280, 1189.34) * mm, "end": v(-1210, 1148.93) * mm});
            skLineSegment(sketch, "E1922.MirrorCS", {"start": v(-1830, 871.8) * mm, "end": v(-1760, 912.21) * mm});
            skLineSegment(sketch, "E1923.MirrorCS", {"start": v(-880, 612) * mm, "end": v(-950, 652.4) * mm});
            skLineSegment(sketch, "E1924.MirrorCS", {"start": v(-810, 375.28) * mm, "end": v(-880, 334.86) * mm});
            skLineSegment(sketch, "E1925.MirrorCS", {"start": v(-1370, 871.8) * mm, "end": v(-1370, 790.97) * mm});
            skLineSegment(sketch, "E1926.MirrorCS", {"start": v(-970, 178.98) * mm, "end": v(-970, 98.15) * mm});
            skLineSegment(sketch, "E1927.MirrorCS", {"start": v(-1350, -40.41) * mm, "end": v(-1280, -80.83) * mm});
            skLineSegment(sketch, "E1928.MirrorCS", {"start": v(-1510, 1426.06) * mm, "end": v(-1510, 1345.23) * mm});
            skLineSegment(sketch, "E1929.MirrorCS", {"start": v(-1910, 929.53) * mm, "end": v(-1910, 1010.36) * mm});
            skLineSegment(sketch, "E1930.MirrorCS", {"start": v(-880, 57.74) * mm, "end": v(-950, 98.15) * mm});
            skLineSegment(sketch, "E1931.MirrorCS", {"start": v(-1520, 612) * mm, "end": v(-1590, 652.4) * mm});
            skLineSegment(sketch, "E1932.MirrorCS", {"start": v(-1210, 317.54) * mm, "end": v(-1280, 357.96) * mm});
            skLineSegment(sketch, "E1933.MirrorCS", {"start": v(-1210, 790.97) * mm, "end": v(-1210, 871.8) * mm});
            skLineSegment(sketch, "E1934.MirrorCS", {"start": v(-1670, 1148.93) * mm, "end": v(-1600, 1189.34) * mm});
            skLineSegment(sketch, "E1935.MirrorCS", {"start": v(-1680, 1720.5) * mm, "end": v(-1750, 1760.92) * mm});
            skLineSegment(sketch, "E1936.MirrorCS", {"start": v(-1040, 57.74) * mm, "end": v(-1110, 98.15) * mm});
            skLineSegment(sketch, "E1937.MirrorCS", {"start": v(-1350, 1426.06) * mm, "end": v(-1280, 1466.47) * mm});
            skLineSegment(sketch, "E1938.MirrorCS", {"start": v(-1290, 456.1) * mm, "end": v(-1290, 375.28) * mm});
            skLineSegment(sketch, "E1939.MirrorCS", {"start": v(-1690, 513.84) * mm, "end": v(-1690, 594.67) * mm});
            skLineSegment(sketch, "E1940.MirrorCS", {"start": v(-1610, 1010.36) * mm, "end": v(-1680, 1050.78) * mm});
            skLineSegment(sketch, "E1941.MirrorCS", {"start": v(-810, 1206.66) * mm, "end": v(-880, 1166.25) * mm});
            skLineSegment(sketch, "E1942.MirrorCS", {"start": v(-810, 1760.92) * mm, "end": v(-810, 1841.75) * mm});
            skLineSegment(sketch, "E1943.MirrorCS", {"start": v(-1360, 889.12) * mm, "end": v(-1430, 929.53) * mm});
            skLineSegment(sketch, "E1944.MirrorCS", {"start": v(-1610, 1564.62) * mm, "end": v(-1680, 1605.03) * mm});
            skLineSegment(sketch, "E1945.MirrorCS", {"start": v(-1680, 612) * mm, "end": v(-1750, 652.4) * mm});
            skLineSegment(sketch, "E1946.MirrorCS", {"start": v(-1110, 1287.5) * mm, "end": v(-1040, 1327.9) * mm});
            skLineSegment(sketch, "E1947.MirrorCS", {"start": v(-1290, 1010.36) * mm, "end": v(-1290, 929.53) * mm});
            skLineSegment(sketch, "E1948.MirrorCS", {"start": v(-1750, 1564.62) * mm, "end": v(-1750, 1483.8) * mm});
            skLineSegment(sketch, "E1949.MirrorCS", {"start": v(-1360, 1327.9) * mm, "end": v(-1290, 1287.5) * mm});
            skLineSegment(sketch, "E1950.MirrorCS", {"start": v(-890, 1345.23) * mm, "end": v(-960, 1304.81) * mm});
            skLineSegment(sketch, "E1951.MirrorCS", {"start": v(-1510, 1345.23) * mm, "end": v(-1440, 1304.81) * mm});
            skLineSegment(sketch, "E1952.MirrorCS", {"start": v(-1910, 1206.66) * mm, "end": v(-1840, 1166.25) * mm});
            skLineSegment(sketch, "E1953.MirrorCS", {"start": v(-1600, 635.09) * mm, "end": v(-1530, 594.67) * mm});
            skLineSegment(sketch, "E1954.MirrorCS", {"start": v(-1430, 1564.62) * mm, "end": v(-1360, 1605.03) * mm});
            skLineSegment(sketch, "E1955.MirrorCS", {"start": v(-1910, 375.28) * mm, "end": v(-1840, 334.86) * mm});
            skLineSegment(sketch, "E1956.MirrorCS", {"start": v(-1750, 1010.36) * mm, "end": v(-1750, 929.53) * mm});
            skLineSegment(sketch, "E1957.MirrorCS", {"start": v(-1430, 929.53) * mm, "end": v(-1430, 1010.36) * mm});
            skLineSegment(sketch, "E1958.MirrorCS", {"start": v(-1280, 912.21) * mm, "end": v(-1350, 871.8) * mm});
            skLineSegment(sketch, "E1959.MirrorCS", {"start": v(-1610, 652.4) * mm, "end": v(-1680, 612) * mm});
            skLineSegment(sketch, "E1960.MirrorCS", {"start": v(-1610, 1841.75) * mm, "end": v(-1610, 1760.92) * mm});
            skLineSegment(sketch, "E1961.MirrorCS", {"start": v(-1430, 456.1) * mm, "end": v(-1360, 496.52) * mm});
            skLineSegment(sketch, "E1962.MirrorCS", {"start": v(-950, 652.4) * mm, "end": v(-950, 733.23) * mm});
            skLineSegment(sketch, "E1963.MirrorCS", {"start": v(-1200, 1050.78) * mm, "end": v(-1130, 1010.36) * mm});
            skLineSegment(sketch, "E1964.MirrorCS", {"start": v(-1200, 1720.5) * mm, "end": v(-1130, 1760.92) * mm});
            skLineSegment(sketch, "E1965.MirrorCS", {"start": v(-1130, 1564.62) * mm, "end": v(-1130, 1483.8) * mm});
            skLineSegment(sketch, "E1966.MirrorCS", {"start": v(-1600, 1027.68) * mm, "end": v(-1670, 1068.1) * mm});
            skLineSegment(sketch, "E1967.MirrorCS", {"start": v(-1520, 219.4) * mm, "end": v(-1450, 178.98) * mm});
            skLineSegment(sketch, "E1968.MirrorCS", {"start": v(-870, 236.71) * mm, "end": v(-800, 196.3) * mm});
            skLineSegment(sketch, "E1969.MirrorCS", {"start": v(-1190, 317.54) * mm, "end": v(-1190, 236.71) * mm});
            skLineSegment(sketch, "E1970.MirrorCS", {"start": v(-1440, 473.43) * mm, "end": v(-1370, 513.84) * mm});
            skLineSegment(sketch, "E1971.MirrorCS", {"start": v(-890, 317.54) * mm, "end": v(-890, 236.71) * mm});
            skLineSegment(sketch, "E1972.MirrorCS", {"start": v(-1270, 1760.92) * mm, "end": v(-1200, 1720.5) * mm});
            skLineSegment(sketch, "E1973.MirrorCS", {"start": v(-1530, 1068.1) * mm, "end": v(-1600, 1027.68) * mm});
            skLineSegment(sketch, "E1974.MirrorCS", {"start": v(-1350, 1068.1) * mm, "end": v(-1350, 1148.93) * mm});
            skLineSegment(sketch, "E1975.MirrorCS", {"start": v(-1110, 1564.62) * mm, "end": v(-1110, 1483.8) * mm});
            skLineSegment(sketch, "E1976.MirrorCS", {"start": v(-1290, 733.23) * mm, "end": v(-1360, 773.65) * mm});
            skLineSegment(sketch, "E1977.MirrorCS", {"start": v(-1370, 40.41) * mm, "end": v(-1370, -40.41) * mm});
            skLineSegment(sketch, "E1978.MirrorCS", {"start": v(-1190, 1148.93) * mm, "end": v(-1190, 1068.1) * mm});
            skLineSegment(sketch, "E1979.MirrorCS", {"start": v(-950, 1483.8) * mm, "end": v(-880, 1443.38) * mm});
            skLineSegment(sketch, "E1980.MirrorCS", {"start": v(-1040, 1720.5) * mm, "end": v(-1110, 1760.92) * mm});
            skLineSegment(sketch, "E1981.MirrorCS", {"start": v(-1690, -40.41) * mm, "end": v(-1760, -80.83) * mm});
            skLineSegment(sketch, "E1982.MirrorCS", {"start": v(-970, 1760.92) * mm, "end": v(-1040, 1720.5) * mm});
            skLineSegment(sketch, "E1983.MirrorCS", {"start": v(-970, 733.23) * mm, "end": v(-970, 652.4) * mm});
            skLineSegment(sketch, "E1984.MirrorCS", {"start": v(-960, 80.83) * mm, "end": v(-1030, 40.41) * mm});
            skLineSegment(sketch, "E1985.MirrorCS", {"start": v(-950, 1760.92) * mm, "end": v(-950, 1841.75) * mm});
            skLineSegment(sketch, "E1986.MirrorCS", {"start": v(-1040, 1443.38) * mm, "end": v(-970, 1483.8) * mm});
            skLineSegment(sketch, "E1987.MirrorCS", {"start": v(-1120, 1027.68) * mm, "end": v(-1050, 1068.1) * mm});
            skLineSegment(sketch, "E1988.MirrorCS", {"start": v(-890, 1068.1) * mm, "end": v(-960, 1027.68) * mm});
            skLineSegment(sketch, "E1989.MirrorCS", {"start": v(-1430, 1483.8) * mm, "end": v(-1430, 1564.62) * mm});
            skLineSegment(sketch, "E1990.MirrorCS", {"start": v(-1690, 40.41) * mm, "end": v(-1690, -40.41) * mm});
            skLineSegment(sketch, "E1991.MirrorCS", {"start": v(-890, 1622.35) * mm, "end": v(-890, 1703.18) * mm});
            skLineSegment(sketch, "E1992.MirrorCS", {"start": v(-1830, 594.67) * mm, "end": v(-1830, 513.84) * mm});
            skLineSegment(sketch, "E1993.MirrorCS", {"start": v(-870, 317.54) * mm, "end": v(-870, 236.71) * mm});
            skLineSegment(sketch, "E1994.MirrorCS", {"start": v(-1590, 1010.36) * mm, "end": v(-1590, 929.53) * mm});
            skLineSegment(sketch, "E1995.MirrorCS", {"start": v(-1290, 98.15) * mm, "end": v(-1290, 178.98) * mm});
            skLineSegment(sketch, "E1996.MirrorCS", {"start": v(-1830, 317.54) * mm, "end": v(-1830, 236.71) * mm});
            skLineSegment(sketch, "E1997.MirrorCS", {"start": v(-1530, 1345.23) * mm, "end": v(-1600, 1304.81) * mm});
            skLineSegment(sketch, "E1998.MirrorCS", {"start": v(-1120, 196.3) * mm, "end": v(-1050, 236.71) * mm});
            skLineSegment(sketch, "E1999.MirrorCS", {"start": v(-1120, 473.43) * mm, "end": v(-1050, 513.84) * mm});
            skLineSegment(sketch, "E2000.MirrorCS", {"start": v(-1370, 1068.1) * mm, "end": v(-1370, 1148.93) * mm});
            skLineSegment(sketch, "E2001.MirrorCS", {"start": v(-890, 1622.35) * mm, "end": v(-960, 1581.94) * mm});
            skLineSegment(sketch, "E2002.MirrorCS", {"start": v(-960, -80.83) * mm, "end": v(-890, -40.41) * mm});
            skLineSegment(sketch, "E2003.MirrorCS", {"start": v(-1840, 496.52) * mm, "end": v(-1770, 456.1) * mm});
            skLineSegment(sketch, "E2004.MirrorCS", {"start": v(-960, 357.96) * mm, "end": v(-1030, 317.54) * mm});
            skLineSegment(sketch, "E2005.MirrorCS", {"start": v(-1270, 178.98) * mm, "end": v(-1200, 219.4) * mm});
            skLineSegment(sketch, "E2006.MirrorCS", {"start": v(-1760, 473.43) * mm, "end": v(-1690, 513.84) * mm});
            skLineSegment(sketch, "E2007.MirrorCS", {"start": v(-1840, 1720.5) * mm, "end": v(-1770, 1760.92) * mm});
            skLineSegment(sketch, "E2008.MirrorCS", {"start": v(-1110, 1206.66) * mm, "end": v(-1110, 1287.5) * mm});
            skLineSegment(sketch, "E2009.MirrorCS", {"start": v(-1450, 1483.8) * mm, "end": v(-1450, 1564.62) * mm});
            skLineSegment(sketch, "E2010.MirrorCS", {"start": v(-890, 317.54) * mm, "end": v(-960, 357.96) * mm});
            skLineSegment(sketch, "E2011.MirrorCS", {"start": v(-1190, 1068.1) * mm, "end": v(-1120, 1027.68) * mm});
            skLineSegment(sketch, "E2012.MirrorCS", {"start": v(-1290, 1564.62) * mm, "end": v(-1290, 1483.8) * mm});
            skLineSegment(sketch, "E2013.MirrorCS", {"start": v(-1830, 1148.93) * mm, "end": v(-1760, 1189.34) * mm});
            skLineSegment(sketch, "E2014.MirrorCS", {"start": v(-1910, 1483.8) * mm, "end": v(-1840, 1443.38) * mm});
            skLineSegment(sketch, "E2015.MirrorCS", {"start": v(-1350, 871.8) * mm, "end": v(-1350, 790.97) * mm});
            skLineSegment(sketch, "E2016.MirrorCS", {"start": v(-1190, 790.97) * mm, "end": v(-1120, 750.56) * mm});
            skLineSegment(sketch, "E2017.MirrorCS", {"start": v(-1040, 496.52) * mm, "end": v(-1110, 456.1) * mm});
            skLineSegment(sketch, "E2018.MirrorCS", {"start": v(-1190, 1345.23) * mm, "end": v(-1120, 1304.81) * mm});
            skLineSegment(sketch, "E2019.MirrorCS", {"start": v(-1680, 773.65) * mm, "end": v(-1750, 733.23) * mm});
            skLineSegment(sketch, "E2020.MirrorCS", {"start": v(-1680, 1166.25) * mm, "end": v(-1750, 1206.66) * mm});
            skLineSegment(sketch, "E2021.MirrorCS", {"start": v(-870, 790.97) * mm, "end": v(-870, 871.8) * mm});
            skLineSegment(sketch, "E2022.MirrorCS", {"start": v(-1600, 357.96) * mm, "end": v(-1530, 317.54) * mm});
            skLineSegment(sketch, "E2023.MirrorCS", {"start": v(-1910, 98.15) * mm, "end": v(-1840, 57.74) * mm});
            skLineSegment(sketch, "E2024.MirrorCS", {"start": v(-1530, 594.67) * mm, "end": v(-1530, 513.84) * mm});
            skLineSegment(sketch, "E2025.MirrorCS", {"start": v(-890, 1426.06) * mm, "end": v(-890, 1345.23) * mm});
            skLineSegment(sketch, "E2026.MirrorCS", {"start": v(-970, 1483.8) * mm, "end": v(-970, 1564.62) * mm});
            skLineSegment(sketch, "E2027.MirrorCS", {"start": v(-1510, 236.71) * mm, "end": v(-1440, 196.3) * mm});
            skLineSegment(sketch, "E2028.MirrorCS", {"start": v(-870, 1426.06) * mm, "end": v(-870, 1345.23) * mm});
            skLineSegment(sketch, "E2029.MirrorCS", {"start": v(-950, 1206.66) * mm, "end": v(-950, 1287.5) * mm});
            skLineSegment(sketch, "E2030.MirrorCS", {"start": v(-1110, 98.15) * mm, "end": v(-1110, 178.98) * mm});
            skLineSegment(sketch, "E2031.MirrorCS", {"start": v(-1760, 357.96) * mm, "end": v(-1830, 317.54) * mm});
            skLineSegment(sketch, "E2032.MirrorCS", {"start": v(-1040, 1166.25) * mm, "end": v(-1110, 1206.66) * mm});
            skLineSegment(sketch, "E2033.MirrorCS", {"start": v(-1050, 790.97) * mm, "end": v(-1120, 750.56) * mm});
            skLineSegment(sketch, "E2034.MirrorCS", {"start": v(-1270, 375.28) * mm, "end": v(-1200, 334.86) * mm});
            skLineSegment(sketch, "E2035.MirrorCS", {"start": v(-1050, 594.67) * mm, "end": v(-1120, 635.09) * mm});
            skLineSegment(sketch, "E2036.MirrorCS", {"start": v(-1440, 1581.94) * mm, "end": v(-1370, 1622.35) * mm});
            skLineSegment(sketch, "E2037.MirrorCS", {"start": v(-1210, 513.84) * mm, "end": v(-1280, 473.43) * mm});
            skLineSegment(sketch, "E2038.MirrorCS", {"start": v(-1280, 1581.94) * mm, "end": v(-1210, 1622.35) * mm});
            skLineSegment(sketch, "E2039.MirrorCS", {"start": v(-1120, 357.96) * mm, "end": v(-1190, 317.54) * mm});
            skLineSegment(sketch, "E2040.MirrorCS", {"start": v(-1290, 178.98) * mm, "end": v(-1360, 219.4) * mm});
            skLineSegment(sketch, "E2041.MirrorCS", {"start": v(-1680, 219.4) * mm, "end": v(-1610, 178.98) * mm});
            skLineSegment(sketch, "E2042.MirrorCS", {"start": v(-1510, 871.8) * mm, "end": v(-1440, 912.21) * mm});
            skLineSegment(sketch, "E2043.MirrorCS", {"start": v(-1450, 1206.66) * mm, "end": v(-1520, 1166.25) * mm});
            skLineSegment(sketch, "E2044.MirrorCS", {"start": v(-1200, 334.86) * mm, "end": v(-1130, 375.28) * mm});
            skLineSegment(sketch, "E2045.MirrorCS", {"start": v(-810, 1841.75) * mm, "end": v(-880, 1882.16) * mm});
            skLineSegment(sketch, "E2046.MirrorCS", {"start": v(-960, 196.3) * mm, "end": v(-1030, 236.71) * mm});
            skLineSegment(sketch, "E2047.MirrorCS", {"start": v(-1690, 1068.1) * mm, "end": v(-1690, 1148.93) * mm});
            skLineSegment(sketch, "E2048.MirrorCS", {"start": v(-1450, 375.28) * mm, "end": v(-1450, 456.1) * mm});
            skLineSegment(sketch, "E2049.MirrorCS", {"start": v(-1610, 733.23) * mm, "end": v(-1680, 773.65) * mm});
            skLineSegment(sketch, "E2050.MirrorCS", {"start": v(-1040, 1443.38) * mm, "end": v(-1110, 1483.8) * mm});
            skLineSegment(sketch, "E2051.MirrorCS", {"start": v(-1770, 929.53) * mm, "end": v(-1840, 889.12) * mm});
            skLineSegment(sketch, "E2052.MirrorCS", {"start": v(-1290, 652.4) * mm, "end": v(-1290, 733.23) * mm});
            skLineSegment(sketch, "E2053.MirrorCS", {"start": v(-1050, 1068.1) * mm, "end": v(-1050, 1148.93) * mm});
            skLineSegment(sketch, "E2054.MirrorCS", {"start": v(-1610, 1841.75) * mm, "end": v(-1680, 1882.16) * mm});
            skLineSegment(sketch, "E2055.MirrorCS", {"start": v(-960, 750.56) * mm, "end": v(-890, 790.97) * mm});
            skLineSegment(sketch, "E2056.MirrorCS", {"start": v(-1360, 1443.38) * mm, "end": v(-1430, 1483.8) * mm});
            skLineSegment(sketch, "E2057.MirrorCS", {"start": v(-1750, 1841.75) * mm, "end": v(-1680, 1882.16) * mm});
            skLineSegment(sketch, "E2058.MirrorCS", {"start": v(-1360, 1882.16) * mm, "end": v(-1430, 1841.75) * mm});
            skLineSegment(sketch, "E2059.MirrorCS", {"start": v(-1450, 1841.75) * mm, "end": v(-1450, 1760.92) * mm});
            skLineSegment(sketch, "E2060.MirrorCS", {"start": v(-1840, 1050.78) * mm, "end": v(-1770, 1010.36) * mm});
            skLineSegment(sketch, "E2061.MirrorCS", {"start": v(-1270, 1287.5) * mm, "end": v(-1270, 1206.66) * mm});
            skLineSegment(sketch, "E2062.MirrorCS", {"start": v(-1450, 1760.92) * mm, "end": v(-1520, 1720.5) * mm});
            skLineSegment(sketch, "E2063.MirrorCS", {"start": v(-1360, 1327.9) * mm, "end": v(-1430, 1287.5) * mm});
            skLineSegment(sketch, "E2064.MirrorCS", {"start": v(-1910, 375.28) * mm, "end": v(-1910, 456.1) * mm});
            skLineSegment(sketch, "E2065.MirrorCS", {"start": v(-890, 871.8) * mm, "end": v(-960, 912.21) * mm});
            skLineSegment(sketch, "E2066.MirrorCS", {"start": v(-1840, 773.65) * mm, "end": v(-1910, 733.23) * mm});
            skLineSegment(sketch, "E2067.MirrorCS", {"start": v(-1840, 773.65) * mm, "end": v(-1770, 733.23) * mm});
            skLineSegment(sketch, "E2068.MirrorCS", {"start": v(-1040, 1882.16) * mm, "end": v(-1110, 1841.75) * mm});
            skLineSegment(sketch, "E2069.MirrorCS", {"start": v(-1750, 178.98) * mm, "end": v(-1680, 219.4) * mm});
            skLineSegment(sketch, "E2070.MirrorCS", {"start": v(-1600, 473.43) * mm, "end": v(-1670, 513.84) * mm});
            skLineSegment(sketch, "E2071.MirrorCS", {"start": v(-1130, 98.15) * mm, "end": v(-1130, 178.98) * mm});
            skLineSegment(sketch, "E2072.MirrorCS", {"start": v(-1190, 594.67) * mm, "end": v(-1120, 635.09) * mm});
            skLineSegment(sketch, "E2073.MirrorCS", {"start": v(-880, 1166.25) * mm, "end": v(-950, 1206.66) * mm});
            skLineSegment(sketch, "E2074.MirrorCS", {"start": v(-890, 790.97) * mm, "end": v(-890, 871.8) * mm});
            skLineSegment(sketch, "E2075.MirrorCS", {"start": v(-1370, 1345.23) * mm, "end": v(-1370, 1426.06) * mm});
            skLineSegment(sketch, "E2076.MirrorCS", {"start": v(-1200, 57.74) * mm, "end": v(-1130, 98.15) * mm});
            skLineSegment(sketch, "E2077.MirrorCS", {"start": v(-1750, 1760.92) * mm, "end": v(-1750, 1841.75) * mm});
            skLineSegment(sketch, "E2078.MirrorCS", {"start": v(-1450, 178.98) * mm, "end": v(-1450, 98.15) * mm});
            skLineSegment(sketch, "E2079.MirrorCS", {"start": v(-950, 98.15) * mm, "end": v(-950, 178.98) * mm});
            skLineSegment(sketch, "E2080.MirrorCS", {"start": v(-1110, 733.23) * mm, "end": v(-1040, 773.65) * mm});
            skLineSegment(sketch, "E2081.MirrorCS", {"start": v(-1200, 1605.03) * mm, "end": v(-1130, 1564.62) * mm});
            skLineSegment(sketch, "E2082.MirrorCS", {"start": v(-870, 513.84) * mm, "end": v(-800, 473.43) * mm});
            skLineSegment(sketch, "E2083.MirrorCS", {"start": v(-1510, 317.54) * mm, "end": v(-1510, 236.71) * mm});
            skLineSegment(sketch, "E2084.MirrorCS", {"start": v(-1450, 1010.36) * mm, "end": v(-1520, 1050.78) * mm});
            skLineSegment(sketch, "E2085.MirrorCS", {"start": v(-1910, 178.98) * mm, "end": v(-1910, 98.15) * mm});
            skLineSegment(sketch, "E2086.MirrorCS", {"start": v(-1440, 750.56) * mm, "end": v(-1510, 790.97) * mm});
            skLineSegment(sketch, "E2087.MirrorCS", {"start": v(-1770, 98.15) * mm, "end": v(-1770, 178.98) * mm});
            skLineSegment(sketch, "E2088.MirrorCS", {"start": v(-1520, 889.12) * mm, "end": v(-1450, 929.53) * mm});
            skLineSegment(sketch, "E2089.MirrorCS", {"start": v(-890, 1148.93) * mm, "end": v(-890, 1068.1) * mm});
            skLineSegment(sketch, "E2090.MirrorCS", {"start": v(-1910, 1564.62) * mm, "end": v(-1840, 1605.03) * mm});
            skLineSegment(sketch, "E2091.MirrorCS", {"start": v(-1440, 80.83) * mm, "end": v(-1370, 40.41) * mm});
            skLineSegment(sketch, "E2092.MirrorCS", {"start": v(-1830, 790.97) * mm, "end": v(-1830, 871.8) * mm});
            skLineSegment(sketch, "E2093.MirrorCS", {"start": v(-1270, 1010.36) * mm, "end": v(-1200, 1050.78) * mm});
            skLineSegment(sketch, "E2094.MirrorCS", {"start": v(-1520, 334.86) * mm, "end": v(-1590, 375.28) * mm});
            skLineSegment(sketch, "E2095.MirrorCS", {"start": v(-1440, 1466.47) * mm, "end": v(-1370, 1426.06) * mm});
            skLineSegment(sketch, "E2096.MirrorCS", {"start": v(-1450, 456.1) * mm, "end": v(-1520, 496.52) * mm});
            skLineSegment(sketch, "E2097.MirrorCS", {"start": v(-1510, 594.67) * mm, "end": v(-1510, 513.84) * mm});
            skLineSegment(sketch, "E2098.MirrorCS", {"start": v(-970, 652.4) * mm, "end": v(-1040, 612) * mm});
            skLineSegment(sketch, "E2099.MirrorCS", {"start": v(-1830, 1703.18) * mm, "end": v(-1760, 1743.6) * mm});
            skLineSegment(sketch, "E2100.MirrorCS", {"start": v(-870, 1703.18) * mm, "end": v(-800, 1743.6) * mm});
            skLineSegment(sketch, "E2101.0", {"start": v(-1944, 1902.16) * mm, "end": v(-1944, -100.83) * mm});
            skPoint(sketch, "E2102.orphan", {"position": v(-800, -100.83) * mm});
            skLineSegment(sketch, "E2103.0", {"start": v(-730, -40.41) * mm, "end": v(-730, 40.41) * mm});
            skLineSegment(sketch, "E2104.0", {"start": v(-800, 80.83) * mm, "end": v(-870, 40.41) * mm});
            skLineSegment(sketch, "E2105", {"start": v(-730, 40.41) * mm, "end": v(-800, 80.83) * mm});
            skLineSegment(sketch, "E2106", {"start": v(-870, 40.41) * mm, "end": v(-870, -40.41) * mm});
            skLineSegment(sketch, "E2107", {"start": v(-870, -40.41) * mm, "end": v(-800, -80.83) * mm});
            skLineSegment(sketch, "E2108", {"start": v(-800, -80.83) * mm, "end": v(-730, -40.41) * mm});
            skLineSegment(sketch, "E2109.0", {"start": v(-1850, 317.54) * mm, "end": v(-1850, 236.71) * mm});
            skLineSegment(sketch, "E2110", {"start": v(-1850, 317.54) * mm, "end": v(-1910, 352.18) * mm});
            skLineSegment(sketch, "E2111", {"start": v(-1850, 236.71) * mm, "end": v(-1910, 202.07) * mm});
            skLineSegment(sketch, "E2112", {"start": v(-1910, 202.07) * mm, "end": v(-1910, 352.18) * mm});
            skLineSegment(sketch, "E2113", {"start": v(-1850, 513.84) * mm, "end": v(-1850, 594.67) * mm});
            skLineSegment(sketch, "E2114", {"start": v(-1850, 594.67) * mm, "end": v(-1910, 629.31) * mm});
            skLineSegment(sketch, "E2115", {"start": v(-1850, 513.84) * mm, "end": v(-1910, 479.2) * mm});
            skLineSegment(sketch, "E2116", {"start": v(-1910, 479.2) * mm, "end": v(-1910, 629.31) * mm});
            skLineSegment(sketch, "E2117", {"start": v(-1850, 790.97) * mm, "end": v(-1850, 871.8) * mm});
            skLineSegment(sketch, "E2118", {"start": v(-1850, 871.8) * mm, "end": v(-1910, 906.44) * mm});
            skLineSegment(sketch, "E2119", {"start": v(-1850, 1068.1) * mm, "end": v(-1850, 1148.93) * mm});
            skLineSegment(sketch, "E2120", {"start": v(-1850, 1148.93) * mm, "end": v(-1910, 1183.57) * mm});
            skLineSegment(sketch, "E2121", {"start": v(-1850, 1345.23) * mm, "end": v(-1850, 1426.06) * mm});
            skLineSegment(sketch, "E2122", {"start": v(-1850, 1426.06) * mm, "end": v(-1910, 1460.7) * mm});
            skLineSegment(sketch, "E2123", {"start": v(-1850, 1622.35) * mm, "end": v(-1850, 1703.18) * mm});
            skLineSegment(sketch, "E2124", {"start": v(-1850, 1703.18) * mm, "end": v(-1910, 1737.82) * mm});
            skLineSegment(sketch, "E2125", {"start": v(-1850, 790.97) * mm, "end": v(-1910, 756.33) * mm});
            skLineSegment(sketch, "E2126", {"start": v(-1910, 756.33) * mm, "end": v(-1910, 906.44) * mm});
            skLineSegment(sketch, "E2127", {"start": v(-1850, 1068.1) * mm, "end": v(-1910, 1033.46) * mm});
            skLineSegment(sketch, "E2128", {"start": v(-1910, 1033.46) * mm, "end": v(-1910, 1183.57) * mm});
            skLineSegment(sketch, "E2129", {"start": v(-1850, 1345.23) * mm, "end": v(-1910, 1310.59) * mm});
            skLineSegment(sketch, "E2130", {"start": v(-1910, 1310.59) * mm, "end": v(-1910, 1460.7) * mm});
            skLineSegment(sketch, "E2131", {"start": v(-1850, 1622.35) * mm, "end": v(-1910, 1587.71) * mm});
            skLineSegment(sketch, "E2132", {"start": v(-1910, 1587.71) * mm, "end": v(-1910, 1737.82) * mm});
            skLineSegment(sketch, "E2133", {"start": v(-730, 236.71) * mm, "end": v(-800, 196.3) * mm});
            skLineSegment(sketch, "E2134", {"start": v(-730, 317.54) * mm, "end": v(-800, 357.96) * mm});
            skLineSegment(sketch, "E2135", {"start": v(-730, 594.67) * mm, "end": v(-800, 635.09) * mm});
            skLineSegment(sketch, "E2136", {"start": v(-800, 635.09) * mm, "end": v(-870, 594.67) * mm});
            skLineSegment(sketch, "E2137", {"start": v(-730, 871.8) * mm, "end": v(-800, 912.21) * mm});
            skLineSegment(sketch, "E2138", {"start": v(-870, 871.8) * mm, "end": v(-800, 912.21) * mm});
            skLineSegment(sketch, "E2139", {"start": v(-730, 790.97) * mm, "end": v(-800, 750.56) * mm});
            skLineSegment(sketch, "E2140", {"start": v(-870, 1068.1) * mm, "end": v(-800, 1027.68) * mm});
            skLineSegment(sketch, "E2141", {"start": v(-870, 1148.93) * mm, "end": v(-800, 1189.34) * mm});
            skLineSegment(sketch, "E2142", {"start": v(-800, 1189.34) * mm, "end": v(-730, 1148.93) * mm});
            skLineSegment(sketch, "E2143", {"start": v(-870, 1345.23) * mm, "end": v(-800, 1304.81) * mm});
            skLineSegment(sketch, "E2144", {"start": v(-870, 1426.06) * mm, "end": v(-800, 1466.47) * mm});
            skLineSegment(sketch, "E2145", {"start": v(-870, 1622.35) * mm, "end": v(-800, 1581.94) * mm});
            skLineSegment(sketch, "E2146", {"start": v(-730, 1622.35) * mm, "end": v(-800, 1581.94) * mm});
            skLineSegment(sketch, "E2147", {"start": v(-730, 1703.18) * mm, "end": v(-800, 1743.6) * mm});
            skSolve(sketch);
        }
        {
            var Q0;
            Q0=makeQuery(id+"F0.imprint","IMPRINT",FACE,{"disambiguationData":[TD([[makeQuery(id+"F0.imprint","IMPRINT",EDGE,{"derivedFrom":sQuery(id+"F0.wireOp",EDGE,"E0")}),1.0]])]});
            extrude(context, id + "F1", {"entities" : qUnion([Q0]), "depth" : 25 * mm, "offsetDistance" : 25 * mm});
        }
    });
